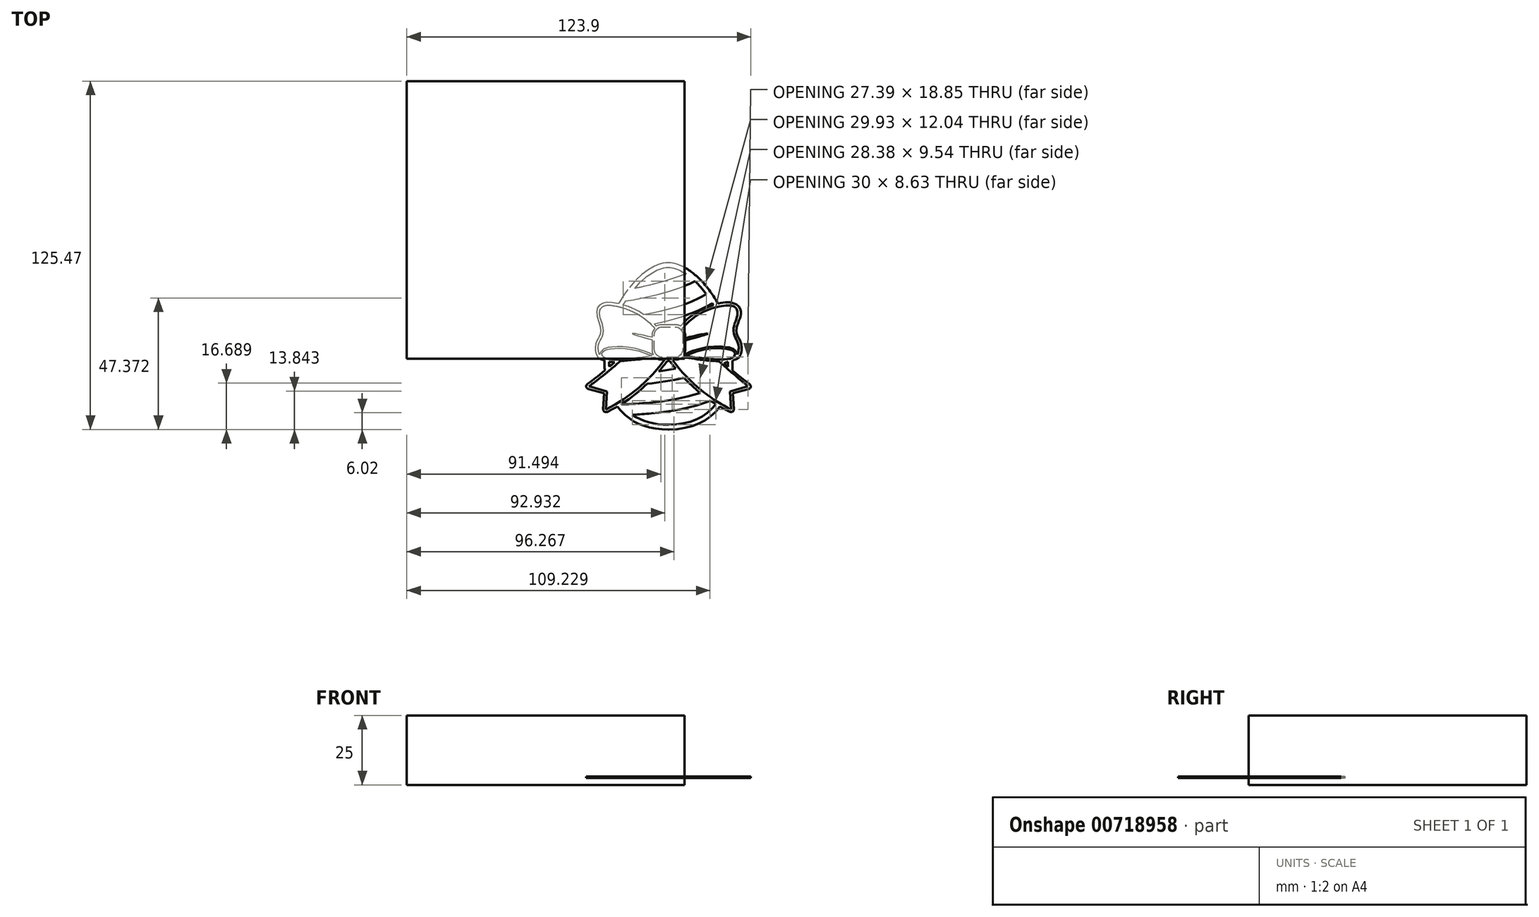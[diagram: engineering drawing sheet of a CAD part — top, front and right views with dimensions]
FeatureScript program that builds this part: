
annotation { "Feature Type Name" : "Feature", "Feature Type Description" : "" }
export const myFeature = defineFeature(function(context is Context, id is Id, definition is map)
    precondition{}
    {
        {
            var Q0;
            Q0=qCreatedBy(makeId("Top.planeOp"),FACE);
            var sketch = newSketch(context, id + "F0", { "sketchPlane" : qUnion([Q0])});
            skLineSegment(sketch, "E0.bottom", {"start": v(0, 0) * mm, "end": v(-100, 0) * mm});
            skLineSegment(sketch, "E0.top", {"start": v(0, 100) * mm, "end": v(-100, 100) * mm});
            skLineSegment(sketch, "E0.left", {"start": v(0, 0) * mm, "end": v(0, 100) * mm});
            skLineSegment(sketch, "E0.right", {"start": v(-100, 0) * mm, "end": v(-100, 100) * mm});
            skSolve(sketch);
        }
        {
            var Q0;
            Q0 = qSketchRegion(id + "F0", true);
            extrude(context, id + "F1", {"entities" : qUnion([Q0]), "depth" : 25 * mm, "offsetDistance" : 25 * mm});
        }
        {
            var Q0;
            Q0=makeQuery(id+"F1.opExtrude","CAP_FACE",FACE,{"disambiguationData":[OSD([sQuery(id+"F0.wireOp",EDGE,"E0.bottom"),sQuery(id+"F0.wireOp",EDGE,"E0.top"),sQuery(id+"F0.wireOp",EDGE,"E0.left"),sQuery(id+"F0.wireOp",EDGE,"E0.right")])],"isStart":false});
            var sketch = newSketch(context, id + "F2", { "sketchPlane" : qUnion([Q0])});
            skLineSegment(sketch, "E1", {"start": v(163.81, -117.28) * mm, "end": v(167.38, -182.07) * mm});
            skLineSegment(sketch, "E2", {"start": v(167.38, -182.07) * mm, "end": v(154.84, -175.69) * mm});
            skLineSegment(sketch, "E3", {"start": v(154.84, -175.69) * mm, "end": v(142.58, -169.14) * mm});
            skLineSegment(sketch, "E4", {"start": v(142.58, -169.14) * mm, "end": v(130.5, -162.31) * mm});
            skLineSegment(sketch, "E5", {"start": v(130.5, -162.31) * mm, "end": v(118.44, -155.06) * mm});
            skLineSegment(sketch, "E6", {"start": v(118.44, -155.06) * mm, "end": v(106.3, -147.27) * mm});
            skLineSegment(sketch, "E7", {"start": v(106.3, -147.27) * mm, "end": v(93.93, -138.8) * mm});
            skLineSegment(sketch, "E8", {"start": v(93.93, -138.8) * mm, "end": v(81.23, -129.55) * mm});
            skLineSegment(sketch, "E9", {"start": v(81.23, -129.55) * mm, "end": v(68.05, -119.37) * mm});
            skLineSegment(sketch, "E10", {"start": v(68.05, -119.37) * mm, "end": v(51.97, -106.13) * mm});
            skLineSegment(sketch, "E11", {"start": v(51.97, -106.13) * mm, "end": v(36.41, -92.4) * mm});
            skLineSegment(sketch, "E12", {"start": v(36.41, -92.4) * mm, "end": v(21.4, -78.23) * mm});
            skLineSegment(sketch, "E13", {"start": v(21.4, -78.23) * mm, "end": v(6.97, -63.66) * mm});
            skLineSegment(sketch, "E14", {"start": v(6.97, -63.66) * mm, "end": v(-6.88, -48.74) * mm});
            skLineSegment(sketch, "E15", {"start": v(-6.88, -48.74) * mm, "end": v(-20.11, -33.52) * mm});
            skLineSegment(sketch, "E16", {"start": v(-20.11, -33.52) * mm, "end": v(-32.72, -18.04) * mm});
            skLineSegment(sketch, "E17", {"start": v(-32.72, -18.04) * mm, "end": v(-44.66, -2.35) * mm});
            skLineSegment(sketch, "E18", {"start": v(-44.66, -2.35) * mm, "end": v(-29.92, -2.35) * mm});
            skLineSegment(sketch, "E19", {"start": v(-29.92, -2.35) * mm, "end": v(-26.75, -2.2) * mm});
            skLineSegment(sketch, "E20", {"start": v(-26.75, -2.2) * mm, "end": v(-23.67, -1.74) * mm});
            skLineSegment(sketch, "E21", {"start": v(-23.67, -1.74) * mm, "end": v(-20.68, -1) * mm});
            skLineSegment(sketch, "E22", {"start": v(-20.68, -1) * mm, "end": v(-17.82, 0) * mm});
            skLineSegment(sketch, "E23", {"start": v(-17.82, 0) * mm, "end": v(-15.08, 1.27) * mm});
            skLineSegment(sketch, "E24", {"start": v(-15.08, 1.27) * mm, "end": v(-12.49, 2.77) * mm});
            skLineSegment(sketch, "E25", {"start": v(-12.49, 2.77) * mm, "end": v(-10.05, 4.5) * mm});
            skLineSegment(sketch, "E26", {"start": v(-10.05, 4.5) * mm, "end": v(-7.78, 6.44) * mm});
            skLineSegment(sketch, "E27", {"start": v(-7.78, 6.44) * mm, "end": v(3.96, 4.52) * mm});
            skLineSegment(sketch, "E28", {"start": v(3.96, 4.52) * mm, "end": v(15.22, 2.75) * mm});
            skLineSegment(sketch, "E29", {"start": v(15.22, 2.75) * mm, "end": v(26.02, 1.11) * mm});
            skLineSegment(sketch, "E30", {"start": v(26.02, 1.11) * mm, "end": v(36.37, -0.38) * mm});
            skLineSegment(sketch, "E31", {"start": v(36.37, -0.38) * mm, "end": v(46.3, -1.74) * mm});
            skLineSegment(sketch, "E32", {"start": v(46.3, -1.74) * mm, "end": v(55.8, -2.97) * mm});
            skLineSegment(sketch, "E33", {"start": v(55.8, -2.97) * mm, "end": v(64.92, -4.07) * mm});
            skLineSegment(sketch, "E34", {"start": v(64.92, -4.07) * mm, "end": v(73.64, -5.04) * mm});
            skLineSegment(sketch, "E35", {"start": v(73.64, -5.04) * mm, "end": v(80.45, -5.73) * mm});
            skLineSegment(sketch, "E36", {"start": v(80.45, -5.73) * mm, "end": v(87.02, -6.34) * mm});
            skLineSegment(sketch, "E37", {"start": v(87.02, -6.34) * mm, "end": v(93.36, -6.88) * mm});
            skLineSegment(sketch, "E38", {"start": v(93.36, -6.88) * mm, "end": v(99.47, -7.32) * mm});
            skLineSegment(sketch, "E39", {"start": v(99.47, -7.32) * mm, "end": v(105.35, -7.69) * mm});
            skLineSegment(sketch, "E40", {"start": v(105.35, -7.69) * mm, "end": v(111, -7.97) * mm});
            skLineSegment(sketch, "E41", {"start": v(111, -7.97) * mm, "end": v(116.44, -8.17) * mm});
            skLineSegment(sketch, "E42", {"start": v(116.44, -8.17) * mm, "end": v(121.65, -8.28) * mm});
            skLineSegment(sketch, "E43", {"start": v(121.65, -8.28) * mm, "end": v(123.37, -8.3) * mm});
            skLineSegment(sketch, "E44", {"start": v(123.37, -8.3) * mm, "end": v(139.96, -22.95) * mm});
            skLineSegment(sketch, "E45", {"start": v(139.96, -22.95) * mm, "end": v(155.27, -36.35) * mm});
            skLineSegment(sketch, "E46", {"start": v(155.27, -36.35) * mm, "end": v(169.47, -48.67) * mm});
            skLineSegment(sketch, "E47", {"start": v(169.47, -48.67) * mm, "end": v(182.71, -60.04) * mm});
            skLineSegment(sketch, "E48", {"start": v(182.71, -60.04) * mm, "end": v(195.15, -70.62) * mm});
            skLineSegment(sketch, "E49", {"start": v(195.15, -70.62) * mm, "end": v(206.94, -80.56) * mm});
            skLineSegment(sketch, "E50", {"start": v(206.94, -80.56) * mm, "end": v(218.25, -90) * mm});
            skLineSegment(sketch, "E51", {"start": v(218.25, -90) * mm, "end": v(229.24, -99.1) * mm});
            skLineSegment(sketch, "E52", {"start": v(229.24, -99.1) * mm, "end": v(163.81, -117.28) * mm});
            skLineSegment(sketch, "E53", {"start": v(-56.23, -237.65) * mm, "end": v(-56.4, -237.65) * mm});
            skLineSegment(sketch, "E54", {"start": v(-56.4, -237.65) * mm, "end": v(-56.55, -237.65) * mm});
            skLineSegment(sketch, "E55", {"start": v(-56.55, -237.65) * mm, "end": v(-56.7, -237.65) * mm});
            skLineSegment(sketch, "E56", {"start": v(-56.7, -237.65) * mm, "end": v(-56.86, -237.66) * mm});
            skLineSegment(sketch, "E57", {"start": v(-56.86, -237.66) * mm, "end": v(-57.02, -237.66) * mm});
            skLineSegment(sketch, "E58", {"start": v(-57.02, -237.66) * mm, "end": v(-57.17, -237.66) * mm});
            skLineSegment(sketch, "E59", {"start": v(-57.17, -237.66) * mm, "end": v(-57.33, -237.66) * mm});
            skLineSegment(sketch, "E60", {"start": v(-57.33, -237.66) * mm, "end": v(-57.49, -237.66) * mm});
            skLineSegment(sketch, "E61", {"start": v(-57.49, -237.66) * mm, "end": v(-76.77, -237.1) * mm});
            skLineSegment(sketch, "E62", {"start": v(-76.77, -237.1) * mm, "end": v(-95.19, -235.4) * mm});
            skLineSegment(sketch, "E63", {"start": v(-95.19, -235.4) * mm, "end": v(-112.74, -232.6) * mm});
            skLineSegment(sketch, "E64", {"start": v(-112.74, -232.6) * mm, "end": v(-129.41, -228.67) * mm});
            skLineSegment(sketch, "E65", {"start": v(-129.41, -228.67) * mm, "end": v(-145.22, -223.63) * mm});
            skLineSegment(sketch, "E66", {"start": v(-145.22, -223.63) * mm, "end": v(-160.14, -217.47) * mm});
            skLineSegment(sketch, "E67", {"start": v(-160.14, -217.47) * mm, "end": v(-174.18, -210.21) * mm});
            skLineSegment(sketch, "E68", {"start": v(-174.18, -210.21) * mm, "end": v(-187.33, -201.84) * mm});
            skLineSegment(sketch, "E69", {"start": v(-187.33, -201.84) * mm, "end": v(-178.84, -201.39) * mm});
            skLineSegment(sketch, "E70", {"start": v(-178.84, -201.39) * mm, "end": v(-170.35, -200.87) * mm});
            skLineSegment(sketch, "E71", {"start": v(-170.35, -200.87) * mm, "end": v(-161.86, -200.3) * mm});
            skLineSegment(sketch, "E72", {"start": v(-161.86, -200.3) * mm, "end": v(-153.4, -199.68) * mm});
            skLineSegment(sketch, "E73", {"start": v(-153.4, -199.68) * mm, "end": v(-144.93, -199.02) * mm});
            skLineSegment(sketch, "E74", {"start": v(-144.93, -199.02) * mm, "end": v(-136.49, -198.3) * mm});
            skLineSegment(sketch, "E75", {"start": v(-136.49, -198.3) * mm, "end": v(-128.05, -197.54) * mm});
            skLineSegment(sketch, "E76", {"start": v(-128.05, -197.54) * mm, "end": v(-119.64, -196.73) * mm});
            skLineSegment(sketch, "E77", {"start": v(-119.64, -196.73) * mm, "end": v(-92.7, -193.81) * mm});
            skLineSegment(sketch, "E78", {"start": v(-92.7, -193.81) * mm, "end": v(-65.6, -190.27) * mm});
            skLineSegment(sketch, "E79", {"start": v(-65.6, -190.27) * mm, "end": v(-38.45, -186.02) * mm});
            skLineSegment(sketch, "E80", {"start": v(-38.45, -186.02) * mm, "end": v(-11.35, -181) * mm});
            skLineSegment(sketch, "E81", {"start": v(-11.35, -181) * mm, "end": v(15.61, -175.09) * mm});
            skLineSegment(sketch, "E82", {"start": v(15.61, -175.09) * mm, "end": v(42.34, -168.23) * mm});
            skLineSegment(sketch, "E83", {"start": v(42.34, -168.23) * mm, "end": v(68.74, -160.35) * mm});
            skLineSegment(sketch, "E84", {"start": v(68.74, -160.35) * mm, "end": v(94.7, -151.34) * mm});
            skLineSegment(sketch, "E85", {"start": v(94.7, -151.34) * mm, "end": v(96.9, -152.84) * mm});
            skLineSegment(sketch, "E86", {"start": v(96.9, -152.84) * mm, "end": v(99.12, -154.32) * mm});
            skLineSegment(sketch, "E87", {"start": v(99.12, -154.32) * mm, "end": v(101.34, -155.8) * mm});
            skLineSegment(sketch, "E88", {"start": v(101.34, -155.8) * mm, "end": v(103.58, -157.28) * mm});
            skLineSegment(sketch, "E89", {"start": v(103.58, -157.28) * mm, "end": v(105.84, -158.75) * mm});
            skLineSegment(sketch, "E90", {"start": v(105.84, -158.75) * mm, "end": v(108.1, -160.2) * mm});
            skLineSegment(sketch, "E91", {"start": v(108.1, -160.2) * mm, "end": v(110.38, -161.66) * mm});
            skLineSegment(sketch, "E92", {"start": v(110.38, -161.66) * mm, "end": v(112.68, -163.1) * mm});
            skLineSegment(sketch, "E93", {"start": v(112.68, -163.1) * mm, "end": v(98.11, -180.4) * mm});
            skLineSegment(sketch, "E94", {"start": v(98.11, -180.4) * mm, "end": v(81.65, -195.45) * mm});
            skLineSegment(sketch, "E95", {"start": v(81.65, -195.45) * mm, "end": v(63.3, -208.22) * mm});
            skLineSegment(sketch, "E96", {"start": v(63.3, -208.22) * mm, "end": v(43.09, -218.7) * mm});
            skLineSegment(sketch, "E97", {"start": v(43.09, -218.7) * mm, "end": v(21.01, -226.9) * mm});
            skLineSegment(sketch, "E98", {"start": v(21.01, -226.9) * mm, "end": v(-2.9, -232.8) * mm});
            skLineSegment(sketch, "E99", {"start": v(-2.9, -232.8) * mm, "end": v(-28.66, -236.39) * mm});
            skLineSegment(sketch, "E100", {"start": v(-28.66, -236.39) * mm, "end": v(-56.23, -237.65) * mm});
            skLineSegment(sketch, "E101", {"start": v(-226.12, -163.97) * mm, "end": v(-226.23, -163.83) * mm});
            skLineSegment(sketch, "E102", {"start": v(-226.23, -163.83) * mm, "end": v(-226.33, -163.68) * mm});
            skLineSegment(sketch, "E103", {"start": v(-226.33, -163.68) * mm, "end": v(-226.44, -163.54) * mm});
            skLineSegment(sketch, "E104", {"start": v(-226.44, -163.54) * mm, "end": v(-226.54, -163.39) * mm});
            skLineSegment(sketch, "E105", {"start": v(-226.54, -163.39) * mm, "end": v(-226.65, -163.24) * mm});
            skLineSegment(sketch, "E106", {"start": v(-226.65, -163.24) * mm, "end": v(-226.75, -163.1) * mm});
            skLineSegment(sketch, "E107", {"start": v(-226.75, -163.1) * mm, "end": v(-226.86, -162.95) * mm});
            skLineSegment(sketch, "E108", {"start": v(-226.86, -162.95) * mm, "end": v(-226.96, -162.8) * mm});
            skLineSegment(sketch, "E109", {"start": v(-226.96, -162.8) * mm, "end": v(-213.7, -154.2) * mm});
            skLineSegment(sketch, "E110", {"start": v(-213.7, -154.2) * mm, "end": v(-200.9, -145.37) * mm});
            skLineSegment(sketch, "E111", {"start": v(-200.9, -145.37) * mm, "end": v(-188.59, -136.36) * mm});
            skLineSegment(sketch, "E112", {"start": v(-188.59, -136.36) * mm, "end": v(-176.75, -127.22) * mm});
            skLineSegment(sketch, "E113", {"start": v(-176.75, -127.22) * mm, "end": v(-165.4, -117.97) * mm});
            skLineSegment(sketch, "E114", {"start": v(-165.4, -117.97) * mm, "end": v(-154.53, -108.67) * mm});
            skLineSegment(sketch, "E115", {"start": v(-154.53, -108.67) * mm, "end": v(-144.14, -99.36) * mm});
            skLineSegment(sketch, "E116", {"start": v(-144.14, -99.36) * mm, "end": v(-134.25, -90.08) * mm});
            skLineSegment(sketch, "E117", {"start": v(-134.25, -90.08) * mm, "end": v(-117.46, -88.18) * mm});
            skLineSegment(sketch, "E118", {"start": v(-117.46, -88.18) * mm, "end": v(-100.88, -86.12) * mm});
            skLineSegment(sketch, "E119", {"start": v(-100.88, -86.12) * mm, "end": v(-84.43, -83.88) * mm});
            skLineSegment(sketch, "E120", {"start": v(-84.43, -83.88) * mm, "end": v(-68.06, -81.4) * mm});
            skLineSegment(sketch, "E121", {"start": v(-68.06, -81.4) * mm, "end": v(-51.68, -78.67) * mm});
            skLineSegment(sketch, "E122", {"start": v(-51.68, -78.67) * mm, "end": v(-35.25, -75.65) * mm});
            skLineSegment(sketch, "E123", {"start": v(-35.25, -75.65) * mm, "end": v(-18.7, -72.29) * mm});
            skLineSegment(sketch, "E124", {"start": v(-18.7, -72.29) * mm, "end": v(-1.95, -68.57) * mm});
            skLineSegment(sketch, "E125", {"start": v(-1.95, -68.57) * mm, "end": v(4.46, -75.23) * mm});
            skLineSegment(sketch, "E126", {"start": v(4.46, -75.23) * mm, "end": v(11.14, -81.96) * mm});
            skLineSegment(sketch, "E127", {"start": v(11.14, -81.96) * mm, "end": v(18.1, -88.76) * mm});
            skLineSegment(sketch, "E128", {"start": v(18.1, -88.76) * mm, "end": v(25.31, -95.6) * mm});
            skLineSegment(sketch, "E129", {"start": v(25.31, -95.6) * mm, "end": v(32.8, -102.47) * mm});
            skLineSegment(sketch, "E130", {"start": v(32.8, -102.47) * mm, "end": v(40.55, -109.35) * mm});
            skLineSegment(sketch, "E131", {"start": v(40.55, -109.35) * mm, "end": v(48.56, -116.23) * mm});
            skLineSegment(sketch, "E132", {"start": v(48.56, -116.23) * mm, "end": v(56.84, -123.08) * mm});
            skLineSegment(sketch, "E133", {"start": v(56.84, -123.08) * mm, "end": v(34.49, -129.86) * mm});
            skLineSegment(sketch, "E134", {"start": v(34.49, -129.86) * mm, "end": v(11.87, -135.85) * mm});
            skLineSegment(sketch, "E135", {"start": v(11.87, -135.85) * mm, "end": v(-10.94, -141.1) * mm});
            skLineSegment(sketch, "E136", {"start": v(-10.94, -141.1) * mm, "end": v(-33.9, -145.66) * mm});
            skLineSegment(sketch, "E137", {"start": v(-33.9, -145.66) * mm, "end": v(-56.93, -149.6) * mm});
            skLineSegment(sketch, "E138", {"start": v(-56.93, -149.6) * mm, "end": v(-79.98, -152.96) * mm});
            skLineSegment(sketch, "E139", {"start": v(-79.98, -152.96) * mm, "end": v(-102.98, -155.8) * mm});
            skLineSegment(sketch, "E140", {"start": v(-102.98, -155.8) * mm, "end": v(-125.86, -158.2) * mm});
            skLineSegment(sketch, "E141", {"start": v(-125.86, -158.2) * mm, "end": v(-138.3, -159.33) * mm});
            skLineSegment(sketch, "E142", {"start": v(-138.3, -159.33) * mm, "end": v(-150.79, -160.36) * mm});
            skLineSegment(sketch, "E143", {"start": v(-150.79, -160.36) * mm, "end": v(-163.3, -161.28) * mm});
            skLineSegment(sketch, "E144", {"start": v(-163.3, -161.28) * mm, "end": v(-175.83, -162.08) * mm});
            skLineSegment(sketch, "E145", {"start": v(-175.83, -162.08) * mm, "end": v(-188.39, -162.75) * mm});
            skLineSegment(sketch, "E146", {"start": v(-188.39, -162.75) * mm, "end": v(-200.96, -163.3) * mm});
            skLineSegment(sketch, "E147", {"start": v(-200.96, -163.3) * mm, "end": v(-213.54, -163.7) * mm});
            skLineSegment(sketch, "E148", {"start": v(-213.54, -163.7) * mm, "end": v(-226.12, -163.97) * mm});
            skLineSegment(sketch, "E149", {"start": v(-282.45, -182.06) * mm, "end": v(-278.88, -117.28) * mm});
            skLineSegment(sketch, "E150", {"start": v(-278.88, -117.28) * mm, "end": v(-343.74, -99.24) * mm});
            skLineSegment(sketch, "E151", {"start": v(-343.74, -99.24) * mm, "end": v(-336.1, -93.6) * mm});
            skLineSegment(sketch, "E152", {"start": v(-336.1, -93.6) * mm, "end": v(-331.86, -90.45) * mm});
            skLineSegment(sketch, "E153", {"start": v(-331.86, -90.45) * mm, "end": v(-327, -86.8) * mm});
            skLineSegment(sketch, "E154", {"start": v(-327, -86.8) * mm, "end": v(-321.5, -82.62) * mm});
            skLineSegment(sketch, "E155", {"start": v(-321.5, -82.62) * mm, "end": v(-315.4, -77.93) * mm});
            skLineSegment(sketch, "E156", {"start": v(-315.4, -77.93) * mm, "end": v(-308.71, -72.73) * mm});
            skLineSegment(sketch, "E157", {"start": v(-308.71, -72.73) * mm, "end": v(-301.45, -67.01) * mm});
            skLineSegment(sketch, "E158", {"start": v(-301.45, -67.01) * mm, "end": v(-293.64, -60.8) * mm});
            skLineSegment(sketch, "E159", {"start": v(-293.64, -60.8) * mm, "end": v(-285.29, -54.06) * mm});
            skLineSegment(sketch, "E160", {"start": v(-285.29, -54.06) * mm, "end": v(-283.42, -52.55) * mm});
            skLineSegment(sketch, "E161", {"start": v(-283.42, -52.55) * mm, "end": v(-281.54, -51.02) * mm});
            skLineSegment(sketch, "E162", {"start": v(-281.54, -51.02) * mm, "end": v(-279.63, -49.46) * mm});
            skLineSegment(sketch, "E163", {"start": v(-279.63, -49.46) * mm, "end": v(-277.7, -47.88) * mm});
            skLineSegment(sketch, "E164", {"start": v(-277.7, -47.88) * mm, "end": v(-275.73, -46.27) * mm});
            skLineSegment(sketch, "E165", {"start": v(-275.73, -46.27) * mm, "end": v(-273.75, -44.64) * mm});
            skLineSegment(sketch, "E166", {"start": v(-273.75, -44.64) * mm, "end": v(-271.74, -42.98) * mm});
            skLineSegment(sketch, "E167", {"start": v(-271.74, -42.98) * mm, "end": v(-269.71, -41.3) * mm});
            skLineSegment(sketch, "E168", {"start": v(-269.71, -41.3) * mm, "end": v(-265.33, -37.67) * mm});
            skLineSegment(sketch, "E169", {"start": v(-265.33, -37.67) * mm, "end": v(-260.85, -33.93) * mm});
            skLineSegment(sketch, "E170", {"start": v(-260.85, -33.93) * mm, "end": v(-256.28, -30.1) * mm});
            skLineSegment(sketch, "E171", {"start": v(-256.28, -30.1) * mm, "end": v(-251.6, -26.15) * mm});
            skLineSegment(sketch, "E172", {"start": v(-251.6, -26.15) * mm, "end": v(-246.83, -22.1) * mm});
            skLineSegment(sketch, "E173", {"start": v(-246.83, -22.1) * mm, "end": v(-241.95, -17.93) * mm});
            skLineSegment(sketch, "E174", {"start": v(-241.95, -17.93) * mm, "end": v(-236.97, -13.66) * mm});
            skLineSegment(sketch, "E175", {"start": v(-236.97, -13.66) * mm, "end": v(-231.9, -9.26) * mm});
            skLineSegment(sketch, "E176", {"start": v(-231.9, -9.26) * mm, "end": v(-230.65, -8.2) * mm});
            skLineSegment(sketch, "E177", {"start": v(-230.65, -8.2) * mm, "end": v(-229.02, -8.13) * mm});
            skLineSegment(sketch, "E178", {"start": v(-229.02, -8.13) * mm, "end": v(-217.5, -7.57) * mm});
            skLineSegment(sketch, "E179", {"start": v(-217.5, -7.57) * mm, "end": v(-205.04, -6.67) * mm});
            skLineSegment(sketch, "E180", {"start": v(-205.04, -6.67) * mm, "end": v(-191.57, -5.4) * mm});
            skLineSegment(sketch, "E181", {"start": v(-191.57, -5.4) * mm, "end": v(-177.03, -3.78) * mm});
            skLineSegment(sketch, "E182", {"start": v(-177.03, -3.78) * mm, "end": v(-161.35, -1.78) * mm});
            skLineSegment(sketch, "E183", {"start": v(-161.35, -1.78) * mm, "end": v(-144.47, 0.6) * mm});
            skLineSegment(sketch, "E184", {"start": v(-144.47, 0.6) * mm, "end": v(-126.3, 3.36) * mm});
            skLineSegment(sketch, "E185", {"start": v(-126.3, 3.36) * mm, "end": v(-106.8, 6.52) * mm});
            skLineSegment(sketch, "E186", {"start": v(-106.8, 6.52) * mm, "end": v(-104.54, 4.56) * mm});
            skLineSegment(sketch, "E187", {"start": v(-104.54, 4.56) * mm, "end": v(-102.1, 2.82) * mm});
            skLineSegment(sketch, "E188", {"start": v(-102.1, 2.82) * mm, "end": v(-99.5, 1.3) * mm});
            skLineSegment(sketch, "E189", {"start": v(-99.5, 1.3) * mm, "end": v(-96.74, 0.03) * mm});
            skLineSegment(sketch, "E190", {"start": v(-96.74, 0.03) * mm, "end": v(-93.86, -1) * mm});
            skLineSegment(sketch, "E191", {"start": v(-93.86, -1) * mm, "end": v(-90.87, -1.74) * mm});
            skLineSegment(sketch, "E192", {"start": v(-90.87, -1.74) * mm, "end": v(-87.77, -2.2) * mm});
            skLineSegment(sketch, "E193", {"start": v(-87.77, -2.2) * mm, "end": v(-84.59, -2.35) * mm});
            skLineSegment(sketch, "E194", {"start": v(-84.59, -2.35) * mm, "end": v(-70.37, -2.35) * mm});
            skLineSegment(sketch, "E195", {"start": v(-70.37, -2.35) * mm, "end": v(-91.42, -29.4) * mm});
            skLineSegment(sketch, "E196", {"start": v(-91.42, -29.4) * mm, "end": v(-114.02, -55.34) * mm});
            skLineSegment(sketch, "E197", {"start": v(-114.02, -55.34) * mm, "end": v(-138.17, -80.06) * mm});
            skLineSegment(sketch, "E198", {"start": v(-138.17, -80.06) * mm, "end": v(-163.87, -103.47) * mm});
            skLineSegment(sketch, "E199", {"start": v(-163.87, -103.47) * mm, "end": v(-191.14, -125.47) * mm});
            skLineSegment(sketch, "E200", {"start": v(-191.14, -125.47) * mm, "end": v(-220, -145.97) * mm});
            skLineSegment(sketch, "E201", {"start": v(-220, -145.97) * mm, "end": v(-250.42, -164.87) * mm});
            skLineSegment(sketch, "E202", {"start": v(-250.42, -164.87) * mm, "end": v(-282.45, -182.06) * mm});
            skLineSegment(sketch, "E203", {"start": v(-271.42, -10.7) * mm, "end": v(-269.07, -11) * mm});
            skLineSegment(sketch, "E204", {"start": v(-269.07, -11) * mm, "end": v(-266.65, -11.27) * mm});
            skLineSegment(sketch, "E205", {"start": v(-266.65, -11.27) * mm, "end": v(-264.17, -11.5) * mm});
            skLineSegment(sketch, "E206", {"start": v(-264.17, -11.5) * mm, "end": v(-261.61, -11.68) * mm});
            skLineSegment(sketch, "E207", {"start": v(-261.61, -11.68) * mm, "end": v(-259, -11.84) * mm});
            skLineSegment(sketch, "E208", {"start": v(-259, -11.84) * mm, "end": v(-256.3, -11.97) * mm});
            skLineSegment(sketch, "E209", {"start": v(-256.3, -11.97) * mm, "end": v(-253.52, -12.06) * mm});
            skLineSegment(sketch, "E210", {"start": v(-253.52, -12.06) * mm, "end": v(-250.67, -12.13) * mm});
            skLineSegment(sketch, "E211", {"start": v(-250.67, -12.13) * mm, "end": v(-253.28, -14.36) * mm});
            skLineSegment(sketch, "E212", {"start": v(-253.28, -14.36) * mm, "end": v(-255.86, -16.55) * mm});
            skLineSegment(sketch, "E213", {"start": v(-255.86, -16.55) * mm, "end": v(-258.4, -18.7) * mm});
            skLineSegment(sketch, "E214", {"start": v(-258.4, -18.7) * mm, "end": v(-260.91, -20.82) * mm});
            skLineSegment(sketch, "E215", {"start": v(-260.91, -20.82) * mm, "end": v(-263.4, -22.9) * mm});
            skLineSegment(sketch, "E216", {"start": v(-263.4, -22.9) * mm, "end": v(-265.85, -24.96) * mm});
            skLineSegment(sketch, "E217", {"start": v(-265.85, -24.96) * mm, "end": v(-268.28, -27) * mm});
            skLineSegment(sketch, "E218", {"start": v(-268.28, -27) * mm, "end": v(-270.68, -29) * mm});
            skLineSegment(sketch, "E219", {"start": v(-270.68, -29) * mm, "end": v(-270.82, -26.73) * mm});
            skLineSegment(sketch, "E220", {"start": v(-270.82, -26.73) * mm, "end": v(-270.95, -24.45) * mm});
            skLineSegment(sketch, "E221", {"start": v(-270.95, -24.45) * mm, "end": v(-271.07, -22.16) * mm});
            skLineSegment(sketch, "E222", {"start": v(-271.07, -22.16) * mm, "end": v(-271.17, -19.88) * mm});
            skLineSegment(sketch, "E223", {"start": v(-271.17, -19.88) * mm, "end": v(-271.25, -17.6) * mm});
            skLineSegment(sketch, "E224", {"start": v(-271.25, -17.6) * mm, "end": v(-271.33, -15.3) * mm});
            skLineSegment(sketch, "E225", {"start": v(-271.33, -15.3) * mm, "end": v(-271.38, -13) * mm});
            skLineSegment(sketch, "E226", {"start": v(-271.38, -13) * mm, "end": v(-271.42, -10.7) * mm});
            skLineSegment(sketch, "E227", {"start": v(-290.4, 5.49) * mm, "end": v(-292.84, 7.34) * mm});
            skLineSegment(sketch, "E228", {"start": v(-292.84, 7.34) * mm, "end": v(-294.9, 9.9) * mm});
            skLineSegment(sketch, "E229", {"start": v(-294.9, 9.9) * mm, "end": v(-296.34, 13) * mm});
            skLineSegment(sketch, "E230", {"start": v(-296.34, 13) * mm, "end": v(-296.95, 16.44) * mm});
            skLineSegment(sketch, "E231", {"start": v(-296.95, 16.44) * mm, "end": v(-296.5, 20.07) * mm});
            skLineSegment(sketch, "E232", {"start": v(-296.5, 20.07) * mm, "end": v(-294.8, 23.7) * mm});
            skLineSegment(sketch, "E233", {"start": v(-294.8, 23.7) * mm, "end": v(-291.59, 27.15) * mm});
            skLineSegment(sketch, "E234", {"start": v(-291.59, 27.15) * mm, "end": v(-286.67, 30.27) * mm});
            skLineSegment(sketch, "E235", {"start": v(-286.67, 30.27) * mm, "end": v(-279.2, 32.97) * mm});
            skLineSegment(sketch, "E236", {"start": v(-279.2, 32.97) * mm, "end": v(-267.67, 35.5) * mm});
            skLineSegment(sketch, "E237", {"start": v(-267.67, 35.5) * mm, "end": v(-252.5, 37.37) * mm});
            skLineSegment(sketch, "E238", {"start": v(-252.5, 37.37) * mm, "end": v(-234.13, 38.04) * mm});
            skLineSegment(sketch, "E239", {"start": v(-234.13, 38.04) * mm, "end": v(-212.95, 37.01) * mm});
            skLineSegment(sketch, "E240", {"start": v(-212.95, 37.01) * mm, "end": v(-189.4, 33.76) * mm});
            skLineSegment(sketch, "E241", {"start": v(-189.4, 33.76) * mm, "end": v(-163.88, 27.79) * mm});
            skLineSegment(sketch, "E242", {"start": v(-163.88, 27.79) * mm, "end": v(-136.82, 18.56) * mm});
            skLineSegment(sketch, "E243", {"start": v(-136.82, 18.56) * mm, "end": v(-136.4, 18.4) * mm});
            skLineSegment(sketch, "E244", {"start": v(-136.4, 18.4) * mm, "end": v(-135.98, 18.24) * mm});
            skLineSegment(sketch, "E245", {"start": v(-135.98, 18.24) * mm, "end": v(-135.55, 18.08) * mm});
            skLineSegment(sketch, "E246", {"start": v(-135.55, 18.08) * mm, "end": v(-135.13, 17.92) * mm});
            skLineSegment(sketch, "E247", {"start": v(-135.13, 17.92) * mm, "end": v(-134.71, 17.76) * mm});
            skLineSegment(sketch, "E248", {"start": v(-134.71, 17.76) * mm, "end": v(-134.29, 17.6) * mm});
            skLineSegment(sketch, "E249", {"start": v(-134.29, 17.6) * mm, "end": v(-133.87, 17.43) * mm});
            skLineSegment(sketch, "E250", {"start": v(-133.87, 17.43) * mm, "end": v(-133.45, 17.26) * mm});
            skLineSegment(sketch, "E251", {"start": v(-133.45, 17.26) * mm, "end": v(-118.07, 10.91) * mm});
            skLineSegment(sketch, "E252", {"start": v(-118.07, 10.91) * mm, "end": v(-134.51, 8.4) * mm});
            skLineSegment(sketch, "E253", {"start": v(-134.51, 8.4) * mm, "end": v(-151.35, 5.91) * mm});
            skLineSegment(sketch, "E254", {"start": v(-151.35, 5.91) * mm, "end": v(-167.14, 3.76) * mm});
            skLineSegment(sketch, "E255", {"start": v(-167.14, 3.76) * mm, "end": v(-181.9, 1.95) * mm});
            skLineSegment(sketch, "E256", {"start": v(-181.9, 1.95) * mm, "end": v(-195.69, 0.48) * mm});
            skLineSegment(sketch, "E257", {"start": v(-195.69, 0.48) * mm, "end": v(-208.5, -0.67) * mm});
            skLineSegment(sketch, "E258", {"start": v(-208.5, -0.67) * mm, "end": v(-220.36, -1.48) * mm});
            skLineSegment(sketch, "E259", {"start": v(-220.36, -1.48) * mm, "end": v(-231.3, -1.97) * mm});
            skLineSegment(sketch, "E260", {"start": v(-231.3, -1.97) * mm, "end": v(-241.33, -2.13) * mm});
            skLineSegment(sketch, "E261", {"start": v(-241.33, -2.13) * mm, "end": v(-242.35, -2.13) * mm});
            skLineSegment(sketch, "E262", {"start": v(-242.35, -2.13) * mm, "end": v(-246.55, -2.11) * mm});
            skLineSegment(sketch, "E263", {"start": v(-246.55, -2.11) * mm, "end": v(-250.57, -2.06) * mm});
            skLineSegment(sketch, "E264", {"start": v(-250.57, -2.06) * mm, "end": v(-254.42, -1.95) * mm});
            skLineSegment(sketch, "E265", {"start": v(-254.42, -1.95) * mm, "end": v(-258.1, -1.8) * mm});
            skLineSegment(sketch, "E266", {"start": v(-258.1, -1.8) * mm, "end": v(-261.64, -1.59) * mm});
            skLineSegment(sketch, "E267", {"start": v(-261.64, -1.59) * mm, "end": v(-265.02, -1.3) * mm});
            skLineSegment(sketch, "E268", {"start": v(-265.02, -1.3) * mm, "end": v(-268.26, -0.96) * mm});
            skLineSegment(sketch, "E269", {"start": v(-268.26, -0.96) * mm, "end": v(-271.35, -0.54) * mm});
            skLineSegment(sketch, "E270", {"start": v(-271.35, -0.54) * mm, "end": v(-273.72, -0.15) * mm});
            skLineSegment(sketch, "E271", {"start": v(-273.72, -0.15) * mm, "end": v(-276.01, 0.3) * mm});
            skLineSegment(sketch, "E272", {"start": v(-276.01, 0.3) * mm, "end": v(-278.22, 0.82) * mm});
            skLineSegment(sketch, "E273", {"start": v(-278.22, 0.82) * mm, "end": v(-280.35, 1.4) * mm});
            skLineSegment(sketch, "E274", {"start": v(-280.35, 1.4) * mm, "end": v(-282.4, 2.04) * mm});
            skLineSegment(sketch, "E275", {"start": v(-282.4, 2.04) * mm, "end": v(-284.39, 2.75) * mm});
            skLineSegment(sketch, "E276", {"start": v(-284.39, 2.75) * mm, "end": v(-286.3, 3.53) * mm});
            skLineSegment(sketch, "E277", {"start": v(-286.3, 3.53) * mm, "end": v(-288.16, 4.39) * mm});
            skLineSegment(sketch, "E278", {"start": v(-288.16, 4.39) * mm, "end": v(-288.44, 4.52) * mm});
            skLineSegment(sketch, "E279", {"start": v(-288.44, 4.52) * mm, "end": v(-288.72, 4.66) * mm});
            skLineSegment(sketch, "E280", {"start": v(-288.72, 4.66) * mm, "end": v(-289, 4.8) * mm});
            skLineSegment(sketch, "E281", {"start": v(-289, 4.8) * mm, "end": v(-289.29, 4.92) * mm});
            skLineSegment(sketch, "E282", {"start": v(-289.29, 4.92) * mm, "end": v(-289.57, 5.06) * mm});
            skLineSegment(sketch, "E283", {"start": v(-289.57, 5.06) * mm, "end": v(-289.85, 5.2) * mm});
            skLineSegment(sketch, "E284", {"start": v(-289.85, 5.2) * mm, "end": v(-290.12, 5.34) * mm});
            skLineSegment(sketch, "E285", {"start": v(-290.12, 5.34) * mm, "end": v(-290.4, 5.49) * mm});
            skLineSegment(sketch, "E286", {"start": v(-306.53, 15.84) * mm, "end": v(-306.68, 16.4) * mm});
            skLineSegment(sketch, "E287", {"start": v(-306.68, 16.4) * mm, "end": v(-307, 17.73) * mm});
            skLineSegment(sketch, "E288", {"start": v(-307, 17.73) * mm, "end": v(-307.46, 19.55) * mm});
            skLineSegment(sketch, "E289", {"start": v(-307.46, 19.55) * mm, "end": v(-307.98, 21.63) * mm});
            skLineSegment(sketch, "E290", {"start": v(-307.98, 21.63) * mm, "end": v(-308.5, 23.7) * mm});
            skLineSegment(sketch, "E291", {"start": v(-308.5, 23.7) * mm, "end": v(-308.96, 25.53) * mm});
            skLineSegment(sketch, "E292", {"start": v(-308.96, 25.53) * mm, "end": v(-309.28, 26.86) * mm});
            skLineSegment(sketch, "E293", {"start": v(-309.28, 26.86) * mm, "end": v(-309.42, 27.42) * mm});
            skLineSegment(sketch, "E294", {"start": v(-309.42, 27.42) * mm, "end": v(-310.57, 40.3) * mm});
            skLineSegment(sketch, "E295", {"start": v(-310.57, 40.3) * mm, "end": v(-309.59, 50.42) * mm});
            skLineSegment(sketch, "E296", {"start": v(-309.59, 50.42) * mm, "end": v(-307.05, 58.64) * mm});
            skLineSegment(sketch, "E297", {"start": v(-307.05, 58.64) * mm, "end": v(-303.57, 65.77) * mm});
            skLineSegment(sketch, "E298", {"start": v(-303.57, 65.77) * mm, "end": v(-299.72, 72.64) * mm});
            skLineSegment(sketch, "E299", {"start": v(-299.72, 72.64) * mm, "end": v(-296.13, 80.09) * mm});
            skLineSegment(sketch, "E300", {"start": v(-296.13, 80.09) * mm, "end": v(-293.37, 88.93) * mm});
            skLineSegment(sketch, "E301", {"start": v(-293.37, 88.93) * mm, "end": v(-292.04, 100.01) * mm});
            skLineSegment(sketch, "E302", {"start": v(-292.04, 100.01) * mm, "end": v(-292, 102.74) * mm});
            skLineSegment(sketch, "E303", {"start": v(-292, 102.74) * mm, "end": v(-292.52, 111.34) * mm});
            skLineSegment(sketch, "E304", {"start": v(-292.52, 111.34) * mm, "end": v(-293.92, 119) * mm});
            skLineSegment(sketch, "E305", {"start": v(-293.92, 119) * mm, "end": v(-295.93, 126.01) * mm});
            skLineSegment(sketch, "E306", {"start": v(-295.93, 126.01) * mm, "end": v(-298.3, 132.71) * mm});
            skLineSegment(sketch, "E307", {"start": v(-298.3, 132.71) * mm, "end": v(-300.77, 139.41) * mm});
            skLineSegment(sketch, "E308", {"start": v(-300.77, 139.41) * mm, "end": v(-303.08, 146.43) * mm});
            skLineSegment(sketch, "E309", {"start": v(-303.08, 146.43) * mm, "end": v(-304.98, 154.1) * mm});
            skLineSegment(sketch, "E310", {"start": v(-304.98, 154.1) * mm, "end": v(-306.2, 162.71) * mm});
            skLineSegment(sketch, "E311", {"start": v(-306.2, 162.71) * mm, "end": v(-306.24, 165.46) * mm});
            skLineSegment(sketch, "E312", {"start": v(-306.24, 165.46) * mm, "end": v(-305.88, 168.59) * mm});
            skLineSegment(sketch, "E313", {"start": v(-305.88, 168.59) * mm, "end": v(-305.11, 171.96) * mm});
            skLineSegment(sketch, "E314", {"start": v(-305.11, 171.96) * mm, "end": v(-303.91, 175.45) * mm});
            skLineSegment(sketch, "E315", {"start": v(-303.91, 175.45) * mm, "end": v(-302.26, 178.91) * mm});
            skLineSegment(sketch, "E316", {"start": v(-302.26, 178.91) * mm, "end": v(-300.12, 182.21) * mm});
            skLineSegment(sketch, "E317", {"start": v(-300.12, 182.21) * mm, "end": v(-297.48, 185.22) * mm});
            skLineSegment(sketch, "E318", {"start": v(-297.48, 185.22) * mm, "end": v(-294.32, 187.8) * mm});
            skLineSegment(sketch, "E319", {"start": v(-294.32, 187.8) * mm, "end": v(-292.3, 189.01) * mm});
            skLineSegment(sketch, "E320", {"start": v(-292.3, 189.01) * mm, "end": v(-290.1, 190.07) * mm});
            skLineSegment(sketch, "E321", {"start": v(-290.1, 190.07) * mm, "end": v(-287.72, 190.96) * mm});
            skLineSegment(sketch, "E322", {"start": v(-287.72, 190.96) * mm, "end": v(-285.16, 191.7) * mm});
            skLineSegment(sketch, "E323", {"start": v(-285.16, 191.7) * mm, "end": v(-282.4, 192.26) * mm});
            skLineSegment(sketch, "E324", {"start": v(-282.4, 192.26) * mm, "end": v(-279.47, 192.67) * mm});
            skLineSegment(sketch, "E325", {"start": v(-279.47, 192.67) * mm, "end": v(-276.36, 192.91) * mm});
            skLineSegment(sketch, "E326", {"start": v(-276.36, 192.91) * mm, "end": v(-273.08, 193) * mm});
            skLineSegment(sketch, "E327", {"start": v(-273.08, 193) * mm, "end": v(-269.75, 192.93) * mm});
            skLineSegment(sketch, "E328", {"start": v(-269.75, 192.93) * mm, "end": v(-266.24, 192.73) * mm});
            skLineSegment(sketch, "E329", {"start": v(-266.24, 192.73) * mm, "end": v(-262.58, 192.4) * mm});
            skLineSegment(sketch, "E330", {"start": v(-262.58, 192.4) * mm, "end": v(-258.77, 191.94) * mm});
            skLineSegment(sketch, "E331", {"start": v(-258.77, 191.94) * mm, "end": v(-254.82, 191.37) * mm});
            skLineSegment(sketch, "E332", {"start": v(-254.82, 191.37) * mm, "end": v(-250.75, 190.68) * mm});
            skLineSegment(sketch, "E333", {"start": v(-250.75, 190.68) * mm, "end": v(-246.57, 189.89) * mm});
            skLineSegment(sketch, "E334", {"start": v(-246.57, 189.89) * mm, "end": v(-242.3, 188.98) * mm});
            skLineSegment(sketch, "E335", {"start": v(-242.3, 188.98) * mm, "end": v(-240.24, 188.52) * mm});
            skLineSegment(sketch, "E336", {"start": v(-240.24, 188.52) * mm, "end": v(-238.16, 188.03) * mm});
            skLineSegment(sketch, "E337", {"start": v(-238.16, 188.03) * mm, "end": v(-236.07, 187.52) * mm});
            skLineSegment(sketch, "E338", {"start": v(-236.07, 187.52) * mm, "end": v(-233.96, 186.98) * mm});
            skLineSegment(sketch, "E339", {"start": v(-233.96, 186.98) * mm, "end": v(-231.84, 186.43) * mm});
            skLineSegment(sketch, "E340", {"start": v(-231.84, 186.43) * mm, "end": v(-229.7, 185.85) * mm});
            skLineSegment(sketch, "E341", {"start": v(-229.7, 185.85) * mm, "end": v(-227.55, 185.25) * mm});
            skLineSegment(sketch, "E342", {"start": v(-227.55, 185.25) * mm, "end": v(-225.4, 184.62) * mm});
            skLineSegment(sketch, "E343", {"start": v(-225.4, 184.62) * mm, "end": v(-220.86, 183.25) * mm});
            skLineSegment(sketch, "E344", {"start": v(-220.86, 183.25) * mm, "end": v(-216.3, 181.8) * mm});
            skLineSegment(sketch, "E345", {"start": v(-216.3, 181.8) * mm, "end": v(-211.72, 180.26) * mm});
            skLineSegment(sketch, "E346", {"start": v(-211.72, 180.26) * mm, "end": v(-207.12, 178.63) * mm});
            skLineSegment(sketch, "E347", {"start": v(-207.12, 178.63) * mm, "end": v(-202.53, 176.93) * mm});
            skLineSegment(sketch, "E348", {"start": v(-202.53, 176.93) * mm, "end": v(-197.95, 175.14) * mm});
            skLineSegment(sketch, "E349", {"start": v(-197.95, 175.14) * mm, "end": v(-193.4, 173.28) * mm});
            skLineSegment(sketch, "E350", {"start": v(-193.4, 173.28) * mm, "end": v(-188.88, 171.34) * mm});
            skLineSegment(sketch, "E351", {"start": v(-188.88, 171.34) * mm, "end": v(-184.98, 169.6) * mm});
            skLineSegment(sketch, "E352", {"start": v(-184.98, 169.6) * mm, "end": v(-181.2, 167.8) * mm});
            skLineSegment(sketch, "E353", {"start": v(-181.2, 167.8) * mm, "end": v(-177.52, 165.97) * mm});
            skLineSegment(sketch, "E354", {"start": v(-177.52, 165.97) * mm, "end": v(-173.94, 164.1) * mm});
            skLineSegment(sketch, "E355", {"start": v(-173.94, 164.1) * mm, "end": v(-170.45, 162.2) * mm});
            skLineSegment(sketch, "E356", {"start": v(-170.45, 162.2) * mm, "end": v(-167.06, 160.27) * mm});
            skLineSegment(sketch, "E357", {"start": v(-167.06, 160.27) * mm, "end": v(-163.76, 158.31) * mm});
            skLineSegment(sketch, "E358", {"start": v(-163.76, 158.31) * mm, "end": v(-160.54, 156.34) * mm});
            skLineSegment(sketch, "E359", {"start": v(-160.54, 156.34) * mm, "end": v(-152.97, 151.4) * mm});
            skLineSegment(sketch, "E360", {"start": v(-152.97, 151.4) * mm, "end": v(-145.57, 146.12) * mm});
            skLineSegment(sketch, "E361", {"start": v(-145.57, 146.12) * mm, "end": v(-138.4, 140.54) * mm});
            skLineSegment(sketch, "E362", {"start": v(-138.4, 140.54) * mm, "end": v(-131.47, 134.65) * mm});
            skLineSegment(sketch, "E363", {"start": v(-131.47, 134.65) * mm, "end": v(-124.82, 128.47) * mm});
            skLineSegment(sketch, "E364", {"start": v(-124.82, 128.47) * mm, "end": v(-118.48, 122) * mm});
            skLineSegment(sketch, "E365", {"start": v(-118.48, 122) * mm, "end": v(-112.47, 115.28) * mm});
            skLineSegment(sketch, "E366", {"start": v(-112.47, 115.28) * mm, "end": v(-106.84, 108.29) * mm});
            skLineSegment(sketch, "E367", {"start": v(-106.84, 108.29) * mm, "end": v(-110.55, 104.18) * mm});
            skLineSegment(sketch, "E368", {"start": v(-110.55, 104.18) * mm, "end": v(-113.25, 100.01) * mm});
            skLineSegment(sketch, "E369", {"start": v(-113.25, 100.01) * mm, "end": v(-115.08, 95.84) * mm});
            skLineSegment(sketch, "E370", {"start": v(-115.08, 95.84) * mm, "end": v(-116.21, 91.73) * mm});
            skLineSegment(sketch, "E371", {"start": v(-116.21, 91.73) * mm, "end": v(-116.81, 87.74) * mm});
            skLineSegment(sketch, "E372", {"start": v(-116.81, 87.74) * mm, "end": v(-117.04, 83.94) * mm});
            skLineSegment(sketch, "E373", {"start": v(-117.04, 83.94) * mm, "end": v(-117.05, 80.4) * mm});
            skLineSegment(sketch, "E374", {"start": v(-117.05, 80.4) * mm, "end": v(-117.02, 77.17) * mm});
            skLineSegment(sketch, "E375", {"start": v(-117.02, 77.17) * mm, "end": v(-131.44, 80.6) * mm});
            skLineSegment(sketch, "E376", {"start": v(-131.44, 80.6) * mm, "end": v(-144.77, 83.65) * mm});
            skLineSegment(sketch, "E377", {"start": v(-144.77, 83.65) * mm, "end": v(-156.78, 86.26) * mm});
            skLineSegment(sketch, "E378", {"start": v(-156.78, 86.26) * mm, "end": v(-167.21, 88.37) * mm});
            skLineSegment(sketch, "E379", {"start": v(-167.21, 88.37) * mm, "end": v(-175.8, 89.95) * mm});
            skLineSegment(sketch, "E380", {"start": v(-175.8, 89.95) * mm, "end": v(-182.31, 90.92) * mm});
            skLineSegment(sketch, "E381", {"start": v(-182.31, 90.92) * mm, "end": v(-186.47, 91.26) * mm});
            skLineSegment(sketch, "E382", {"start": v(-186.47, 91.26) * mm, "end": v(-188.04, 90.9) * mm});
            skLineSegment(sketch, "E383", {"start": v(-188.04, 90.9) * mm, "end": v(-186.79, 89.82) * mm});
            skLineSegment(sketch, "E384", {"start": v(-186.79, 89.82) * mm, "end": v(-182.84, 88.1) * mm});
            skLineSegment(sketch, "E385", {"start": v(-182.84, 88.1) * mm, "end": v(-176.45, 85.85) * mm});
            skLineSegment(sketch, "E386", {"start": v(-176.45, 85.85) * mm, "end": v(-167.88, 83.13) * mm});
            skLineSegment(sketch, "E387", {"start": v(-167.88, 83.13) * mm, "end": v(-157.4, 80) * mm});
            skLineSegment(sketch, "E388", {"start": v(-157.4, 80) * mm, "end": v(-145.25, 76.57) * mm});
            skLineSegment(sketch, "E389", {"start": v(-145.25, 76.57) * mm, "end": v(-131.7, 72.9) * mm});
            skLineSegment(sketch, "E390", {"start": v(-131.7, 72.9) * mm, "end": v(-117.02, 69.08) * mm});
            skLineSegment(sketch, "E391", {"start": v(-117.02, 69.08) * mm, "end": v(-117.07, 55.85) * mm});
            skLineSegment(sketch, "E392", {"start": v(-117.07, 55.85) * mm, "end": v(-117.15, 45.33) * mm});
            skLineSegment(sketch, "E393", {"start": v(-117.15, 45.33) * mm, "end": v(-117.17, 37.07) * mm});
            skLineSegment(sketch, "E394", {"start": v(-117.17, 37.07) * mm, "end": v(-117.02, 30.63) * mm});
            skLineSegment(sketch, "E395", {"start": v(-117.02, 30.63) * mm, "end": v(-116.62, 25.57) * mm});
            skLineSegment(sketch, "E396", {"start": v(-116.62, 25.57) * mm, "end": v(-115.85, 21.45) * mm});
            skLineSegment(sketch, "E397", {"start": v(-115.85, 21.45) * mm, "end": v(-114.64, 17.83) * mm});
            skLineSegment(sketch, "E398", {"start": v(-114.64, 17.83) * mm, "end": v(-112.87, 14.25) * mm});
            skLineSegment(sketch, "E399", {"start": v(-112.87, 14.25) * mm, "end": v(-114.49, 15.03) * mm});
            skLineSegment(sketch, "E400", {"start": v(-114.49, 15.03) * mm, "end": v(-116.1, 15.79) * mm});
            skLineSegment(sketch, "E401", {"start": v(-116.1, 15.79) * mm, "end": v(-117.7, 16.52) * mm});
            skLineSegment(sketch, "E402", {"start": v(-117.7, 16.52) * mm, "end": v(-119.3, 17.24) * mm});
            skLineSegment(sketch, "E403", {"start": v(-119.3, 17.24) * mm, "end": v(-120.9, 17.94) * mm});
            skLineSegment(sketch, "E404", {"start": v(-120.9, 17.94) * mm, "end": v(-122.48, 18.64) * mm});
            skLineSegment(sketch, "E405", {"start": v(-122.48, 18.64) * mm, "end": v(-124.07, 19.32) * mm});
            skLineSegment(sketch, "E406", {"start": v(-124.07, 19.32) * mm, "end": v(-125.65, 20.01) * mm});
            skLineSegment(sketch, "E407", {"start": v(-125.65, 20.01) * mm, "end": v(-151.3, 29.76) * mm});
            skLineSegment(sketch, "E408", {"start": v(-151.3, 29.76) * mm, "end": v(-176.19, 36.7) * mm});
            skLineSegment(sketch, "E409", {"start": v(-176.19, 36.7) * mm, "end": v(-199.87, 41.15) * mm});
            skLineSegment(sketch, "E410", {"start": v(-199.87, 41.15) * mm, "end": v(-221.96, 43.42) * mm});
            skLineSegment(sketch, "E411", {"start": v(-221.96, 43.42) * mm, "end": v(-242.03, 43.81) * mm});
            skLineSegment(sketch, "E412", {"start": v(-242.03, 43.81) * mm, "end": v(-259.67, 42.65) * mm});
            skLineSegment(sketch, "E413", {"start": v(-259.67, 42.65) * mm, "end": v(-274.46, 40.25) * mm});
            skLineSegment(sketch, "E414", {"start": v(-274.46, 40.25) * mm, "end": v(-286, 36.92) * mm});
            skLineSegment(sketch, "E415", {"start": v(-286, 36.92) * mm, "end": v(-290, 35.17) * mm});
            skLineSegment(sketch, "E416", {"start": v(-290, 35.17) * mm, "end": v(-293.28, 33.22) * mm});
            skLineSegment(sketch, "E417", {"start": v(-293.28, 33.22) * mm, "end": v(-296, 31.06) * mm});
            skLineSegment(sketch, "E418", {"start": v(-296, 31.06) * mm, "end": v(-298.3, 28.64) * mm});
            skLineSegment(sketch, "E419", {"start": v(-298.3, 28.64) * mm, "end": v(-300.34, 25.94) * mm});
            skLineSegment(sketch, "E420", {"start": v(-300.34, 25.94) * mm, "end": v(-302.3, 22.93) * mm});
            skLineSegment(sketch, "E421", {"start": v(-302.3, 22.93) * mm, "end": v(-304.3, 19.57) * mm});
            skLineSegment(sketch, "E422", {"start": v(-304.3, 19.57) * mm, "end": v(-306.53, 15.84) * mm});
            skLineSegment(sketch, "E423", {"start": v(-218.88, 196.34) * mm, "end": v(-217.98, 197.85) * mm});
            skLineSegment(sketch, "E424", {"start": v(-217.98, 197.85) * mm, "end": v(-217.1, 199.36) * mm});
            skLineSegment(sketch, "E425", {"start": v(-217.1, 199.36) * mm, "end": v(-216.2, 200.84) * mm});
            skLineSegment(sketch, "E426", {"start": v(-216.2, 200.84) * mm, "end": v(-215.3, 202.32) * mm});
            skLineSegment(sketch, "E427", {"start": v(-215.3, 202.32) * mm, "end": v(-214.41, 203.8) * mm});
            skLineSegment(sketch, "E428", {"start": v(-214.41, 203.8) * mm, "end": v(-213.52, 205.25) * mm});
            skLineSegment(sketch, "E429", {"start": v(-213.52, 205.25) * mm, "end": v(-212.63, 206.7) * mm});
            skLineSegment(sketch, "E430", {"start": v(-212.63, 206.7) * mm, "end": v(-211.74, 208.12) * mm});
            skLineSegment(sketch, "E431", {"start": v(-211.74, 208.12) * mm, "end": v(-202.32, 209.66) * mm});
            skLineSegment(sketch, "E432", {"start": v(-202.32, 209.66) * mm, "end": v(-192.91, 211.26) * mm});
            skLineSegment(sketch, "E433", {"start": v(-192.91, 211.26) * mm, "end": v(-183.52, 212.94) * mm});
            skLineSegment(sketch, "E434", {"start": v(-183.52, 212.94) * mm, "end": v(-174.15, 214.68) * mm});
            skLineSegment(sketch, "E435", {"start": v(-174.15, 214.68) * mm, "end": v(-164.8, 216.49) * mm});
            skLineSegment(sketch, "E436", {"start": v(-164.8, 216.49) * mm, "end": v(-155.48, 218.36) * mm});
            skLineSegment(sketch, "E437", {"start": v(-155.48, 218.36) * mm, "end": v(-146.18, 220.28) * mm});
            skLineSegment(sketch, "E438", {"start": v(-146.18, 220.28) * mm, "end": v(-136.9, 222.27) * mm});
            skLineSegment(sketch, "E439", {"start": v(-136.9, 222.27) * mm, "end": v(-114.6, 227.34) * mm});
            skLineSegment(sketch, "E440", {"start": v(-114.6, 227.34) * mm, "end": v(-92.28, 232.9) * mm});
            skLineSegment(sketch, "E441", {"start": v(-92.28, 232.9) * mm, "end": v(-69.97, 239) * mm});
            skLineSegment(sketch, "E442", {"start": v(-69.97, 239) * mm, "end": v(-47.77, 245.69) * mm});
            skLineSegment(sketch, "E443", {"start": v(-47.77, 245.69) * mm, "end": v(-25.73, 253) * mm});
            skLineSegment(sketch, "E444", {"start": v(-25.73, 253) * mm, "end": v(-3.92, 261) * mm});
            skLineSegment(sketch, "E445", {"start": v(-3.92, 261) * mm, "end": v(17.58, 269.73) * mm});
            skLineSegment(sketch, "E446", {"start": v(17.58, 269.73) * mm, "end": v(38.7, 279.22) * mm});
            skLineSegment(sketch, "E447", {"start": v(38.7, 279.22) * mm, "end": v(43.87, 274.15) * mm});
            skLineSegment(sketch, "E448", {"start": v(43.87, 274.15) * mm, "end": v(49, 268.86) * mm});
            skLineSegment(sketch, "E449", {"start": v(49, 268.86) * mm, "end": v(54.09, 263.34) * mm});
            skLineSegment(sketch, "E450", {"start": v(54.09, 263.34) * mm, "end": v(59.14, 257.6) * mm});
            skLineSegment(sketch, "E451", {"start": v(59.14, 257.6) * mm, "end": v(64.15, 251.63) * mm});
            skLineSegment(sketch, "E452", {"start": v(64.15, 251.63) * mm, "end": v(69.13, 245.44) * mm});
            skLineSegment(sketch, "E453", {"start": v(69.13, 245.44) * mm, "end": v(74.07, 239.03) * mm});
            skLineSegment(sketch, "E454", {"start": v(74.07, 239.03) * mm, "end": v(78.96, 232.4) * mm});
            skLineSegment(sketch, "E455", {"start": v(78.96, 232.4) * mm, "end": v(52.93, 218.32) * mm});
            skLineSegment(sketch, "E456", {"start": v(52.93, 218.32) * mm, "end": v(25.9, 205.94) * mm});
            skLineSegment(sketch, "E457", {"start": v(25.9, 205.94) * mm, "end": v(-1.9, 195.1) * mm});
            skLineSegment(sketch, "E458", {"start": v(-1.9, 195.1) * mm, "end": v(-30.31, 185.65) * mm});
            skLineSegment(sketch, "E459", {"start": v(-30.31, 185.65) * mm, "end": v(-59.12, 177.45) * mm});
            skLineSegment(sketch, "E460", {"start": v(-59.12, 177.45) * mm, "end": v(-88.13, 170.34) * mm});
            skLineSegment(sketch, "E461", {"start": v(-88.13, 170.34) * mm, "end": v(-117.14, 164.18) * mm});
            skLineSegment(sketch, "E462", {"start": v(-117.14, 164.18) * mm, "end": v(-145.97, 158.8) * mm});
            skLineSegment(sketch, "E463", {"start": v(-145.97, 158.8) * mm, "end": v(-150.19, 161.67) * mm});
            skLineSegment(sketch, "E464", {"start": v(-150.19, 161.67) * mm, "end": v(-154.58, 164.52) * mm});
            skLineSegment(sketch, "E465", {"start": v(-154.58, 164.52) * mm, "end": v(-159.16, 167.33) * mm});
            skLineSegment(sketch, "E466", {"start": v(-159.16, 167.33) * mm, "end": v(-163.91, 170.1) * mm});
            skLineSegment(sketch, "E467", {"start": v(-163.91, 170.1) * mm, "end": v(-168.85, 172.83) * mm});
            skLineSegment(sketch, "E468", {"start": v(-168.85, 172.83) * mm, "end": v(-173.98, 175.48) * mm});
            skLineSegment(sketch, "E469", {"start": v(-173.98, 175.48) * mm, "end": v(-179.3, 178.06) * mm});
            skLineSegment(sketch, "E470", {"start": v(-179.3, 178.06) * mm, "end": v(-184.83, 180.56) * mm});
            skLineSegment(sketch, "E471", {"start": v(-184.83, 180.56) * mm, "end": v(-189.03, 182.37) * mm});
            skLineSegment(sketch, "E472", {"start": v(-189.03, 182.37) * mm, "end": v(-193.33, 184.15) * mm});
            skLineSegment(sketch, "E473", {"start": v(-193.33, 184.15) * mm, "end": v(-197.7, 185.89) * mm});
            skLineSegment(sketch, "E474", {"start": v(-197.7, 185.89) * mm, "end": v(-202.13, 187.58) * mm});
            skLineSegment(sketch, "E475", {"start": v(-202.13, 187.58) * mm, "end": v(-206.62, 189.22) * mm});
            skLineSegment(sketch, "E476", {"start": v(-206.62, 189.22) * mm, "end": v(-211.16, 190.8) * mm});
            skLineSegment(sketch, "E477", {"start": v(-211.16, 190.8) * mm, "end": v(-215.73, 192.3) * mm});
            skLineSegment(sketch, "E478", {"start": v(-215.73, 192.3) * mm, "end": v(-220.32, 193.75) * mm});
            skLineSegment(sketch, "E479", {"start": v(-220.32, 193.75) * mm, "end": v(-220.13, 194.07) * mm});
            skLineSegment(sketch, "E480", {"start": v(-220.13, 194.07) * mm, "end": v(-219.95, 194.4) * mm});
            skLineSegment(sketch, "E481", {"start": v(-219.95, 194.4) * mm, "end": v(-219.78, 194.72) * mm});
            skLineSegment(sketch, "E482", {"start": v(-219.78, 194.72) * mm, "end": v(-219.6, 195.05) * mm});
            skLineSegment(sketch, "E483", {"start": v(-219.6, 195.05) * mm, "end": v(-219.42, 195.38) * mm});
            skLineSegment(sketch, "E484", {"start": v(-219.42, 195.38) * mm, "end": v(-219.24, 195.7) * mm});
            skLineSegment(sketch, "E485", {"start": v(-219.24, 195.7) * mm, "end": v(-219.06, 196.02) * mm});
            skLineSegment(sketch, "E486", {"start": v(-219.06, 196.02) * mm, "end": v(-218.88, 196.34) * mm});
            skLineSegment(sketch, "E487", {"start": v(-60.79, 329.23) * mm, "end": v(-60.34, 329.2) * mm});
            skLineSegment(sketch, "E488", {"start": v(-60.34, 329.2) * mm, "end": v(-59.94, 329.2) * mm});
            skLineSegment(sketch, "E489", {"start": v(-59.94, 329.2) * mm, "end": v(-59.58, 329.19) * mm});
            skLineSegment(sketch, "E490", {"start": v(-59.58, 329.19) * mm, "end": v(-59.24, 329.19) * mm});
            skLineSegment(sketch, "E491", {"start": v(-59.24, 329.19) * mm, "end": v(-58.87, 329.2) * mm});
            skLineSegment(sketch, "E492", {"start": v(-58.87, 329.2) * mm, "end": v(-58.47, 329.2) * mm});
            skLineSegment(sketch, "E493", {"start": v(-58.47, 329.2) * mm, "end": v(-58, 329.23) * mm});
            skLineSegment(sketch, "E494", {"start": v(-58, 329.23) * mm, "end": v(-57.44, 329.24) * mm});
            skLineSegment(sketch, "E495", {"start": v(-57.44, 329.24) * mm, "end": v(-57.41, 329.24) * mm});
            skLineSegment(sketch, "E496", {"start": v(-57.41, 329.24) * mm, "end": v(-54.73, 329.16) * mm});
            skLineSegment(sketch, "E497", {"start": v(-54.73, 329.16) * mm, "end": v(-50.77, 328.8) * mm});
            skLineSegment(sketch, "E498", {"start": v(-50.77, 328.8) * mm, "end": v(-45.62, 328) * mm});
            skLineSegment(sketch, "E499", {"start": v(-45.62, 328) * mm, "end": v(-39.33, 326.61) * mm});
            skLineSegment(sketch, "E500", {"start": v(-39.33, 326.61) * mm, "end": v(-31.99, 324.47) * mm});
            skLineSegment(sketch, "E501", {"start": v(-31.99, 324.47) * mm, "end": v(-23.65, 321.42) * mm});
            skLineSegment(sketch, "E502", {"start": v(-23.65, 321.42) * mm, "end": v(-14.4, 317.3) * mm});
            skLineSegment(sketch, "E503", {"start": v(-14.4, 317.3) * mm, "end": v(-4.3, 311.96) * mm});
            skLineSegment(sketch, "E504", {"start": v(-4.3, 311.96) * mm, "end": v(-3.18, 311.3) * mm});
            skLineSegment(sketch, "E505", {"start": v(-3.18, 311.3) * mm, "end": v(-2.07, 310.64) * mm});
            skLineSegment(sketch, "E506", {"start": v(-2.07, 310.64) * mm, "end": v(-0.96, 309.94) * mm});
            skLineSegment(sketch, "E507", {"start": v(-0.96, 309.94) * mm, "end": v(0.15, 309.24) * mm});
            skLineSegment(sketch, "E508", {"start": v(0.15, 309.24) * mm, "end": v(1.25, 308.52) * mm});
            skLineSegment(sketch, "E509", {"start": v(1.25, 308.52) * mm, "end": v(2.36, 307.8) * mm});
            skLineSegment(sketch, "E510", {"start": v(2.36, 307.8) * mm, "end": v(3.46, 307.08) * mm});
            skLineSegment(sketch, "E511", {"start": v(3.46, 307.08) * mm, "end": v(4.57, 306.36) * mm});
            skLineSegment(sketch, "E512", {"start": v(4.57, 306.36) * mm, "end": v(-13.93, 298.82) * mm});
            skLineSegment(sketch, "E513", {"start": v(-13.93, 298.82) * mm, "end": v(-32.68, 291.86) * mm});
            skLineSegment(sketch, "E514", {"start": v(-32.68, 291.86) * mm, "end": v(-51.63, 285.44) * mm});
            skLineSegment(sketch, "E515", {"start": v(-51.63, 285.44) * mm, "end": v(-70.72, 279.52) * mm});
            skLineSegment(sketch, "E516", {"start": v(-70.72, 279.52) * mm, "end": v(-89.89, 274.06) * mm});
            skLineSegment(sketch, "E517", {"start": v(-89.89, 274.06) * mm, "end": v(-109.08, 269.01) * mm});
            skLineSegment(sketch, "E518", {"start": v(-109.08, 269.01) * mm, "end": v(-128.24, 264.34) * mm});
            skLineSegment(sketch, "E519", {"start": v(-128.24, 264.34) * mm, "end": v(-147.3, 260) * mm});
            skLineSegment(sketch, "E520", {"start": v(-147.3, 260) * mm, "end": v(-151.35, 259.12) * mm});
            skLineSegment(sketch, "E521", {"start": v(-151.35, 259.12) * mm, "end": v(-155.39, 258.25) * mm});
            skLineSegment(sketch, "E522", {"start": v(-155.39, 258.25) * mm, "end": v(-159.41, 257.4) * mm});
            skLineSegment(sketch, "E523", {"start": v(-159.41, 257.4) * mm, "end": v(-163.43, 256.56) * mm});
            skLineSegment(sketch, "E524", {"start": v(-163.43, 256.56) * mm, "end": v(-167.43, 255.74) * mm});
            skLineSegment(sketch, "E525", {"start": v(-167.43, 255.74) * mm, "end": v(-171.43, 254.93) * mm});
            skLineSegment(sketch, "E526", {"start": v(-171.43, 254.93) * mm, "end": v(-175.42, 254.13) * mm});
            skLineSegment(sketch, "E527", {"start": v(-175.42, 254.13) * mm, "end": v(-179.4, 253.34) * mm});
            skLineSegment(sketch, "E528", {"start": v(-179.4, 253.34) * mm, "end": v(-157.29, 277.55) * mm});
            skLineSegment(sketch, "E529", {"start": v(-157.29, 277.55) * mm, "end": v(-136.4, 295.98) * mm});
            skLineSegment(sketch, "E530", {"start": v(-136.4, 295.98) * mm, "end": v(-117.18, 309.41) * mm});
            skLineSegment(sketch, "E531", {"start": v(-117.18, 309.41) * mm, "end": v(-100.04, 318.64) * mm});
            skLineSegment(sketch, "E532", {"start": v(-100.04, 318.64) * mm, "end": v(-85.4, 324.44) * mm});
            skLineSegment(sketch, "E533", {"start": v(-85.4, 324.44) * mm, "end": v(-73.7, 327.62) * mm});
            skLineSegment(sketch, "E534", {"start": v(-73.7, 327.62) * mm, "end": v(-65.36, 328.95) * mm});
            skLineSegment(sketch, "E535", {"start": v(-65.36, 328.95) * mm, "end": v(-60.79, 329.23) * mm});
            skLineSegment(sketch, "E536", {"start": v(100.28, 200.26) * mm, "end": v(100.58, 199.76) * mm});
            skLineSegment(sketch, "E537", {"start": v(100.58, 199.76) * mm, "end": v(101.03, 199.01) * mm});
            skLineSegment(sketch, "E538", {"start": v(101.03, 199.01) * mm, "end": v(101.56, 198.11) * mm});
            skLineSegment(sketch, "E539", {"start": v(101.56, 198.11) * mm, "end": v(102.15, 197.13) * mm});
            skLineSegment(sketch, "E540", {"start": v(102.15, 197.13) * mm, "end": v(102.74, 196.13) * mm});
            skLineSegment(sketch, "E541", {"start": v(102.74, 196.13) * mm, "end": v(103.3, 195.2) * mm});
            skLineSegment(sketch, "E542", {"start": v(103.3, 195.2) * mm, "end": v(103.77, 194.4) * mm});
            skLineSegment(sketch, "E543", {"start": v(103.77, 194.4) * mm, "end": v(104.1, 193.82) * mm});
            skLineSegment(sketch, "E544", {"start": v(104.1, 193.82) * mm, "end": v(88.87, 188.43) * mm});
            skLineSegment(sketch, "E545", {"start": v(88.87, 188.43) * mm, "end": v(74.14, 182.46) * mm});
            skLineSegment(sketch, "E546", {"start": v(74.14, 182.46) * mm, "end": v(59.92, 175.81) * mm});
            skLineSegment(sketch, "E547", {"start": v(59.92, 175.81) * mm, "end": v(46.23, 168.4) * mm});
            skLineSegment(sketch, "E548", {"start": v(46.23, 168.4) * mm, "end": v(33.08, 160.17) * mm});
            skLineSegment(sketch, "E549", {"start": v(33.08, 160.17) * mm, "end": v(20.49, 151.02) * mm});
            skLineSegment(sketch, "E550", {"start": v(20.49, 151.02) * mm, "end": v(8.47, 140.86) * mm});
            skLineSegment(sketch, "E551", {"start": v(8.47, 140.86) * mm, "end": v(-2.97, 129.63) * mm});
            skLineSegment(sketch, "E552", {"start": v(-2.97, 129.63) * mm, "end": v(-4.3, 128.21) * mm});
            skLineSegment(sketch, "E553", {"start": v(-4.3, 128.21) * mm, "end": v(-5.6, 126.78) * mm});
            skLineSegment(sketch, "E554", {"start": v(-5.6, 126.78) * mm, "end": v(-6.9, 125.32) * mm});
            skLineSegment(sketch, "E555", {"start": v(-6.9, 125.32) * mm, "end": v(-8.17, 123.85) * mm});
            skLineSegment(sketch, "E556", {"start": v(-8.17, 123.85) * mm, "end": v(-9.44, 122.36) * mm});
            skLineSegment(sketch, "E557", {"start": v(-9.44, 122.36) * mm, "end": v(-10.7, 120.85) * mm});
            skLineSegment(sketch, "E558", {"start": v(-10.7, 120.85) * mm, "end": v(-11.95, 119.33) * mm});
            skLineSegment(sketch, "E559", {"start": v(-11.95, 119.33) * mm, "end": v(-13.19, 117.8) * mm});
            skLineSegment(sketch, "E560", {"start": v(-13.19, 117.8) * mm, "end": v(-15.36, 118.89) * mm});
            skLineSegment(sketch, "E561", {"start": v(-15.36, 118.89) * mm, "end": v(-17.6, 119.85) * mm});
            skLineSegment(sketch, "E562", {"start": v(-17.6, 119.85) * mm, "end": v(-19.91, 120.68) * mm});
            skLineSegment(sketch, "E563", {"start": v(-19.91, 120.68) * mm, "end": v(-22.28, 121.36) * mm});
            skLineSegment(sketch, "E564", {"start": v(-22.28, 121.36) * mm, "end": v(-24.71, 121.9) * mm});
            skLineSegment(sketch, "E565", {"start": v(-24.71, 121.9) * mm, "end": v(-27.2, 122.3) * mm});
            skLineSegment(sketch, "E566", {"start": v(-27.2, 122.3) * mm, "end": v(-29.72, 122.54) * mm});
            skLineSegment(sketch, "E567", {"start": v(-29.72, 122.54) * mm, "end": v(-32.3, 122.63) * mm});
            skLineSegment(sketch, "E568", {"start": v(-32.3, 122.63) * mm, "end": v(-50.12, 122.68) * mm});
            skLineSegment(sketch, "E569", {"start": v(-50.12, 122.68) * mm, "end": v(-64, 122.75) * mm});
            skLineSegment(sketch, "E570", {"start": v(-64, 122.75) * mm, "end": v(-74.62, 122.75) * mm});
            skLineSegment(sketch, "E571", {"start": v(-74.62, 122.75) * mm, "end": v(-82.61, 122.55) * mm});
            skLineSegment(sketch, "E572", {"start": v(-82.61, 122.55) * mm, "end": v(-88.65, 122.07) * mm});
            skLineSegment(sketch, "E573", {"start": v(-88.65, 122.07) * mm, "end": v(-93.38, 121.19) * mm});
            skLineSegment(sketch, "E574", {"start": v(-93.38, 121.19) * mm, "end": v(-97.47, 119.8) * mm});
            skLineSegment(sketch, "E575", {"start": v(-97.47, 119.8) * mm, "end": v(-101.57, 117.8) * mm});
            skLineSegment(sketch, "E576", {"start": v(-101.57, 117.8) * mm, "end": v(-102.44, 118.86) * mm});
            skLineSegment(sketch, "E577", {"start": v(-102.44, 118.86) * mm, "end": v(-103.3, 119.9) * mm});
            skLineSegment(sketch, "E578", {"start": v(-103.3, 119.9) * mm, "end": v(-104.2, 120.94) * mm});
            skLineSegment(sketch, "E579", {"start": v(-104.2, 120.94) * mm, "end": v(-105.08, 121.97) * mm});
            skLineSegment(sketch, "E580", {"start": v(-105.08, 121.97) * mm, "end": v(-105.98, 123) * mm});
            skLineSegment(sketch, "E581", {"start": v(-105.98, 123) * mm, "end": v(-106.88, 124) * mm});
            skLineSegment(sketch, "E582", {"start": v(-106.88, 124) * mm, "end": v(-107.78, 125.02) * mm});
            skLineSegment(sketch, "E583", {"start": v(-107.78, 125.02) * mm, "end": v(-108.69, 126.04) * mm});
            skLineSegment(sketch, "E584", {"start": v(-108.69, 126.04) * mm, "end": v(-81.5, 131.81) * mm});
            skLineSegment(sketch, "E585", {"start": v(-81.5, 131.81) * mm, "end": v(-54.4, 138.42) * mm});
            skLineSegment(sketch, "E586", {"start": v(-54.4, 138.42) * mm, "end": v(-27.5, 145.93) * mm});
            skLineSegment(sketch, "E587", {"start": v(-27.5, 145.93) * mm, "end": v(-0.9, 154.45) * mm});
            skLineSegment(sketch, "E588", {"start": v(-0.9, 154.45) * mm, "end": v(25.3, 164.05) * mm});
            skLineSegment(sketch, "E589", {"start": v(25.3, 164.05) * mm, "end": v(50.96, 174.83) * mm});
            skLineSegment(sketch, "E590", {"start": v(50.96, 174.83) * mm, "end": v(75.99, 186.87) * mm});
            skLineSegment(sketch, "E591", {"start": v(75.99, 186.87) * mm, "end": v(100.28, 200.26) * mm});
            skLineSegment(sketch, "E592", {"start": v(-52.5, -8.32) * mm, "end": v(-50.27, -11.34) * mm});
            skLineSegment(sketch, "E593", {"start": v(-50.27, -11.34) * mm, "end": v(-47.92, -14.46) * mm});
            skLineSegment(sketch, "E594", {"start": v(-47.92, -14.46) * mm, "end": v(-45.46, -17.69) * mm});
            skLineSegment(sketch, "E595", {"start": v(-45.46, -17.69) * mm, "end": v(-42.88, -21.01) * mm});
            skLineSegment(sketch, "E596", {"start": v(-42.88, -21.01) * mm, "end": v(-40.2, -24.44) * mm});
            skLineSegment(sketch, "E597", {"start": v(-40.2, -24.44) * mm, "end": v(-37.4, -27.95) * mm});
            skLineSegment(sketch, "E598", {"start": v(-37.4, -27.95) * mm, "end": v(-34.5, -31.54) * mm});
            skLineSegment(sketch, "E599", {"start": v(-34.5, -31.54) * mm, "end": v(-31.5, -35.2) * mm});
            skLineSegment(sketch, "E600", {"start": v(-31.5, -35.2) * mm, "end": v(-39.07, -36.75) * mm});
            skLineSegment(sketch, "E601", {"start": v(-39.07, -36.75) * mm, "end": v(-46.65, -38.22) * mm});
            skLineSegment(sketch, "E602", {"start": v(-46.65, -38.22) * mm, "end": v(-54.23, -39.62) * mm});
            skLineSegment(sketch, "E603", {"start": v(-54.23, -39.62) * mm, "end": v(-61.82, -40.97) * mm});
            skLineSegment(sketch, "E604", {"start": v(-61.82, -40.97) * mm, "end": v(-69.4, -42.25) * mm});
            skLineSegment(sketch, "E605", {"start": v(-69.4, -42.25) * mm, "end": v(-77, -43.47) * mm});
            skLineSegment(sketch, "E606", {"start": v(-77, -43.47) * mm, "end": v(-84.58, -44.63) * mm});
            skLineSegment(sketch, "E607", {"start": v(-84.58, -44.63) * mm, "end": v(-92.16, -45.74) * mm});
            skLineSegment(sketch, "E608", {"start": v(-92.16, -45.74) * mm, "end": v(-87.73, -40.55) * mm});
            skLineSegment(sketch, "E609", {"start": v(-87.73, -40.55) * mm, "end": v(-83.49, -35.48) * mm});
            skLineSegment(sketch, "E610", {"start": v(-83.49, -35.48) * mm, "end": v(-79.45, -30.55) * mm});
            skLineSegment(sketch, "E611", {"start": v(-79.45, -30.55) * mm, "end": v(-75.6, -25.76) * mm});
            skLineSegment(sketch, "E612", {"start": v(-75.6, -25.76) * mm, "end": v(-71.96, -21.13) * mm});
            skLineSegment(sketch, "E613", {"start": v(-71.96, -21.13) * mm, "end": v(-68.52, -16.68) * mm});
            skLineSegment(sketch, "E614", {"start": v(-68.52, -16.68) * mm, "end": v(-65.29, -12.4) * mm});
            skLineSegment(sketch, "E615", {"start": v(-65.29, -12.4) * mm, "end": v(-62.26, -8.32) * mm});
            skLineSegment(sketch, "E616", {"start": v(-62.26, -8.32) * mm, "end": v(-62.2, -8.26) * mm});
            skLineSegment(sketch, "E617", {"start": v(-62.2, -8.26) * mm, "end": v(-62.17, -8.2) * mm});
            skLineSegment(sketch, "E618", {"start": v(-62.17, -8.2) * mm, "end": v(-62.12, -8.13) * mm});
            skLineSegment(sketch, "E619", {"start": v(-62.12, -8.13) * mm, "end": v(-62.08, -8.06) * mm});
            skLineSegment(sketch, "E620", {"start": v(-62.08, -8.06) * mm, "end": v(-62.04, -8) * mm});
            skLineSegment(sketch, "E621", {"start": v(-62.04, -8) * mm, "end": v(-62, -7.92) * mm});
            skLineSegment(sketch, "E622", {"start": v(-62, -7.92) * mm, "end": v(-61.96, -7.86) * mm});
            skLineSegment(sketch, "E623", {"start": v(-61.96, -7.86) * mm, "end": v(-61.92, -7.8) * mm});
            skLineSegment(sketch, "E624", {"start": v(-61.92, -7.8) * mm, "end": v(-52.84, -7.8) * mm});
            skLineSegment(sketch, "E625", {"start": v(-52.84, -7.8) * mm, "end": v(-52.8, -7.86) * mm});
            skLineSegment(sketch, "E626", {"start": v(-52.8, -7.86) * mm, "end": v(-52.76, -7.92) * mm});
            skLineSegment(sketch, "E627", {"start": v(-52.76, -7.92) * mm, "end": v(-52.72, -8) * mm});
            skLineSegment(sketch, "E628", {"start": v(-52.72, -8) * mm, "end": v(-52.68, -8.06) * mm});
            skLineSegment(sketch, "E629", {"start": v(-52.68, -8.06) * mm, "end": v(-52.63, -8.13) * mm});
            skLineSegment(sketch, "E630", {"start": v(-52.63, -8.13) * mm, "end": v(-52.6, -8.2) * mm});
            skLineSegment(sketch, "E631", {"start": v(-52.6, -8.2) * mm, "end": v(-52.55, -8.26) * mm});
            skLineSegment(sketch, "E632", {"start": v(-52.55, -8.26) * mm, "end": v(-52.5, -8.32) * mm});
            skLineSegment(sketch, "E633", {"start": v(-80.48, 4.8) * mm, "end": v(-86.28, 5.45) * mm});
            skLineSegment(sketch, "E634", {"start": v(-86.28, 5.45) * mm, "end": v(-91.63, 7.3) * mm});
            skLineSegment(sketch, "E635", {"start": v(-91.63, 7.3) * mm, "end": v(-96.43, 10.18) * mm});
            skLineSegment(sketch, "E636", {"start": v(-96.43, 10.18) * mm, "end": v(-100.57, 13.96) * mm});
            skLineSegment(sketch, "E637", {"start": v(-100.57, 13.96) * mm, "end": v(-103.97, 18.49) * mm});
            skLineSegment(sketch, "E638", {"start": v(-103.97, 18.49) * mm, "end": v(-106.52, 23.6) * mm});
            skLineSegment(sketch, "E639", {"start": v(-106.52, 23.6) * mm, "end": v(-108.13, 29.17) * mm});
            skLineSegment(sketch, "E640", {"start": v(-108.13, 29.17) * mm, "end": v(-108.69, 35.02) * mm});
            skLineSegment(sketch, "E641", {"start": v(-108.69, 35.02) * mm, "end": v(-108.69, 84.86) * mm});
            skLineSegment(sketch, "E642", {"start": v(-108.69, 84.86) * mm, "end": v(-108.1, 90.93) * mm});
            skLineSegment(sketch, "E643", {"start": v(-108.1, 90.93) * mm, "end": v(-106.46, 96.59) * mm});
            skLineSegment(sketch, "E644", {"start": v(-106.46, 96.59) * mm, "end": v(-103.85, 101.72) * mm});
            skLineSegment(sketch, "E645", {"start": v(-103.85, 101.72) * mm, "end": v(-100.4, 106.2) * mm});
            skLineSegment(sketch, "E646", {"start": v(-100.4, 106.2) * mm, "end": v(-96.22, 109.9) * mm});
            skLineSegment(sketch, "E647", {"start": v(-96.22, 109.9) * mm, "end": v(-91.43, 112.69) * mm});
            skLineSegment(sketch, "E648", {"start": v(-91.43, 112.69) * mm, "end": v(-86.15, 114.46) * mm});
            skLineSegment(sketch, "E649", {"start": v(-86.15, 114.46) * mm, "end": v(-80.48, 115.07) * mm});
            skLineSegment(sketch, "E650", {"start": v(-80.48, 115.07) * mm, "end": v(-33.97, 115.07) * mm});
            skLineSegment(sketch, "E651", {"start": v(-33.97, 115.07) * mm, "end": v(-28.24, 114.44) * mm});
            skLineSegment(sketch, "E652", {"start": v(-28.24, 114.44) * mm, "end": v(-22.93, 112.64) * mm});
            skLineSegment(sketch, "E653", {"start": v(-22.93, 112.64) * mm, "end": v(-18.14, 109.8) * mm});
            skLineSegment(sketch, "E654", {"start": v(-18.14, 109.8) * mm, "end": v(-13.97, 106.08) * mm});
            skLineSegment(sketch, "E655", {"start": v(-13.97, 106.08) * mm, "end": v(-10.55, 101.58) * mm});
            skLineSegment(sketch, "E656", {"start": v(-10.55, 101.58) * mm, "end": v(-7.97, 96.45) * mm});
            skLineSegment(sketch, "E657", {"start": v(-7.97, 96.45) * mm, "end": v(-6.34, 90.83) * mm});
            skLineSegment(sketch, "E658", {"start": v(-6.34, 90.83) * mm, "end": v(-5.77, 84.86) * mm});
            skLineSegment(sketch, "E659", {"start": v(-5.77, 84.86) * mm, "end": v(-5.77, 35.02) * mm});
            skLineSegment(sketch, "E660", {"start": v(-5.77, 35.02) * mm, "end": v(-6.35, 28.95) * mm});
            skLineSegment(sketch, "E661", {"start": v(-6.35, 28.95) * mm, "end": v(-8, 23.28) * mm});
            skLineSegment(sketch, "E662", {"start": v(-8, 23.28) * mm, "end": v(-10.6, 18.15) * mm});
            skLineSegment(sketch, "E663", {"start": v(-10.6, 18.15) * mm, "end": v(-14.05, 13.68) * mm});
            skLineSegment(sketch, "E664", {"start": v(-14.05, 13.68) * mm, "end": v(-18.23, 9.98) * mm});
            skLineSegment(sketch, "E665", {"start": v(-18.23, 9.98) * mm, "end": v(-23.02, 7.18) * mm});
            skLineSegment(sketch, "E666", {"start": v(-23.02, 7.18) * mm, "end": v(-28.3, 5.42) * mm});
            skLineSegment(sketch, "E667", {"start": v(-28.3, 5.42) * mm, "end": v(-33.97, 4.8) * mm});
            skLineSegment(sketch, "E668", {"start": v(-33.97, 4.8) * mm, "end": v(-80.48, 4.8) * mm});
            skLineSegment(sketch, "E669", {"start": v(179.06, 188.44) * mm, "end": v(182.38, 186.05) * mm});
            skLineSegment(sketch, "E670", {"start": v(182.38, 186.05) * mm, "end": v(185.06, 183.43) * mm});
            skLineSegment(sketch, "E671", {"start": v(185.06, 183.43) * mm, "end": v(187.17, 180.59) * mm});
            skLineSegment(sketch, "E672", {"start": v(187.17, 180.59) * mm, "end": v(188.76, 177.54) * mm});
            skLineSegment(sketch, "E673", {"start": v(188.76, 177.54) * mm, "end": v(189.9, 174.3) * mm});
            skLineSegment(sketch, "E674", {"start": v(189.9, 174.3) * mm, "end": v(190.63, 170.89) * mm});
            skLineSegment(sketch, "E675", {"start": v(190.63, 170.89) * mm, "end": v(191.02, 167.32) * mm});
            skLineSegment(sketch, "E676", {"start": v(191.02, 167.32) * mm, "end": v(191.13, 163.6) * mm});
            skLineSegment(sketch, "E677", {"start": v(191.13, 163.6) * mm, "end": v(190.5, 156) * mm});
            skLineSegment(sketch, "E678", {"start": v(190.5, 156) * mm, "end": v(188.84, 148.89) * mm});
            skLineSegment(sketch, "E679", {"start": v(188.84, 148.89) * mm, "end": v(186.5, 141.96) * mm});
            skLineSegment(sketch, "E680", {"start": v(186.5, 141.96) * mm, "end": v(183.82, 134.94) * mm});
            skLineSegment(sketch, "E681", {"start": v(183.82, 134.94) * mm, "end": v(181.17, 127.56) * mm});
            skLineSegment(sketch, "E682", {"start": v(181.17, 127.56) * mm, "end": v(178.9, 119.53) * mm});
            skLineSegment(sketch, "E683", {"start": v(178.9, 119.53) * mm, "end": v(177.4, 110.57) * mm});
            skLineSegment(sketch, "E684", {"start": v(177.4, 110.57) * mm, "end": v(176.97, 100.4) * mm});
            skLineSegment(sketch, "E685", {"start": v(176.97, 100.4) * mm, "end": v(178.02, 90.83) * mm});
            skLineSegment(sketch, "E686", {"start": v(178.02, 90.83) * mm, "end": v(180.21, 82.91) * mm});
            skLineSegment(sketch, "E687", {"start": v(180.21, 82.91) * mm, "end": v(183.17, 76.12) * mm});
            skLineSegment(sketch, "E688", {"start": v(183.17, 76.12) * mm, "end": v(186.48, 69.94) * mm});
            skLineSegment(sketch, "E689", {"start": v(186.48, 69.94) * mm, "end": v(189.77, 63.85) * mm});
            skLineSegment(sketch, "E690", {"start": v(189.77, 63.85) * mm, "end": v(192.63, 57.31) * mm});
            skLineSegment(sketch, "E691", {"start": v(192.63, 57.31) * mm, "end": v(194.66, 49.8) * mm});
            skLineSegment(sketch, "E692", {"start": v(194.66, 49.8) * mm, "end": v(195.48, 40.82) * mm});
            skLineSegment(sketch, "E693", {"start": v(195.48, 40.82) * mm, "end": v(195.4, 37.03) * mm});
            skLineSegment(sketch, "E694", {"start": v(195.4, 37.03) * mm, "end": v(195.17, 33.7) * mm});
            skLineSegment(sketch, "E695", {"start": v(195.17, 33.7) * mm, "end": v(194.8, 30.69) * mm});
            skLineSegment(sketch, "E696", {"start": v(194.8, 30.69) * mm, "end": v(194.28, 27.86) * mm});
            skLineSegment(sketch, "E697", {"start": v(194.28, 27.86) * mm, "end": v(193.65, 25.07) * mm});
            skLineSegment(sketch, "E698", {"start": v(193.65, 25.07) * mm, "end": v(192.9, 22.18) * mm});
            skLineSegment(sketch, "E699", {"start": v(192.9, 22.18) * mm, "end": v(192.05, 19.04) * mm});
            skLineSegment(sketch, "E700", {"start": v(192.05, 19.04) * mm, "end": v(191.11, 15.51) * mm});
            skLineSegment(sketch, "E701", {"start": v(191.11, 15.51) * mm, "end": v(189.24, 19.14) * mm});
            skLineSegment(sketch, "E702", {"start": v(189.24, 19.14) * mm, "end": v(187.51, 22.5) * mm});
            skLineSegment(sketch, "E703", {"start": v(187.51, 22.5) * mm, "end": v(185.75, 25.59) * mm});
            skLineSegment(sketch, "E704", {"start": v(185.75, 25.59) * mm, "end": v(183.8, 28.43) * mm});
            skLineSegment(sketch, "E705", {"start": v(183.8, 28.43) * mm, "end": v(181.51, 31.03) * mm});
            skLineSegment(sketch, "E706", {"start": v(181.51, 31.03) * mm, "end": v(178.7, 33.39) * mm});
            skLineSegment(sketch, "E707", {"start": v(178.7, 33.39) * mm, "end": v(175.2, 35.53) * mm});
            skLineSegment(sketch, "E708", {"start": v(175.2, 35.53) * mm, "end": v(170.88, 37.45) * mm});
            skLineSegment(sketch, "E709", {"start": v(170.88, 37.45) * mm, "end": v(160.94, 40.33) * mm});
            skLineSegment(sketch, "E710", {"start": v(160.94, 40.33) * mm, "end": v(146.75, 42.77) * mm});
            skLineSegment(sketch, "E711", {"start": v(146.75, 42.77) * mm, "end": v(128.78, 44.18) * mm});
            skLineSegment(sketch, "E712", {"start": v(128.78, 44.18) * mm, "end": v(107.5, 43.98) * mm});
            skLineSegment(sketch, "E713", {"start": v(107.5, 43.98) * mm, "end": v(83.4, 41.58) * mm});
            skLineSegment(sketch, "E714", {"start": v(83.4, 41.58) * mm, "end": v(56.96, 36.4) * mm});
            skLineSegment(sketch, "E715", {"start": v(56.96, 36.4) * mm, "end": v(28.65, 27.84) * mm});
            skLineSegment(sketch, "E716", {"start": v(28.65, 27.84) * mm, "end": v(-1.07, 15.33) * mm});
            skLineSegment(sketch, "E717", {"start": v(-1.07, 15.33) * mm, "end": v(0.35, 18.33) * mm});
            skLineSegment(sketch, "E718", {"start": v(0.35, 18.33) * mm, "end": v(1.35, 21.23) * mm});
            skLineSegment(sketch, "E719", {"start": v(1.35, 21.23) * mm, "end": v(2, 24.56) * mm});
            skLineSegment(sketch, "E720", {"start": v(2, 24.56) * mm, "end": v(2.38, 28.87) * mm});
            skLineSegment(sketch, "E721", {"start": v(2.38, 28.87) * mm, "end": v(2.55, 34.67) * mm});
            skLineSegment(sketch, "E722", {"start": v(2.55, 34.67) * mm, "end": v(2.58, 42.5) * mm});
            skLineSegment(sketch, "E723", {"start": v(2.58, 42.5) * mm, "end": v(2.55, 52.9) * mm});
            skLineSegment(sketch, "E724", {"start": v(2.55, 52.9) * mm, "end": v(2.52, 66.38) * mm});
            skLineSegment(sketch, "E725", {"start": v(2.52, 66.38) * mm, "end": v(2.58, 66.4) * mm});
            skLineSegment(sketch, "E726", {"start": v(2.58, 66.4) * mm, "end": v(2.75, 66.43) * mm});
            skLineSegment(sketch, "E727", {"start": v(2.75, 66.43) * mm, "end": v(2.98, 66.5) * mm});
            skLineSegment(sketch, "E728", {"start": v(2.98, 66.5) * mm, "end": v(3.26, 66.56) * mm});
            skLineSegment(sketch, "E729", {"start": v(3.26, 66.56) * mm, "end": v(3.53, 66.63) * mm});
            skLineSegment(sketch, "E730", {"start": v(3.53, 66.63) * mm, "end": v(3.76, 66.68) * mm});
            skLineSegment(sketch, "E731", {"start": v(3.76, 66.68) * mm, "end": v(3.93, 66.73) * mm});
            skLineSegment(sketch, "E732", {"start": v(3.93, 66.73) * mm, "end": v(4, 66.74) * mm});
            skLineSegment(sketch, "E733", {"start": v(4, 66.74) * mm, "end": v(20.34, 70.91) * mm});
            skLineSegment(sketch, "E734", {"start": v(20.34, 70.91) * mm, "end": v(35.52, 74.95) * mm});
            skLineSegment(sketch, "E735", {"start": v(35.52, 74.95) * mm, "end": v(49.23, 78.76) * mm});
            skLineSegment(sketch, "E736", {"start": v(49.23, 78.76) * mm, "end": v(61.13, 82.23) * mm});
            skLineSegment(sketch, "E737", {"start": v(61.13, 82.23) * mm, "end": v(70.9, 85.28) * mm});
            skLineSegment(sketch, "E738", {"start": v(70.9, 85.28) * mm, "end": v(78.22, 87.8) * mm});
            skLineSegment(sketch, "E739", {"start": v(78.22, 87.8) * mm, "end": v(82.78, 89.7) * mm});
            skLineSegment(sketch, "E740", {"start": v(82.78, 89.7) * mm, "end": v(84.23, 90.9) * mm});
            skLineSegment(sketch, "E741", {"start": v(84.23, 90.9) * mm, "end": v(82.4, 91.26) * mm});
            skLineSegment(sketch, "E742", {"start": v(82.4, 91.26) * mm, "end": v(77.52, 90.8) * mm});
            skLineSegment(sketch, "E743", {"start": v(77.52, 90.8) * mm, "end": v(69.92, 89.59) * mm});
            skLineSegment(sketch, "E744", {"start": v(69.92, 89.59) * mm, "end": v(59.92, 87.69) * mm});
            skLineSegment(sketch, "E745", {"start": v(59.92, 87.69) * mm, "end": v(47.85, 85.17) * mm});
            skLineSegment(sketch, "E746", {"start": v(47.85, 85.17) * mm, "end": v(34.04, 82.09) * mm});
            skLineSegment(sketch, "E747", {"start": v(34.04, 82.09) * mm, "end": v(18.83, 78.52) * mm});
            skLineSegment(sketch, "E748", {"start": v(18.83, 78.52) * mm, "end": v(2.52, 74.53) * mm});
            skLineSegment(sketch, "E749", {"start": v(2.52, 74.53) * mm, "end": v(2.55, 78.57) * mm});
            skLineSegment(sketch, "E750", {"start": v(2.55, 78.57) * mm, "end": v(2.52, 82.8) * mm});
            skLineSegment(sketch, "E751", {"start": v(2.52, 82.8) * mm, "end": v(2.27, 87.15) * mm});
            skLineSegment(sketch, "E752", {"start": v(2.27, 87.15) * mm, "end": v(1.62, 91.57) * mm});
            skLineSegment(sketch, "E753", {"start": v(1.62, 91.57) * mm, "end": v(0.42, 96) * mm});
            skLineSegment(sketch, "E754", {"start": v(0.42, 96) * mm, "end": v(-1.52, 100.4) * mm});
            skLineSegment(sketch, "E755", {"start": v(-1.52, 100.4) * mm, "end": v(-4.36, 104.7) * mm});
            skLineSegment(sketch, "E756", {"start": v(-4.36, 104.7) * mm, "end": v(-8.27, 108.83) * mm});
            skLineSegment(sketch, "E757", {"start": v(-8.27, 108.83) * mm, "end": v(15.26, 134.18) * mm});
            skLineSegment(sketch, "E758", {"start": v(15.26, 134.18) * mm, "end": v(42.02, 154.56) * mm});
            skLineSegment(sketch, "E759", {"start": v(42.02, 154.56) * mm, "end": v(70.37, 170.25) * mm});
            skLineSegment(sketch, "E760", {"start": v(70.37, 170.25) * mm, "end": v(98.7, 181.55) * mm});
            skLineSegment(sketch, "E761", {"start": v(98.7, 181.55) * mm, "end": v(125.36, 188.73) * mm});
            skLineSegment(sketch, "E762", {"start": v(125.36, 188.73) * mm, "end": v(148.73, 192.08) * mm});
            skLineSegment(sketch, "E763", {"start": v(148.73, 192.08) * mm, "end": v(167.17, 191.89) * mm});
            skLineSegment(sketch, "E764", {"start": v(167.17, 191.89) * mm, "end": v(179.06, 188.44) * mm});
            skLineSegment(sketch, "E765", {"start": v(173.31, 3.76) * mm, "end": v(165.66, 0.82) * mm});
            skLineSegment(sketch, "E766", {"start": v(165.66, 0.82) * mm, "end": v(155.56, -1.04) * mm});
            skLineSegment(sketch, "E767", {"start": v(155.56, -1.04) * mm, "end": v(143.79, -2) * mm});
            skLineSegment(sketch, "E768", {"start": v(143.79, -2) * mm, "end": v(131.1, -2.23) * mm});
            skLineSegment(sketch, "E769", {"start": v(131.1, -2.23) * mm, "end": v(118.28, -1.95) * mm});
            skLineSegment(sketch, "E770", {"start": v(118.28, -1.95) * mm, "end": v(106.08, -1.33) * mm});
            skLineSegment(sketch, "E771", {"start": v(106.08, -1.33) * mm, "end": v(95.27, -0.57) * mm});
            skLineSegment(sketch, "E772", {"start": v(95.27, -0.57) * mm, "end": v(86.63, 0.15) * mm});
            skLineSegment(sketch, "E773", {"start": v(86.63, 0.15) * mm, "end": v(78.9, 0.86) * mm});
            skLineSegment(sketch, "E774", {"start": v(78.9, 0.86) * mm, "end": v(70.98, 1.66) * mm});
            skLineSegment(sketch, "E775", {"start": v(70.98, 1.66) * mm, "end": v(62.87, 2.55) * mm});
            skLineSegment(sketch, "E776", {"start": v(62.87, 2.55) * mm, "end": v(54.57, 3.54) * mm});
            skLineSegment(sketch, "E777", {"start": v(54.57, 3.54) * mm, "end": v(46.08, 4.61) * mm});
            skLineSegment(sketch, "E778", {"start": v(46.08, 4.61) * mm, "end": v(37.4, 5.78) * mm});
            skLineSegment(sketch, "E779", {"start": v(37.4, 5.78) * mm, "end": v(28.52, 7.04) * mm});
            skLineSegment(sketch, "E780", {"start": v(28.52, 7.04) * mm, "end": v(19.47, 8.4) * mm});
            skLineSegment(sketch, "E781", {"start": v(19.47, 8.4) * mm, "end": v(3.03, 10.91) * mm});
            skLineSegment(sketch, "E782", {"start": v(3.03, 10.91) * mm, "end": v(18.4, 17.26) * mm});
            skLineSegment(sketch, "E783", {"start": v(18.4, 17.26) * mm, "end": v(44.97, 26.7) * mm});
            skLineSegment(sketch, "E784", {"start": v(44.97, 26.7) * mm, "end": v(70.36, 32.98) * mm});
            skLineSegment(sketch, "E785", {"start": v(70.36, 32.98) * mm, "end": v(94.1, 36.58) * mm});
            skLineSegment(sketch, "E786", {"start": v(94.1, 36.58) * mm, "end": v(115.72, 37.95) * mm});
            skLineSegment(sketch, "E787", {"start": v(115.72, 37.95) * mm, "end": v(134.74, 37.55) * mm});
            skLineSegment(sketch, "E788", {"start": v(134.74, 37.55) * mm, "end": v(150.71, 35.84) * mm});
            skLineSegment(sketch, "E789", {"start": v(150.71, 35.84) * mm, "end": v(163.16, 33.27) * mm});
            skLineSegment(sketch, "E790", {"start": v(163.16, 33.27) * mm, "end": v(171.6, 30.3) * mm});
            skLineSegment(sketch, "E791", {"start": v(171.6, 30.3) * mm, "end": v(176.42, 27.29) * mm});
            skLineSegment(sketch, "E792", {"start": v(176.42, 27.29) * mm, "end": v(179.59, 23.84) * mm});
            skLineSegment(sketch, "E793", {"start": v(179.59, 23.84) * mm, "end": v(181.27, 20.12) * mm});
            skLineSegment(sketch, "E794", {"start": v(181.27, 20.12) * mm, "end": v(181.64, 16.3) * mm});
            skLineSegment(sketch, "E795", {"start": v(181.64, 16.3) * mm, "end": v(180.86, 12.6) * mm});
            skLineSegment(sketch, "E796", {"start": v(180.86, 12.6) * mm, "end": v(179.1, 9.14) * mm});
            skLineSegment(sketch, "E797", {"start": v(179.1, 9.14) * mm, "end": v(176.53, 6.14) * mm});
            skLineSegment(sketch, "E798", {"start": v(176.53, 6.14) * mm, "end": v(173.31, 3.76) * mm});
            skLineSegment(sketch, "E799", {"start": v(156.07, -29.12) * mm, "end": v(154.4, -27.72) * mm});
            skLineSegment(sketch, "E800", {"start": v(154.4, -27.72) * mm, "end": v(152.7, -26.3) * mm});
            skLineSegment(sketch, "E801", {"start": v(152.7, -26.3) * mm, "end": v(150.98, -24.86) * mm});
            skLineSegment(sketch, "E802", {"start": v(150.98, -24.86) * mm, "end": v(149.25, -23.41) * mm});
            skLineSegment(sketch, "E803", {"start": v(149.25, -23.41) * mm, "end": v(147.51, -21.94) * mm});
            skLineSegment(sketch, "E804", {"start": v(147.51, -21.94) * mm, "end": v(145.75, -20.46) * mm});
            skLineSegment(sketch, "E805", {"start": v(145.75, -20.46) * mm, "end": v(143.98, -18.96) * mm});
            skLineSegment(sketch, "E806", {"start": v(143.98, -18.96) * mm, "end": v(142.2, -17.45) * mm});
            skLineSegment(sketch, "E807", {"start": v(142.2, -17.45) * mm, "end": v(143.71, -16.67) * mm});
            skLineSegment(sketch, "E808", {"start": v(143.71, -16.67) * mm, "end": v(145.22, -15.88) * mm});
            skLineSegment(sketch, "E809", {"start": v(145.22, -15.88) * mm, "end": v(146.73, -15.08) * mm});
            skLineSegment(sketch, "E810", {"start": v(146.73, -15.08) * mm, "end": v(148.23, -14.28) * mm});
            skLineSegment(sketch, "E811", {"start": v(148.23, -14.28) * mm, "end": v(149.73, -13.47) * mm});
            skLineSegment(sketch, "E812", {"start": v(149.73, -13.47) * mm, "end": v(151.23, -12.66) * mm});
            skLineSegment(sketch, "E813", {"start": v(151.23, -12.66) * mm, "end": v(152.72, -11.84) * mm});
            skLineSegment(sketch, "E814", {"start": v(152.72, -11.84) * mm, "end": v(154.22, -11.02) * mm});
            skLineSegment(sketch, "E815", {"start": v(154.22, -11.02) * mm, "end": v(154.52, -10.98) * mm});
            skLineSegment(sketch, "E816", {"start": v(154.52, -10.98) * mm, "end": v(154.83, -10.95) * mm});
            skLineSegment(sketch, "E817", {"start": v(154.83, -10.95) * mm, "end": v(155.13, -10.9) * mm});
            skLineSegment(sketch, "E818", {"start": v(155.13, -10.9) * mm, "end": v(155.43, -10.87) * mm});
            skLineSegment(sketch, "E819", {"start": v(155.43, -10.87) * mm, "end": v(155.73, -10.83) * mm});
            skLineSegment(sketch, "E820", {"start": v(155.73, -10.83) * mm, "end": v(156.03, -10.8) * mm});
            skLineSegment(sketch, "E821", {"start": v(156.03, -10.8) * mm, "end": v(156.33, -10.75) * mm});
            skLineSegment(sketch, "E822", {"start": v(156.33, -10.75) * mm, "end": v(156.63, -10.71) * mm});
            skLineSegment(sketch, "E823", {"start": v(156.63, -10.71) * mm, "end": v(156.6, -13.02) * mm});
            skLineSegment(sketch, "E824", {"start": v(156.6, -13.02) * mm, "end": v(156.57, -15.33) * mm});
            skLineSegment(sketch, "E825", {"start": v(156.57, -15.33) * mm, "end": v(156.53, -17.64) * mm});
            skLineSegment(sketch, "E826", {"start": v(156.53, -17.64) * mm, "end": v(156.46, -19.94) * mm});
            skLineSegment(sketch, "E827", {"start": v(156.46, -19.94) * mm, "end": v(156.39, -22.24) * mm});
            skLineSegment(sketch, "E828", {"start": v(156.39, -22.24) * mm, "end": v(156.3, -24.54) * mm});
            skLineSegment(sketch, "E829", {"start": v(156.3, -24.54) * mm, "end": v(156.2, -26.83) * mm});
            skLineSegment(sketch, "E830", {"start": v(156.2, -26.83) * mm, "end": v(156.07, -29.12) * mm});
            skLineSegment(sketch, "E831", {"start": v(234.96, -91.13) * mm, "end": v(230.9, -88.14) * mm});
            skLineSegment(sketch, "E832", {"start": v(230.9, -88.14) * mm, "end": v(225.84, -84.4) * mm});
            skLineSegment(sketch, "E833", {"start": v(225.84, -84.4) * mm, "end": v(219.72, -79.82) * mm});
            skLineSegment(sketch, "E834", {"start": v(219.72, -79.82) * mm, "end": v(212.52, -74.35) * mm});
            skLineSegment(sketch, "E835", {"start": v(212.52, -74.35) * mm, "end": v(204.19, -67.93) * mm});
            skLineSegment(sketch, "E836", {"start": v(204.19, -67.93) * mm, "end": v(194.68, -60.49) * mm});
            skLineSegment(sketch, "E837", {"start": v(194.68, -60.49) * mm, "end": v(183.97, -51.95) * mm});
            skLineSegment(sketch, "E838", {"start": v(183.97, -51.95) * mm, "end": v(172, -42.26) * mm});
            skLineSegment(sketch, "E839", {"start": v(172, -42.26) * mm, "end": v(172.37, -37.84) * mm});
            skLineSegment(sketch, "E840", {"start": v(172.37, -37.84) * mm, "end": v(172.69, -33.4) * mm});
            skLineSegment(sketch, "E841", {"start": v(172.69, -33.4) * mm, "end": v(172.95, -28.96) * mm});
            skLineSegment(sketch, "E842", {"start": v(172.95, -28.96) * mm, "end": v(173.16, -24.5) * mm});
            skLineSegment(sketch, "E843", {"start": v(173.16, -24.5) * mm, "end": v(173.32, -20.04) * mm});
            skLineSegment(sketch, "E844", {"start": v(173.32, -20.04) * mm, "end": v(173.42, -15.56) * mm});
            skLineSegment(sketch, "E845", {"start": v(173.42, -15.56) * mm, "end": v(173.48, -11.07) * mm});
            skLineSegment(sketch, "E846", {"start": v(173.48, -11.07) * mm, "end": v(173.48, -6.57) * mm});
            skLineSegment(sketch, "E847", {"start": v(173.48, -6.57) * mm, "end": v(174.4, -6.2) * mm});
            skLineSegment(sketch, "E848", {"start": v(174.4, -6.2) * mm, "end": v(175.32, -5.84) * mm});
            skLineSegment(sketch, "E849", {"start": v(175.32, -5.84) * mm, "end": v(176.22, -5.45) * mm});
            skLineSegment(sketch, "E850", {"start": v(176.22, -5.45) * mm, "end": v(177.12, -5.05) * mm});
            skLineSegment(sketch, "E851", {"start": v(177.12, -5.05) * mm, "end": v(178, -4.63) * mm});
            skLineSegment(sketch, "E852", {"start": v(178, -4.63) * mm, "end": v(178.89, -4.2) * mm});
            skLineSegment(sketch, "E853", {"start": v(178.89, -4.2) * mm, "end": v(179.75, -3.74) * mm});
            skLineSegment(sketch, "E854", {"start": v(179.75, -3.74) * mm, "end": v(180.6, -3.27) * mm});
            skLineSegment(sketch, "E855", {"start": v(180.6, -3.27) * mm, "end": v(182.2, -2.62) * mm});
            skLineSegment(sketch, "E856", {"start": v(182.2, -2.62) * mm, "end": v(184.27, -2.01) * mm});
            skLineSegment(sketch, "E857", {"start": v(184.27, -2.01) * mm, "end": v(186.72, -1.22) * mm});
            skLineSegment(sketch, "E858", {"start": v(186.72, -1.22) * mm, "end": v(189.47, -0.02) * mm});
            skLineSegment(sketch, "E859", {"start": v(189.47, -0.02) * mm, "end": v(192.41, 1.82) * mm});
            skLineSegment(sketch, "E860", {"start": v(192.41, 1.82) * mm, "end": v(195.47, 4.52) * mm});
            skLineSegment(sketch, "E861", {"start": v(195.47, 4.52) * mm, "end": v(198.55, 8.3) * mm});
            skLineSegment(sketch, "E862", {"start": v(198.55, 8.3) * mm, "end": v(201.55, 13.4) * mm});
            skLineSegment(sketch, "E863", {"start": v(201.55, 13.4) * mm, "end": v(202.99, 16.53) * mm});
            skLineSegment(sketch, "E864", {"start": v(202.99, 16.53) * mm, "end": v(204.07, 19.53) * mm});
            skLineSegment(sketch, "E865", {"start": v(204.07, 19.53) * mm, "end": v(204.84, 22.48) * mm});
            skLineSegment(sketch, "E866", {"start": v(204.84, 22.48) * mm, "end": v(205.35, 25.5) * mm});
            skLineSegment(sketch, "E867", {"start": v(205.35, 25.5) * mm, "end": v(205.66, 28.67) * mm});
            skLineSegment(sketch, "E868", {"start": v(205.66, 28.67) * mm, "end": v(205.82, 32.12) * mm});
            skLineSegment(sketch, "E869", {"start": v(205.82, 32.12) * mm, "end": v(205.87, 35.94) * mm});
            skLineSegment(sketch, "E870", {"start": v(205.87, 35.94) * mm, "end": v(205.88, 40.24) * mm});
            skLineSegment(sketch, "E871", {"start": v(205.88, 40.24) * mm, "end": v(204.44, 53.25) * mm});
            skLineSegment(sketch, "E872", {"start": v(204.44, 53.25) * mm, "end": v(201.03, 63.62) * mm});
            skLineSegment(sketch, "E873", {"start": v(201.03, 63.62) * mm, "end": v(196.63, 72.46) * mm});
            skLineSegment(sketch, "E874", {"start": v(196.63, 72.46) * mm, "end": v(192.2, 80.86) * mm});
            skLineSegment(sketch, "E875", {"start": v(192.2, 80.86) * mm, "end": v(188.75, 89.9) * mm});
            skLineSegment(sketch, "E876", {"start": v(188.75, 89.9) * mm, "end": v(187.24, 100.69) * mm});
            skLineSegment(sketch, "E877", {"start": v(187.24, 100.69) * mm, "end": v(188.65, 114.3) * mm});
            skLineSegment(sketch, "E878", {"start": v(188.65, 114.3) * mm, "end": v(193.96, 131.85) * mm});
            skLineSegment(sketch, "E879", {"start": v(193.96, 131.85) * mm, "end": v(196.4, 137.76) * mm});
            skLineSegment(sketch, "E880", {"start": v(196.4, 137.76) * mm, "end": v(199.29, 145) * mm});
            skLineSegment(sketch, "E881", {"start": v(199.29, 145) * mm, "end": v(201.94, 153.18) * mm});
            skLineSegment(sketch, "E882", {"start": v(201.94, 153.18) * mm, "end": v(203.66, 161.95) * mm});
            skLineSegment(sketch, "E883", {"start": v(203.66, 161.95) * mm, "end": v(203.75, 170.93) * mm});
            skLineSegment(sketch, "E884", {"start": v(203.75, 170.93) * mm, "end": v(201.52, 179.75) * mm});
            skLineSegment(sketch, "E885", {"start": v(201.52, 179.75) * mm, "end": v(196.27, 188.05) * mm});
            skLineSegment(sketch, "E886", {"start": v(196.27, 188.05) * mm, "end": v(187.3, 195.45) * mm});
            skLineSegment(sketch, "E887", {"start": v(187.3, 195.45) * mm, "end": v(180.36, 198.98) * mm});
            skLineSegment(sketch, "E888", {"start": v(180.36, 198.98) * mm, "end": v(172.85, 201.43) * mm});
            skLineSegment(sketch, "E889", {"start": v(172.85, 201.43) * mm, "end": v(164.87, 202.9) * mm});
            skLineSegment(sketch, "E890", {"start": v(164.87, 202.9) * mm, "end": v(156.5, 203.47) * mm});
            skLineSegment(sketch, "E891", {"start": v(156.5, 203.47) * mm, "end": v(147.82, 203.25) * mm});
            skLineSegment(sketch, "E892", {"start": v(147.82, 203.25) * mm, "end": v(138.94, 202.32) * mm});
            skLineSegment(sketch, "E893", {"start": v(138.94, 202.32) * mm, "end": v(129.93, 200.8) * mm});
            skLineSegment(sketch, "E894", {"start": v(129.93, 200.8) * mm, "end": v(120.89, 198.74) * mm});
            skLineSegment(sketch, "E895", {"start": v(120.89, 198.74) * mm, "end": v(117.83, 204.07) * mm});
            skLineSegment(sketch, "E896", {"start": v(117.83, 204.07) * mm, "end": v(114.59, 209.49) * mm});
            skLineSegment(sketch, "E897", {"start": v(114.59, 209.49) * mm, "end": v(111.2, 214.96) * mm});
            skLineSegment(sketch, "E898", {"start": v(111.2, 214.96) * mm, "end": v(107.72, 220.44) * mm});
            skLineSegment(sketch, "E899", {"start": v(107.72, 220.44) * mm, "end": v(104.17, 225.86) * mm});
            skLineSegment(sketch, "E900", {"start": v(104.17, 225.86) * mm, "end": v(100.58, 231.19) * mm});
            skLineSegment(sketch, "E901", {"start": v(100.58, 231.19) * mm, "end": v(97, 236.37) * mm});
            skLineSegment(sketch, "E902", {"start": v(97, 236.37) * mm, "end": v(93.46, 241.36) * mm});
            skLineSegment(sketch, "E903", {"start": v(93.46, 241.36) * mm, "end": v(88.76, 247.75) * mm});
            skLineSegment(sketch, "E904", {"start": v(88.76, 247.75) * mm, "end": v(84.02, 253.96) * mm});
            skLineSegment(sketch, "E905", {"start": v(84.02, 253.96) * mm, "end": v(79.24, 259.97) * mm});
            skLineSegment(sketch, "E906", {"start": v(79.24, 259.97) * mm, "end": v(74.43, 265.78) * mm});
            skLineSegment(sketch, "E907", {"start": v(74.43, 265.78) * mm, "end": v(69.57, 271.41) * mm});
            skLineSegment(sketch, "E908", {"start": v(69.57, 271.41) * mm, "end": v(64.68, 276.85) * mm});
            skLineSegment(sketch, "E909", {"start": v(64.68, 276.85) * mm, "end": v(59.75, 282.1) * mm});
            skLineSegment(sketch, "E910", {"start": v(59.75, 282.1) * mm, "end": v(54.79, 287.15) * mm});
            skLineSegment(sketch, "E911", {"start": v(54.79, 287.15) * mm, "end": v(50.87, 291) * mm});
            skLineSegment(sketch, "E912", {"start": v(50.87, 291) * mm, "end": v(46.93, 294.72) * mm});
            skLineSegment(sketch, "E913", {"start": v(46.93, 294.72) * mm, "end": v(42.96, 298.32) * mm});
            skLineSegment(sketch, "E914", {"start": v(42.96, 298.32) * mm, "end": v(38.98, 301.81) * mm});
            skLineSegment(sketch, "E915", {"start": v(38.98, 301.81) * mm, "end": v(34.97, 305.18) * mm});
            skLineSegment(sketch, "E916", {"start": v(34.97, 305.18) * mm, "end": v(30.94, 308.42) * mm});
            skLineSegment(sketch, "E917", {"start": v(30.94, 308.42) * mm, "end": v(26.9, 311.55) * mm});
            skLineSegment(sketch, "E918", {"start": v(26.9, 311.55) * mm, "end": v(22.82, 314.54) * mm});
            skLineSegment(sketch, "E919", {"start": v(22.82, 314.54) * mm, "end": v(20.51, 316.2) * mm});
            skLineSegment(sketch, "E920", {"start": v(20.51, 316.2) * mm, "end": v(18.2, 317.81) * mm});
            skLineSegment(sketch, "E921", {"start": v(18.2, 317.81) * mm, "end": v(15.87, 319.4) * mm});
            skLineSegment(sketch, "E922", {"start": v(15.87, 319.4) * mm, "end": v(13.54, 320.96) * mm});
            skLineSegment(sketch, "E923", {"start": v(13.54, 320.96) * mm, "end": v(11.2, 322.47) * mm});
            skLineSegment(sketch, "E924", {"start": v(11.2, 322.47) * mm, "end": v(8.86, 323.94) * mm});
            skLineSegment(sketch, "E925", {"start": v(8.86, 323.94) * mm, "end": v(6.51, 325.37) * mm});
            skLineSegment(sketch, "E926", {"start": v(6.51, 325.37) * mm, "end": v(4.16, 326.74) * mm});
            skLineSegment(sketch, "E927", {"start": v(4.16, 326.74) * mm, "end": v(-6.98, 332.63) * mm});
            skLineSegment(sketch, "E928", {"start": v(-6.98, 332.63) * mm, "end": v(-17.27, 337.22) * mm});
            skLineSegment(sketch, "E929", {"start": v(-17.27, 337.22) * mm, "end": v(-26.66, 340.65) * mm});
            skLineSegment(sketch, "E930", {"start": v(-26.66, 340.65) * mm, "end": v(-35.07, 343.1) * mm});
            skLineSegment(sketch, "E931", {"start": v(-35.07, 343.1) * mm, "end": v(-42.44, 344.73) * mm});
            skLineSegment(sketch, "E932", {"start": v(-42.44, 344.73) * mm, "end": v(-48.7, 345.7) * mm});
            skLineSegment(sketch, "E933", {"start": v(-48.7, 345.7) * mm, "end": v(-53.8, 346.15) * mm});
            skLineSegment(sketch, "E934", {"start": v(-53.8, 346.15) * mm, "end": v(-57.65, 346.27) * mm});
            skLineSegment(sketch, "E935", {"start": v(-57.65, 346.27) * mm, "end": v(-57.71, 346.27) * mm});
            skLineSegment(sketch, "E936", {"start": v(-57.71, 346.27) * mm, "end": v(-59.2, 346.2) * mm});
            skLineSegment(sketch, "E937", {"start": v(-59.2, 346.2) * mm, "end": v(-59.3, 346.2) * mm});
            skLineSegment(sketch, "E938", {"start": v(-59.3, 346.2) * mm, "end": v(-59.44, 346.22) * mm});
            skLineSegment(sketch, "E939", {"start": v(-59.44, 346.22) * mm, "end": v(-59.6, 346.23) * mm});
            skLineSegment(sketch, "E940", {"start": v(-59.6, 346.23) * mm, "end": v(-59.8, 346.24) * mm});
            skLineSegment(sketch, "E941", {"start": v(-59.8, 346.24) * mm, "end": v(-60.01, 346.25) * mm});
            skLineSegment(sketch, "E942", {"start": v(-60.01, 346.25) * mm, "end": v(-60.26, 346.25) * mm});
            skLineSegment(sketch, "E943", {"start": v(-60.26, 346.25) * mm, "end": v(-60.54, 346.26) * mm});
            skLineSegment(sketch, "E944", {"start": v(-60.54, 346.26) * mm, "end": v(-60.84, 346.26) * mm});
            skLineSegment(sketch, "E945", {"start": v(-60.84, 346.26) * mm, "end": v(-66.46, 345.9) * mm});
            skLineSegment(sketch, "E946", {"start": v(-66.46, 345.9) * mm, "end": v(-76.83, 344.22) * mm});
            skLineSegment(sketch, "E947", {"start": v(-76.83, 344.22) * mm, "end": v(-91.35, 340.16) * mm});
            skLineSegment(sketch, "E948", {"start": v(-91.35, 340.16) * mm, "end": v(-109.4, 332.72) * mm});
            skLineSegment(sketch, "E949", {"start": v(-109.4, 332.72) * mm, "end": v(-130.37, 320.87) * mm});
            skLineSegment(sketch, "E950", {"start": v(-130.37, 320.87) * mm, "end": v(-153.64, 303.6) * mm});
            skLineSegment(sketch, "E951", {"start": v(-153.64, 303.6) * mm, "end": v(-178.6, 279.86) * mm});
            skLineSegment(sketch, "E952", {"start": v(-178.6, 279.86) * mm, "end": v(-204.65, 248.66) * mm});
            skLineSegment(sketch, "E953", {"start": v(-204.65, 248.66) * mm, "end": v(-208.25, 243.77) * mm});
            skLineSegment(sketch, "E954", {"start": v(-208.25, 243.77) * mm, "end": v(-211.86, 238.73) * mm});
            skLineSegment(sketch, "E955", {"start": v(-211.86, 238.73) * mm, "end": v(-215.47, 233.53) * mm});
            skLineSegment(sketch, "E956", {"start": v(-215.47, 233.53) * mm, "end": v(-219.08, 228.16) * mm});
            skLineSegment(sketch, "E957", {"start": v(-219.08, 228.16) * mm, "end": v(-222.7, 222.62) * mm});
            skLineSegment(sketch, "E958", {"start": v(-222.7, 222.62) * mm, "end": v(-226.32, 216.92) * mm});
            skLineSegment(sketch, "E959", {"start": v(-226.32, 216.92) * mm, "end": v(-229.94, 211.03) * mm});
            skLineSegment(sketch, "E960", {"start": v(-229.94, 211.03) * mm, "end": v(-233.56, 204.97) * mm});
            skLineSegment(sketch, "E961", {"start": v(-233.56, 204.97) * mm, "end": v(-233.56, 204.96) * mm});
            skLineSegment(sketch, "E962", {"start": v(-233.56, 204.96) * mm, "end": v(-233.57, 204.95) * mm});
            skLineSegment(sketch, "E963", {"start": v(-233.57, 204.95) * mm, "end": v(-233.57, 204.94) * mm});
            skLineSegment(sketch, "E964", {"start": v(-233.57, 204.94) * mm, "end": v(-233.58, 204.93) * mm});
            skLineSegment(sketch, "E965", {"start": v(-233.58, 204.93) * mm, "end": v(-233.59, 204.92) * mm});
            skLineSegment(sketch, "E966", {"start": v(-233.59, 204.92) * mm, "end": v(-233.6, 204.9) * mm});
            skLineSegment(sketch, "E967", {"start": v(-233.6, 204.9) * mm, "end": v(-233.6, 204.9) * mm});
            skLineSegment(sketch, "E968", {"start": v(-233.6, 204.9) * mm, "end": v(-233.6, 204.89) * mm});
            skLineSegment(sketch, "E969", {"start": v(-233.6, 204.89) * mm, "end": v(-234.07, 204.09) * mm});
            skLineSegment(sketch, "E970", {"start": v(-234.07, 204.09) * mm, "end": v(-234.53, 203.27) * mm});
            skLineSegment(sketch, "E971", {"start": v(-234.53, 203.27) * mm, "end": v(-234.98, 202.45) * mm});
            skLineSegment(sketch, "E972", {"start": v(-234.98, 202.45) * mm, "end": v(-235.44, 201.63) * mm});
            skLineSegment(sketch, "E973", {"start": v(-235.44, 201.63) * mm, "end": v(-235.89, 200.8) * mm});
            skLineSegment(sketch, "E974", {"start": v(-235.89, 200.8) * mm, "end": v(-236.34, 199.97) * mm});
            skLineSegment(sketch, "E975", {"start": v(-236.34, 199.97) * mm, "end": v(-236.79, 199.14) * mm});
            skLineSegment(sketch, "E976", {"start": v(-236.79, 199.14) * mm, "end": v(-237.24, 198.32) * mm});
            skLineSegment(sketch, "E977", {"start": v(-237.24, 198.32) * mm, "end": v(-259.48, 202.22) * mm});
            skLineSegment(sketch, "E978", {"start": v(-259.48, 202.22) * mm, "end": v(-278.48, 202.8) * mm});
            skLineSegment(sketch, "E979", {"start": v(-278.48, 202.8) * mm, "end": v(-293.94, 200) * mm});
            skLineSegment(sketch, "E980", {"start": v(-293.94, 200) * mm, "end": v(-305.61, 193.69) * mm});
            skLineSegment(sketch, "E981", {"start": v(-305.61, 193.69) * mm, "end": v(-313.2, 183.8) * mm});
            skLineSegment(sketch, "E982", {"start": v(-313.2, 183.8) * mm, "end": v(-316.43, 170.26) * mm});
            skLineSegment(sketch, "E983", {"start": v(-316.43, 170.26) * mm, "end": v(-315.03, 152.98) * mm});
            skLineSegment(sketch, "E984", {"start": v(-315.03, 152.98) * mm, "end": v(-308.72, 131.85) * mm});
            skLineSegment(sketch, "E985", {"start": v(-308.72, 131.85) * mm, "end": v(-303.34, 114.14) * mm});
            skLineSegment(sketch, "E986", {"start": v(-303.34, 114.14) * mm, "end": v(-301.9, 100.5) * mm});
            skLineSegment(sketch, "E987", {"start": v(-301.9, 100.5) * mm, "end": v(-303.4, 89.76) * mm});
            skLineSegment(sketch, "E988", {"start": v(-303.4, 89.76) * mm, "end": v(-306.87, 80.83) * mm});
            skLineSegment(sketch, "E989", {"start": v(-306.87, 80.83) * mm, "end": v(-311.32, 72.54) * mm});
            skLineSegment(sketch, "E990", {"start": v(-311.32, 72.54) * mm, "end": v(-315.75, 63.77) * mm});
            skLineSegment(sketch, "E991", {"start": v(-315.75, 63.77) * mm, "end": v(-319.19, 53.39) * mm});
            skLineSegment(sketch, "E992", {"start": v(-319.19, 53.39) * mm, "end": v(-320.64, 40.24) * mm});
            skLineSegment(sketch, "E993", {"start": v(-320.64, 40.24) * mm, "end": v(-320.63, 35.94) * mm});
            skLineSegment(sketch, "E994", {"start": v(-320.63, 35.94) * mm, "end": v(-320.58, 32.12) * mm});
            skLineSegment(sketch, "E995", {"start": v(-320.58, 32.12) * mm, "end": v(-320.42, 28.67) * mm});
            skLineSegment(sketch, "E996", {"start": v(-320.42, 28.67) * mm, "end": v(-320.1, 25.5) * mm});
            skLineSegment(sketch, "E997", {"start": v(-320.1, 25.5) * mm, "end": v(-319.6, 22.48) * mm});
            skLineSegment(sketch, "E998", {"start": v(-319.6, 22.48) * mm, "end": v(-318.83, 19.53) * mm});
            skLineSegment(sketch, "E999", {"start": v(-318.83, 19.53) * mm, "end": v(-317.75, 16.53) * mm});
            skLineSegment(sketch, "E1000", {"start": v(-317.75, 16.53) * mm, "end": v(-316.3, 13.4) * mm});
            skLineSegment(sketch, "E1001", {"start": v(-316.3, 13.4) * mm, "end": v(-313.3, 8.3) * mm});
            skLineSegment(sketch, "E1002", {"start": v(-313.3, 8.3) * mm, "end": v(-310.23, 4.52) * mm});
            skLineSegment(sketch, "E1003", {"start": v(-310.23, 4.52) * mm, "end": v(-307.17, 1.82) * mm});
            skLineSegment(sketch, "E1004", {"start": v(-307.17, 1.82) * mm, "end": v(-304.23, -0.02) * mm});
            skLineSegment(sketch, "E1005", {"start": v(-304.23, -0.02) * mm, "end": v(-301.48, -1.22) * mm});
            skLineSegment(sketch, "E1006", {"start": v(-301.48, -1.22) * mm, "end": v(-299.03, -2.01) * mm});
            skLineSegment(sketch, "E1007", {"start": v(-299.03, -2.01) * mm, "end": v(-296.96, -2.62) * mm});
            skLineSegment(sketch, "E1008", {"start": v(-296.96, -2.62) * mm, "end": v(-295.37, -3.27) * mm});
            skLineSegment(sketch, "E1009", {"start": v(-295.37, -3.27) * mm, "end": v(-294.52, -3.74) * mm});
            skLineSegment(sketch, "E1010", {"start": v(-294.52, -3.74) * mm, "end": v(-293.66, -4.19) * mm});
            skLineSegment(sketch, "E1011", {"start": v(-293.66, -4.19) * mm, "end": v(-292.79, -4.62) * mm});
            skLineSegment(sketch, "E1012", {"start": v(-292.79, -4.62) * mm, "end": v(-291.9, -5.03) * mm});
            skLineSegment(sketch, "E1013", {"start": v(-291.9, -5.03) * mm, "end": v(-291.02, -5.43) * mm});
            skLineSegment(sketch, "E1014", {"start": v(-291.02, -5.43) * mm, "end": v(-290.12, -5.82) * mm});
            skLineSegment(sketch, "E1015", {"start": v(-290.12, -5.82) * mm, "end": v(-289.2, -6.19) * mm});
            skLineSegment(sketch, "E1016", {"start": v(-289.2, -6.19) * mm, "end": v(-288.3, -6.55) * mm});
            skLineSegment(sketch, "E1017", {"start": v(-288.3, -6.55) * mm, "end": v(-288.27, -11.04) * mm});
            skLineSegment(sketch, "E1018", {"start": v(-288.27, -11.04) * mm, "end": v(-288.2, -15.52) * mm});
            skLineSegment(sketch, "E1019", {"start": v(-288.2, -15.52) * mm, "end": v(-288.07, -20) * mm});
            skLineSegment(sketch, "E1020", {"start": v(-288.07, -20) * mm, "end": v(-287.9, -24.46) * mm});
            skLineSegment(sketch, "E1021", {"start": v(-287.9, -24.46) * mm, "end": v(-287.68, -28.92) * mm});
            skLineSegment(sketch, "E1022", {"start": v(-287.68, -28.92) * mm, "end": v(-287.4, -33.36) * mm});
            skLineSegment(sketch, "E1023", {"start": v(-287.4, -33.36) * mm, "end": v(-287.07, -37.79) * mm});
            skLineSegment(sketch, "E1024", {"start": v(-287.07, -37.79) * mm, "end": v(-286.68, -42.2) * mm});
            skLineSegment(sketch, "E1025", {"start": v(-286.68, -42.2) * mm, "end": v(-295.87, -49.65) * mm});
            skLineSegment(sketch, "E1026", {"start": v(-295.87, -49.65) * mm, "end": v(-304.44, -56.52) * mm});
            skLineSegment(sketch, "E1027", {"start": v(-304.44, -56.52) * mm, "end": v(-312.4, -62.81) * mm});
            skLineSegment(sketch, "E1028", {"start": v(-312.4, -62.81) * mm, "end": v(-319.7, -68.52) * mm});
            skLineSegment(sketch, "E1029", {"start": v(-319.7, -68.52) * mm, "end": v(-326.35, -73.65) * mm});
            skLineSegment(sketch, "E1030", {"start": v(-326.35, -73.65) * mm, "end": v(-332.3, -78.18) * mm});
            skLineSegment(sketch, "E1031", {"start": v(-332.3, -78.18) * mm, "end": v(-337.56, -82.13) * mm});
            skLineSegment(sketch, "E1032", {"start": v(-337.56, -82.13) * mm, "end": v(-342.07, -85.49) * mm});
            skLineSegment(sketch, "E1033", {"start": v(-342.07, -85.49) * mm, "end": v(-349.72, -91.13) * mm});
            skLineSegment(sketch, "E1034", {"start": v(-349.72, -91.13) * mm, "end": v(-350.8, -92.06) * mm});
            skLineSegment(sketch, "E1035", {"start": v(-350.8, -92.06) * mm, "end": v(-351.74, -93.12) * mm});
            skLineSegment(sketch, "E1036", {"start": v(-351.74, -93.12) * mm, "end": v(-352.51, -94.28) * mm});
            skLineSegment(sketch, "E1037", {"start": v(-352.51, -94.28) * mm, "end": v(-353.1, -95.54) * mm});
            skLineSegment(sketch, "E1038", {"start": v(-353.1, -95.54) * mm, "end": v(-353.53, -96.86) * mm});
            skLineSegment(sketch, "E1039", {"start": v(-353.53, -96.86) * mm, "end": v(-353.76, -98.24) * mm});
            skLineSegment(sketch, "E1040", {"start": v(-353.76, -98.24) * mm, "end": v(-353.8, -99.64) * mm});
            skLineSegment(sketch, "E1041", {"start": v(-353.8, -99.64) * mm, "end": v(-353.65, -101.06) * mm});
            skLineSegment(sketch, "E1042", {"start": v(-353.65, -101.06) * mm, "end": v(-353.29, -102.45) * mm});
            skLineSegment(sketch, "E1043", {"start": v(-353.29, -102.45) * mm, "end": v(-352.75, -103.75) * mm});
            skLineSegment(sketch, "E1044", {"start": v(-352.75, -103.75) * mm, "end": v(-352.04, -104.95) * mm});
            skLineSegment(sketch, "E1045", {"start": v(-352.04, -104.95) * mm, "end": v(-351.17, -106.04) * mm});
            skLineSegment(sketch, "E1046", {"start": v(-351.17, -106.04) * mm, "end": v(-350.17, -107) * mm});
            skLineSegment(sketch, "E1047", {"start": v(-350.17, -107) * mm, "end": v(-349.03, -107.8) * mm});
            skLineSegment(sketch, "E1048", {"start": v(-349.03, -107.8) * mm, "end": v(-347.79, -108.46) * mm});
            skLineSegment(sketch, "E1049", {"start": v(-347.79, -108.46) * mm, "end": v(-346.44, -108.94) * mm});
            skLineSegment(sketch, "E1050", {"start": v(-346.44, -108.94) * mm, "end": v(-289.38, -124.81) * mm});
            skLineSegment(sketch, "E1051", {"start": v(-289.38, -124.81) * mm, "end": v(-292.5, -181.5) * mm});
            skLineSegment(sketch, "E1052", {"start": v(-292.5, -181.5) * mm, "end": v(-292.49, -182.84) * mm});
            skLineSegment(sketch, "E1053", {"start": v(-292.49, -182.84) * mm, "end": v(-292.3, -184.14) * mm});
            skLineSegment(sketch, "E1054", {"start": v(-292.3, -184.14) * mm, "end": v(-291.95, -185.4) * mm});
            skLineSegment(sketch, "E1055", {"start": v(-291.95, -185.4) * mm, "end": v(-291.44, -186.6) * mm});
            skLineSegment(sketch, "E1056", {"start": v(-291.44, -186.6) * mm, "end": v(-290.78, -187.71) * mm});
            skLineSegment(sketch, "E1057", {"start": v(-290.78, -187.71) * mm, "end": v(-289.98, -188.74) * mm});
            skLineSegment(sketch, "E1058", {"start": v(-289.98, -188.74) * mm, "end": v(-289.05, -189.67) * mm});
            skLineSegment(sketch, "E1059", {"start": v(-289.05, -189.67) * mm, "end": v(-287.99, -190.47) * mm});
            skLineSegment(sketch, "E1060", {"start": v(-287.99, -190.47) * mm, "end": v(-286.83, -191.13) * mm});
            skLineSegment(sketch, "E1061", {"start": v(-286.83, -191.13) * mm, "end": v(-285.62, -191.62) * mm});
            skLineSegment(sketch, "E1062", {"start": v(-285.62, -191.62) * mm, "end": v(-284.35, -191.95) * mm});
            skLineSegment(sketch, "E1063", {"start": v(-284.35, -191.95) * mm, "end": v(-283.07, -192.12) * mm});
            skLineSegment(sketch, "E1064", {"start": v(-283.07, -192.12) * mm, "end": v(-281.77, -192.11) * mm});
            skLineSegment(sketch, "E1065", {"start": v(-281.77, -192.11) * mm, "end": v(-280.47, -191.94) * mm});
            skLineSegment(sketch, "E1066", {"start": v(-280.47, -191.94) * mm, "end": v(-279.2, -191.6) * mm});
            skLineSegment(sketch, "E1067", {"start": v(-279.2, -191.6) * mm, "end": v(-277.97, -191.08) * mm});
            skLineSegment(sketch, "E1068", {"start": v(-277.97, -191.08) * mm, "end": v(-270.83, -187.54) * mm});
            skLineSegment(sketch, "E1069", {"start": v(-270.83, -187.54) * mm, "end": v(-267.06, -185.64) * mm});
            skLineSegment(sketch, "E1070", {"start": v(-267.06, -185.64) * mm, "end": v(-263.32, -183.7) * mm});
            skLineSegment(sketch, "E1071", {"start": v(-263.32, -183.7) * mm, "end": v(-259.62, -181.75) * mm});
            skLineSegment(sketch, "E1072", {"start": v(-259.62, -181.75) * mm, "end": v(-255.95, -179.76) * mm});
            skLineSegment(sketch, "E1073", {"start": v(-255.95, -179.76) * mm, "end": v(-252.3, -177.75) * mm});
            skLineSegment(sketch, "E1074", {"start": v(-252.3, -177.75) * mm, "end": v(-248.7, -175.72) * mm});
            skLineSegment(sketch, "E1075", {"start": v(-248.7, -175.72) * mm, "end": v(-245.11, -173.67) * mm});
            skLineSegment(sketch, "E1076", {"start": v(-245.11, -173.67) * mm, "end": v(-241.55, -171.6) * mm});
            skLineSegment(sketch, "E1077", {"start": v(-241.55, -171.6) * mm, "end": v(-238.36, -175.9) * mm});
            skLineSegment(sketch, "E1078", {"start": v(-238.36, -175.9) * mm, "end": v(-235.09, -180.1) * mm});
            skLineSegment(sketch, "E1079", {"start": v(-235.09, -180.1) * mm, "end": v(-231.72, -184.17) * mm});
            skLineSegment(sketch, "E1080", {"start": v(-231.72, -184.17) * mm, "end": v(-228.27, -188.14) * mm});
            skLineSegment(sketch, "E1081", {"start": v(-228.27, -188.14) * mm, "end": v(-224.73, -191.99) * mm});
            skLineSegment(sketch, "E1082", {"start": v(-224.73, -191.99) * mm, "end": v(-221.1, -195.73) * mm});
            skLineSegment(sketch, "E1083", {"start": v(-221.1, -195.73) * mm, "end": v(-217.36, -199.35) * mm});
            skLineSegment(sketch, "E1084", {"start": v(-217.36, -199.35) * mm, "end": v(-213.54, -202.85) * mm});
            skLineSegment(sketch, "E1085", {"start": v(-213.54, -202.85) * mm, "end": v(-198.4, -214.95) * mm});
            skLineSegment(sketch, "E1086", {"start": v(-198.4, -214.95) * mm, "end": v(-182, -225.45) * mm});
            skLineSegment(sketch, "E1087", {"start": v(-182, -225.45) * mm, "end": v(-164.35, -234.36) * mm});
            skLineSegment(sketch, "E1088", {"start": v(-164.35, -234.36) * mm, "end": v(-145.45, -241.66) * mm});
            skLineSegment(sketch, "E1089", {"start": v(-145.45, -241.66) * mm, "end": v(-125.3, -247.35) * mm});
            skLineSegment(sketch, "E1090", {"start": v(-125.3, -247.35) * mm, "end": v(-103.93, -251.42) * mm});
            skLineSegment(sketch, "E1091", {"start": v(-103.93, -251.42) * mm, "end": v(-81.33, -253.87) * mm});
            skLineSegment(sketch, "E1092", {"start": v(-81.33, -253.87) * mm, "end": v(-57.5, -254.68) * mm});
            skLineSegment(sketch, "E1093", {"start": v(-57.5, -254.68) * mm, "end": v(-57.34, -254.68) * mm});
            skLineSegment(sketch, "E1094", {"start": v(-57.34, -254.68) * mm, "end": v(-57.17, -254.68) * mm});
            skLineSegment(sketch, "E1095", {"start": v(-57.17, -254.68) * mm, "end": v(-57, -254.68) * mm});
            skLineSegment(sketch, "E1096", {"start": v(-57, -254.68) * mm, "end": v(-56.84, -254.68) * mm});
            skLineSegment(sketch, "E1097", {"start": v(-56.84, -254.68) * mm, "end": v(-56.67, -254.68) * mm});
            skLineSegment(sketch, "E1098", {"start": v(-56.67, -254.68) * mm, "end": v(-56.5, -254.68) * mm});
            skLineSegment(sketch, "E1099", {"start": v(-56.5, -254.68) * mm, "end": v(-56.33, -254.68) * mm});
            skLineSegment(sketch, "E1100", {"start": v(-56.33, -254.68) * mm, "end": v(-56.17, -254.68) * mm});
            skLineSegment(sketch, "E1101", {"start": v(-56.17, -254.68) * mm, "end": v(-26.24, -253.28) * mm});
            skLineSegment(sketch, "E1102", {"start": v(-26.24, -253.28) * mm, "end": v(1.72, -249.3) * mm});
            skLineSegment(sketch, "E1103", {"start": v(1.72, -249.3) * mm, "end": v(27.7, -242.75) * mm});
            skLineSegment(sketch, "E1104", {"start": v(27.7, -242.75) * mm, "end": v(51.68, -233.66) * mm});
            skLineSegment(sketch, "E1105", {"start": v(51.68, -233.66) * mm, "end": v(73.65, -222.01) * mm});
            skLineSegment(sketch, "E1106", {"start": v(73.65, -222.01) * mm, "end": v(93.59, -207.84) * mm});
            skLineSegment(sketch, "E1107", {"start": v(93.59, -207.84) * mm, "end": v(111.5, -191.14) * mm});
            skLineSegment(sketch, "E1108", {"start": v(111.5, -191.14) * mm, "end": v(127.34, -171.93) * mm});
            skLineSegment(sketch, "E1109", {"start": v(127.34, -171.93) * mm, "end": v(130.84, -173.95) * mm});
            skLineSegment(sketch, "E1110", {"start": v(130.84, -173.95) * mm, "end": v(134.36, -175.96) * mm});
            skLineSegment(sketch, "E1111", {"start": v(134.36, -175.96) * mm, "end": v(137.9, -177.94) * mm});
            skLineSegment(sketch, "E1112", {"start": v(137.9, -177.94) * mm, "end": v(141.48, -179.91) * mm});
            skLineSegment(sketch, "E1113", {"start": v(141.48, -179.91) * mm, "end": v(145.08, -181.86) * mm});
            skLineSegment(sketch, "E1114", {"start": v(145.08, -181.86) * mm, "end": v(148.7, -183.78) * mm});
            skLineSegment(sketch, "E1115", {"start": v(148.7, -183.78) * mm, "end": v(152.38, -185.68) * mm});
            skLineSegment(sketch, "E1116", {"start": v(152.38, -185.68) * mm, "end": v(156.08, -187.54) * mm});
            skLineSegment(sketch, "E1117", {"start": v(156.08, -187.54) * mm, "end": v(158.65, -188.83) * mm});
            skLineSegment(sketch, "E1118", {"start": v(158.65, -188.83) * mm, "end": v(160.7, -189.86) * mm});
            skLineSegment(sketch, "E1119", {"start": v(160.7, -189.86) * mm, "end": v(162.34, -190.67) * mm});
            skLineSegment(sketch, "E1120", {"start": v(162.34, -190.67) * mm, "end": v(163.65, -191.26) * mm});
            skLineSegment(sketch, "E1121", {"start": v(163.65, -191.26) * mm, "end": v(164.74, -191.68) * mm});
            skLineSegment(sketch, "E1122", {"start": v(164.74, -191.68) * mm, "end": v(165.7, -191.95) * mm});
            skLineSegment(sketch, "E1123", {"start": v(165.7, -191.95) * mm, "end": v(166.66, -192.1) * mm});
            skLineSegment(sketch, "E1124", {"start": v(166.66, -192.1) * mm, "end": v(167.69, -192.13) * mm});
            skLineSegment(sketch, "E1125", {"start": v(167.69, -192.13) * mm, "end": v(169.8, -191.91) * mm});
            skLineSegment(sketch, "E1126", {"start": v(169.8, -191.91) * mm, "end": v(171.75, -191.28) * mm});
            skLineSegment(sketch, "E1127", {"start": v(171.75, -191.28) * mm, "end": v(173.5, -190.29) * mm});
            skLineSegment(sketch, "E1128", {"start": v(173.5, -190.29) * mm, "end": v(175, -188.98) * mm});
            skLineSegment(sketch, "E1129", {"start": v(175, -188.98) * mm, "end": v(176.23, -187.4) * mm});
            skLineSegment(sketch, "E1130", {"start": v(176.23, -187.4) * mm, "end": v(177.12, -185.6) * mm});
            skLineSegment(sketch, "E1131", {"start": v(177.12, -185.6) * mm, "end": v(177.64, -183.62) * mm});
            skLineSegment(sketch, "E1132", {"start": v(177.64, -183.62) * mm, "end": v(177.75, -181.5) * mm});
            skLineSegment(sketch, "E1133", {"start": v(177.75, -181.5) * mm, "end": v(174.62, -124.81) * mm});
            skLineSegment(sketch, "E1134", {"start": v(174.62, -124.81) * mm, "end": v(231.68, -108.94) * mm});
            skLineSegment(sketch, "E1135", {"start": v(231.68, -108.94) * mm, "end": v(234.42, -107.74) * mm});
            skLineSegment(sketch, "E1136", {"start": v(234.42, -107.74) * mm, "end": v(236.55, -105.91) * mm});
            skLineSegment(sketch, "E1137", {"start": v(236.55, -105.91) * mm, "end": v(238.05, -103.63) * mm});
            skLineSegment(sketch, "E1138", {"start": v(238.05, -103.63) * mm, "end": v(238.88, -101.06) * mm});
            skLineSegment(sketch, "E1139", {"start": v(238.88, -101.06) * mm, "end": v(239.02, -98.36) * mm});
            skLineSegment(sketch, "E1140", {"start": v(239.02, -98.36) * mm, "end": v(238.43, -95.7) * mm});
            skLineSegment(sketch, "E1141", {"start": v(238.43, -95.7) * mm, "end": v(237.1, -93.24) * mm});
            skLineSegment(sketch, "E1142", {"start": v(237.1, -93.24) * mm, "end": v(234.96, -91.13) * mm});
            skSolve(sketch);
        }
        {
            var Q0;
            Q0 = qSketchRegion(id + "F2", true);
            extrude(context, id + "F3", {"entities" : qUnion([Q0]), "depth" : 5 * mm, "offsetDistance" : 25 * mm});
        }
        {
            var Q0;
            Q0=makeQuery(id+"F3.opExtrude","SWEPT_BODY",BODY,{"disambiguationData":[OSD([sQuery(id+"F2.wireOp",EDGE,"E1"),sQuery(id+"F2.wireOp",EDGE,"E2"),sQuery(id+"F2.wireOp",EDGE,"E3"),sQuery(id+"F2.wireOp",EDGE,"E4"),sQuery(id+"F2.wireOp",EDGE,"E5"),sQuery(id+"F2.wireOp",EDGE,"E6"),sQuery(id+"F2.wireOp",EDGE,"E7"),sQuery(id+"F2.wireOp",EDGE,"E8"),sQuery(id+"F2.wireOp",EDGE,"E9"),sQuery(id+"F2.wireOp",EDGE,"E10"),sQuery(id+"F2.wireOp",EDGE,"E11"),sQuery(id+"F2.wireOp",EDGE,"E12"),sQuery(id+"F2.wireOp",EDGE,"E13"),sQuery(id+"F2.wireOp",EDGE,"E14"),sQuery(id+"F2.wireOp",EDGE,"E15"),sQuery(id+"F2.wireOp",EDGE,"E16"),sQuery(id+"F2.wireOp",EDGE,"E17"),sQuery(id+"F2.wireOp",EDGE,"E18"),sQuery(id+"F2.wireOp",EDGE,"E19"),sQuery(id+"F2.wireOp",EDGE,"E20"),sQuery(id+"F2.wireOp",EDGE,"E21"),sQuery(id+"F2.wireOp",EDGE,"E22"),sQuery(id+"F2.wireOp",EDGE,"E23"),sQuery(id+"F2.wireOp",EDGE,"E24"),sQuery(id+"F2.wireOp",EDGE,"E25"),sQuery(id+"F2.wireOp",EDGE,"E26"),sQuery(id+"F2.wireOp",EDGE,"E27"),sQuery(id+"F2.wireOp",EDGE,"E28"),sQuery(id+"F2.wireOp",EDGE,"E29"),sQuery(id+"F2.wireOp",EDGE,"E30"),sQuery(id+"F2.wireOp",EDGE,"E31"),sQuery(id+"F2.wireOp",EDGE,"E32"),sQuery(id+"F2.wireOp",EDGE,"E33"),sQuery(id+"F2.wireOp",EDGE,"E34"),sQuery(id+"F2.wireOp",EDGE,"E35"),sQuery(id+"F2.wireOp",EDGE,"E36"),sQuery(id+"F2.wireOp",EDGE,"E37"),sQuery(id+"F2.wireOp",EDGE,"E38"),sQuery(id+"F2.wireOp",EDGE,"E39"),sQuery(id+"F2.wireOp",EDGE,"E40"),sQuery(id+"F2.wireOp",EDGE,"E41"),sQuery(id+"F2.wireOp",EDGE,"E42"),sQuery(id+"F2.wireOp",EDGE,"E43"),sQuery(id+"F2.wireOp",EDGE,"E44"),sQuery(id+"F2.wireOp",EDGE,"E45"),sQuery(id+"F2.wireOp",EDGE,"E46"),sQuery(id+"F2.wireOp",EDGE,"E47"),sQuery(id+"F2.wireOp",EDGE,"E48"),sQuery(id+"F2.wireOp",EDGE,"E49"),sQuery(id+"F2.wireOp",EDGE,"E50"),sQuery(id+"F2.wireOp",EDGE,"E51"),sQuery(id+"F2.wireOp",EDGE,"E52"),sQuery(id+"F2.wireOp",EDGE,"E53"),sQuery(id+"F2.wireOp",EDGE,"E54"),sQuery(id+"F2.wireOp",EDGE,"E55"),sQuery(id+"F2.wireOp",EDGE,"E56"),sQuery(id+"F2.wireOp",EDGE,"E57"),sQuery(id+"F2.wireOp",EDGE,"E58"),sQuery(id+"F2.wireOp",EDGE,"E59"),sQuery(id+"F2.wireOp",EDGE,"E60"),sQuery(id+"F2.wireOp",EDGE,"E61"),sQuery(id+"F2.wireOp",EDGE,"E62"),sQuery(id+"F2.wireOp",EDGE,"E63"),sQuery(id+"F2.wireOp",EDGE,"E64"),sQuery(id+"F2.wireOp",EDGE,"E65"),sQuery(id+"F2.wireOp",EDGE,"E66"),sQuery(id+"F2.wireOp",EDGE,"E67"),sQuery(id+"F2.wireOp",EDGE,"E68"),sQuery(id+"F2.wireOp",EDGE,"E69"),sQuery(id+"F2.wireOp",EDGE,"E70"),sQuery(id+"F2.wireOp",EDGE,"E71"),sQuery(id+"F2.wireOp",EDGE,"E72"),sQuery(id+"F2.wireOp",EDGE,"E73"),sQuery(id+"F2.wireOp",EDGE,"E74"),sQuery(id+"F2.wireOp",EDGE,"E75"),sQuery(id+"F2.wireOp",EDGE,"E76"),sQuery(id+"F2.wireOp",EDGE,"E77"),sQuery(id+"F2.wireOp",EDGE,"E78"),sQuery(id+"F2.wireOp",EDGE,"E79"),sQuery(id+"F2.wireOp",EDGE,"E80"),sQuery(id+"F2.wireOp",EDGE,"E81"),sQuery(id+"F2.wireOp",EDGE,"E82"),sQuery(id+"F2.wireOp",EDGE,"E83"),sQuery(id+"F2.wireOp",EDGE,"E84"),sQuery(id+"F2.wireOp",EDGE,"E85"),sQuery(id+"F2.wireOp",EDGE,"E86"),sQuery(id+"F2.wireOp",EDGE,"E87"),sQuery(id+"F2.wireOp",EDGE,"E88"),sQuery(id+"F2.wireOp",EDGE,"E89"),sQuery(id+"F2.wireOp",EDGE,"E90"),sQuery(id+"F2.wireOp",EDGE,"E91"),sQuery(id+"F2.wireOp",EDGE,"E92"),sQuery(id+"F2.wireOp",EDGE,"E93"),sQuery(id+"F2.wireOp",EDGE,"E94"),sQuery(id+"F2.wireOp",EDGE,"E95"),sQuery(id+"F2.wireOp",EDGE,"E96"),sQuery(id+"F2.wireOp",EDGE,"E97"),sQuery(id+"F2.wireOp",EDGE,"E98"),sQuery(id+"F2.wireOp",EDGE,"E99"),sQuery(id+"F2.wireOp",EDGE,"E100"),sQuery(id+"F2.wireOp",EDGE,"E101"),sQuery(id+"F2.wireOp",EDGE,"E102"),sQuery(id+"F2.wireOp",EDGE,"E103"),sQuery(id+"F2.wireOp",EDGE,"E104"),sQuery(id+"F2.wireOp",EDGE,"E105"),sQuery(id+"F2.wireOp",EDGE,"E106"),sQuery(id+"F2.wireOp",EDGE,"E107"),sQuery(id+"F2.wireOp",EDGE,"E108"),sQuery(id+"F2.wireOp",EDGE,"E109"),sQuery(id+"F2.wireOp",EDGE,"E110"),sQuery(id+"F2.wireOp",EDGE,"E111"),sQuery(id+"F2.wireOp",EDGE,"E112"),sQuery(id+"F2.wireOp",EDGE,"E113"),sQuery(id+"F2.wireOp",EDGE,"E114"),sQuery(id+"F2.wireOp",EDGE,"E115"),sQuery(id+"F2.wireOp",EDGE,"E116"),sQuery(id+"F2.wireOp",EDGE,"E117"),sQuery(id+"F2.wireOp",EDGE,"E118"),sQuery(id+"F2.wireOp",EDGE,"E119"),sQuery(id+"F2.wireOp",EDGE,"E120"),sQuery(id+"F2.wireOp",EDGE,"E121"),sQuery(id+"F2.wireOp",EDGE,"E122"),sQuery(id+"F2.wireOp",EDGE,"E123"),sQuery(id+"F2.wireOp",EDGE,"E124"),sQuery(id+"F2.wireOp",EDGE,"E125"),sQuery(id+"F2.wireOp",EDGE,"E126"),sQuery(id+"F2.wireOp",EDGE,"E127"),sQuery(id+"F2.wireOp",EDGE,"E128"),sQuery(id+"F2.wireOp",EDGE,"E129"),sQuery(id+"F2.wireOp",EDGE,"E130"),sQuery(id+"F2.wireOp",EDGE,"E131"),sQuery(id+"F2.wireOp",EDGE,"E132"),sQuery(id+"F2.wireOp",EDGE,"E133"),sQuery(id+"F2.wireOp",EDGE,"E134"),sQuery(id+"F2.wireOp",EDGE,"E135"),sQuery(id+"F2.wireOp",EDGE,"E136"),sQuery(id+"F2.wireOp",EDGE,"E137"),sQuery(id+"F2.wireOp",EDGE,"E138"),sQuery(id+"F2.wireOp",EDGE,"E139"),sQuery(id+"F2.wireOp",EDGE,"E140"),sQuery(id+"F2.wireOp",EDGE,"E141"),sQuery(id+"F2.wireOp",EDGE,"E142"),sQuery(id+"F2.wireOp",EDGE,"E143"),sQuery(id+"F2.wireOp",EDGE,"E144"),sQuery(id+"F2.wireOp",EDGE,"E145"),sQuery(id+"F2.wireOp",EDGE,"E146"),sQuery(id+"F2.wireOp",EDGE,"E147"),sQuery(id+"F2.wireOp",EDGE,"E148"),sQuery(id+"F2.wireOp",EDGE,"E149"),sQuery(id+"F2.wireOp",EDGE,"E150"),sQuery(id+"F2.wireOp",EDGE,"E151"),sQuery(id+"F2.wireOp",EDGE,"E152"),sQuery(id+"F2.wireOp",EDGE,"E153"),sQuery(id+"F2.wireOp",EDGE,"E154"),sQuery(id+"F2.wireOp",EDGE,"E155"),sQuery(id+"F2.wireOp",EDGE,"E156"),sQuery(id+"F2.wireOp",EDGE,"E157"),sQuery(id+"F2.wireOp",EDGE,"E158"),sQuery(id+"F2.wireOp",EDGE,"E159"),sQuery(id+"F2.wireOp",EDGE,"E160"),sQuery(id+"F2.wireOp",EDGE,"E161"),sQuery(id+"F2.wireOp",EDGE,"E162"),sQuery(id+"F2.wireOp",EDGE,"E163"),sQuery(id+"F2.wireOp",EDGE,"E164"),sQuery(id+"F2.wireOp",EDGE,"E165"),sQuery(id+"F2.wireOp",EDGE,"E166"),sQuery(id+"F2.wireOp",EDGE,"E167"),sQuery(id+"F2.wireOp",EDGE,"E168"),sQuery(id+"F2.wireOp",EDGE,"E169"),sQuery(id+"F2.wireOp",EDGE,"E170"),sQuery(id+"F2.wireOp",EDGE,"E171"),sQuery(id+"F2.wireOp",EDGE,"E172"),sQuery(id+"F2.wireOp",EDGE,"E173"),sQuery(id+"F2.wireOp",EDGE,"E174"),sQuery(id+"F2.wireOp",EDGE,"E175"),sQuery(id+"F2.wireOp",EDGE,"E176"),sQuery(id+"F2.wireOp",EDGE,"E177"),sQuery(id+"F2.wireOp",EDGE,"E178"),sQuery(id+"F2.wireOp",EDGE,"E179"),sQuery(id+"F2.wireOp",EDGE,"E180"),sQuery(id+"F2.wireOp",EDGE,"E181"),sQuery(id+"F2.wireOp",EDGE,"E182"),sQuery(id+"F2.wireOp",EDGE,"E183"),sQuery(id+"F2.wireOp",EDGE,"E184"),sQuery(id+"F2.wireOp",EDGE,"E185"),sQuery(id+"F2.wireOp",EDGE,"E186"),sQuery(id+"F2.wireOp",EDGE,"E187"),sQuery(id+"F2.wireOp",EDGE,"E188"),sQuery(id+"F2.wireOp",EDGE,"E189"),sQuery(id+"F2.wireOp",EDGE,"E190"),sQuery(id+"F2.wireOp",EDGE,"E191"),sQuery(id+"F2.wireOp",EDGE,"E192"),sQuery(id+"F2.wireOp",EDGE,"E193"),sQuery(id+"F2.wireOp",EDGE,"E194"),sQuery(id+"F2.wireOp",EDGE,"E195"),sQuery(id+"F2.wireOp",EDGE,"E196"),sQuery(id+"F2.wireOp",EDGE,"E197"),sQuery(id+"F2.wireOp",EDGE,"E198"),sQuery(id+"F2.wireOp",EDGE,"E199"),sQuery(id+"F2.wireOp",EDGE,"E200"),sQuery(id+"F2.wireOp",EDGE,"E201"),sQuery(id+"F2.wireOp",EDGE,"E202"),sQuery(id+"F2.wireOp",EDGE,"E203"),sQuery(id+"F2.wireOp",EDGE,"E204"),sQuery(id+"F2.wireOp",EDGE,"E205"),sQuery(id+"F2.wireOp",EDGE,"E206"),sQuery(id+"F2.wireOp",EDGE,"E207"),sQuery(id+"F2.wireOp",EDGE,"E208"),sQuery(id+"F2.wireOp",EDGE,"E209"),sQuery(id+"F2.wireOp",EDGE,"E210"),sQuery(id+"F2.wireOp",EDGE,"E211"),sQuery(id+"F2.wireOp",EDGE,"E212"),sQuery(id+"F2.wireOp",EDGE,"E213"),sQuery(id+"F2.wireOp",EDGE,"E214"),sQuery(id+"F2.wireOp",EDGE,"E215"),sQuery(id+"F2.wireOp",EDGE,"E216"),sQuery(id+"F2.wireOp",EDGE,"E217"),sQuery(id+"F2.wireOp",EDGE,"E218"),sQuery(id+"F2.wireOp",EDGE,"E219"),sQuery(id+"F2.wireOp",EDGE,"E220"),sQuery(id+"F2.wireOp",EDGE,"E221"),sQuery(id+"F2.wireOp",EDGE,"E222"),sQuery(id+"F2.wireOp",EDGE,"E223"),sQuery(id+"F2.wireOp",EDGE,"E224"),sQuery(id+"F2.wireOp",EDGE,"E225"),sQuery(id+"F2.wireOp",EDGE,"E226"),sQuery(id+"F2.wireOp",EDGE,"E227"),sQuery(id+"F2.wireOp",EDGE,"E228"),sQuery(id+"F2.wireOp",EDGE,"E229"),sQuery(id+"F2.wireOp",EDGE,"E230"),sQuery(id+"F2.wireOp",EDGE,"E231"),sQuery(id+"F2.wireOp",EDGE,"E232"),sQuery(id+"F2.wireOp",EDGE,"E233"),sQuery(id+"F2.wireOp",EDGE,"E234"),sQuery(id+"F2.wireOp",EDGE,"E235"),sQuery(id+"F2.wireOp",EDGE,"E236"),sQuery(id+"F2.wireOp",EDGE,"E237"),sQuery(id+"F2.wireOp",EDGE,"E238"),sQuery(id+"F2.wireOp",EDGE,"E239"),sQuery(id+"F2.wireOp",EDGE,"E240"),sQuery(id+"F2.wireOp",EDGE,"E241"),sQuery(id+"F2.wireOp",EDGE,"E242"),sQuery(id+"F2.wireOp",EDGE,"E243"),sQuery(id+"F2.wireOp",EDGE,"E244"),sQuery(id+"F2.wireOp",EDGE,"E245"),sQuery(id+"F2.wireOp",EDGE,"E246"),sQuery(id+"F2.wireOp",EDGE,"E247"),sQuery(id+"F2.wireOp",EDGE,"E248"),sQuery(id+"F2.wireOp",EDGE,"E249"),sQuery(id+"F2.wireOp",EDGE,"E250"),sQuery(id+"F2.wireOp",EDGE,"E251"),sQuery(id+"F2.wireOp",EDGE,"E252"),sQuery(id+"F2.wireOp",EDGE,"E253"),sQuery(id+"F2.wireOp",EDGE,"E254"),sQuery(id+"F2.wireOp",EDGE,"E255"),sQuery(id+"F2.wireOp",EDGE,"E256"),sQuery(id+"F2.wireOp",EDGE,"E257"),sQuery(id+"F2.wireOp",EDGE,"E258"),sQuery(id+"F2.wireOp",EDGE,"E259"),sQuery(id+"F2.wireOp",EDGE,"E260"),sQuery(id+"F2.wireOp",EDGE,"E261"),sQuery(id+"F2.wireOp",EDGE,"E262"),sQuery(id+"F2.wireOp",EDGE,"E263"),sQuery(id+"F2.wireOp",EDGE,"E264"),sQuery(id+"F2.wireOp",EDGE,"E265"),sQuery(id+"F2.wireOp",EDGE,"E266"),sQuery(id+"F2.wireOp",EDGE,"E267"),sQuery(id+"F2.wireOp",EDGE,"E268"),sQuery(id+"F2.wireOp",EDGE,"E269"),sQuery(id+"F2.wireOp",EDGE,"E270"),sQuery(id+"F2.wireOp",EDGE,"E271"),sQuery(id+"F2.wireOp",EDGE,"E272"),sQuery(id+"F2.wireOp",EDGE,"E273"),sQuery(id+"F2.wireOp",EDGE,"E274"),sQuery(id+"F2.wireOp",EDGE,"E275"),sQuery(id+"F2.wireOp",EDGE,"E276"),sQuery(id+"F2.wireOp",EDGE,"E277"),sQuery(id+"F2.wireOp",EDGE,"E278"),sQuery(id+"F2.wireOp",EDGE,"E279"),sQuery(id+"F2.wireOp",EDGE,"E280"),sQuery(id+"F2.wireOp",EDGE,"E281"),sQuery(id+"F2.wireOp",EDGE,"E282"),sQuery(id+"F2.wireOp",EDGE,"E283"),sQuery(id+"F2.wireOp",EDGE,"E284"),sQuery(id+"F2.wireOp",EDGE,"E285"),sQuery(id+"F2.wireOp",EDGE,"E286"),sQuery(id+"F2.wireOp",EDGE,"E287"),sQuery(id+"F2.wireOp",EDGE,"E288"),sQuery(id+"F2.wireOp",EDGE,"E289"),sQuery(id+"F2.wireOp",EDGE,"E290"),sQuery(id+"F2.wireOp",EDGE,"E291"),sQuery(id+"F2.wireOp",EDGE,"E292"),sQuery(id+"F2.wireOp",EDGE,"E293"),sQuery(id+"F2.wireOp",EDGE,"E294"),sQuery(id+"F2.wireOp",EDGE,"E295"),sQuery(id+"F2.wireOp",EDGE,"E296"),sQuery(id+"F2.wireOp",EDGE,"E297"),sQuery(id+"F2.wireOp",EDGE,"E298"),sQuery(id+"F2.wireOp",EDGE,"E299"),sQuery(id+"F2.wireOp",EDGE,"E300"),sQuery(id+"F2.wireOp",EDGE,"E301"),sQuery(id+"F2.wireOp",EDGE,"E302"),sQuery(id+"F2.wireOp",EDGE,"E303"),sQuery(id+"F2.wireOp",EDGE,"E304"),sQuery(id+"F2.wireOp",EDGE,"E305"),sQuery(id+"F2.wireOp",EDGE,"E306"),sQuery(id+"F2.wireOp",EDGE,"E307"),sQuery(id+"F2.wireOp",EDGE,"E308"),sQuery(id+"F2.wireOp",EDGE,"E309"),sQuery(id+"F2.wireOp",EDGE,"E310"),sQuery(id+"F2.wireOp",EDGE,"E311"),sQuery(id+"F2.wireOp",EDGE,"E312"),sQuery(id+"F2.wireOp",EDGE,"E313"),sQuery(id+"F2.wireOp",EDGE,"E314"),sQuery(id+"F2.wireOp",EDGE,"E315"),sQuery(id+"F2.wireOp",EDGE,"E316"),sQuery(id+"F2.wireOp",EDGE,"E317"),sQuery(id+"F2.wireOp",EDGE,"E318"),sQuery(id+"F2.wireOp",EDGE,"E319"),sQuery(id+"F2.wireOp",EDGE,"E320"),sQuery(id+"F2.wireOp",EDGE,"E321"),sQuery(id+"F2.wireOp",EDGE,"E322"),sQuery(id+"F2.wireOp",EDGE,"E323"),sQuery(id+"F2.wireOp",EDGE,"E324"),sQuery(id+"F2.wireOp",EDGE,"E325"),sQuery(id+"F2.wireOp",EDGE,"E326"),sQuery(id+"F2.wireOp",EDGE,"E327"),sQuery(id+"F2.wireOp",EDGE,"E328"),sQuery(id+"F2.wireOp",EDGE,"E329"),sQuery(id+"F2.wireOp",EDGE,"E330"),sQuery(id+"F2.wireOp",EDGE,"E331"),sQuery(id+"F2.wireOp",EDGE,"E332"),sQuery(id+"F2.wireOp",EDGE,"E333"),sQuery(id+"F2.wireOp",EDGE,"E334"),sQuery(id+"F2.wireOp",EDGE,"E335"),sQuery(id+"F2.wireOp",EDGE,"E336"),sQuery(id+"F2.wireOp",EDGE,"E337"),sQuery(id+"F2.wireOp",EDGE,"E338"),sQuery(id+"F2.wireOp",EDGE,"E339"),sQuery(id+"F2.wireOp",EDGE,"E340"),sQuery(id+"F2.wireOp",EDGE,"E341"),sQuery(id+"F2.wireOp",EDGE,"E342"),sQuery(id+"F2.wireOp",EDGE,"E343"),sQuery(id+"F2.wireOp",EDGE,"E344"),sQuery(id+"F2.wireOp",EDGE,"E345"),sQuery(id+"F2.wireOp",EDGE,"E346"),sQuery(id+"F2.wireOp",EDGE,"E347"),sQuery(id+"F2.wireOp",EDGE,"E348"),sQuery(id+"F2.wireOp",EDGE,"E349"),sQuery(id+"F2.wireOp",EDGE,"E350"),sQuery(id+"F2.wireOp",EDGE,"E351"),sQuery(id+"F2.wireOp",EDGE,"E352"),sQuery(id+"F2.wireOp",EDGE,"E353"),sQuery(id+"F2.wireOp",EDGE,"E354"),sQuery(id+"F2.wireOp",EDGE,"E355"),sQuery(id+"F2.wireOp",EDGE,"E356"),sQuery(id+"F2.wireOp",EDGE,"E357"),sQuery(id+"F2.wireOp",EDGE,"E358"),sQuery(id+"F2.wireOp",EDGE,"E359"),sQuery(id+"F2.wireOp",EDGE,"E360"),sQuery(id+"F2.wireOp",EDGE,"E361"),sQuery(id+"F2.wireOp",EDGE,"E362"),sQuery(id+"F2.wireOp",EDGE,"E363"),sQuery(id+"F2.wireOp",EDGE,"E364"),sQuery(id+"F2.wireOp",EDGE,"E365"),sQuery(id+"F2.wireOp",EDGE,"E366"),sQuery(id+"F2.wireOp",EDGE,"E367"),sQuery(id+"F2.wireOp",EDGE,"E368"),sQuery(id+"F2.wireOp",EDGE,"E369"),sQuery(id+"F2.wireOp",EDGE,"E370"),sQuery(id+"F2.wireOp",EDGE,"E371"),sQuery(id+"F2.wireOp",EDGE,"E372"),sQuery(id+"F2.wireOp",EDGE,"E373"),sQuery(id+"F2.wireOp",EDGE,"E374"),sQuery(id+"F2.wireOp",EDGE,"E375"),sQuery(id+"F2.wireOp",EDGE,"E376"),sQuery(id+"F2.wireOp",EDGE,"E377"),sQuery(id+"F2.wireOp",EDGE,"E378"),sQuery(id+"F2.wireOp",EDGE,"E379"),sQuery(id+"F2.wireOp",EDGE,"E380"),sQuery(id+"F2.wireOp",EDGE,"E381"),sQuery(id+"F2.wireOp",EDGE,"E382"),sQuery(id+"F2.wireOp",EDGE,"E383"),sQuery(id+"F2.wireOp",EDGE,"E384"),sQuery(id+"F2.wireOp",EDGE,"E385"),sQuery(id+"F2.wireOp",EDGE,"E386"),sQuery(id+"F2.wireOp",EDGE,"E387"),sQuery(id+"F2.wireOp",EDGE,"E388"),sQuery(id+"F2.wireOp",EDGE,"E389"),sQuery(id+"F2.wireOp",EDGE,"E390"),sQuery(id+"F2.wireOp",EDGE,"E391"),sQuery(id+"F2.wireOp",EDGE,"E392"),sQuery(id+"F2.wireOp",EDGE,"E393"),sQuery(id+"F2.wireOp",EDGE,"E394"),sQuery(id+"F2.wireOp",EDGE,"E395"),sQuery(id+"F2.wireOp",EDGE,"E396"),sQuery(id+"F2.wireOp",EDGE,"E397"),sQuery(id+"F2.wireOp",EDGE,"E398"),sQuery(id+"F2.wireOp",EDGE,"E399"),sQuery(id+"F2.wireOp",EDGE,"E400"),sQuery(id+"F2.wireOp",EDGE,"E401"),sQuery(id+"F2.wireOp",EDGE,"E402"),sQuery(id+"F2.wireOp",EDGE,"E403"),sQuery(id+"F2.wireOp",EDGE,"E404"),sQuery(id+"F2.wireOp",EDGE,"E405"),sQuery(id+"F2.wireOp",EDGE,"E406"),sQuery(id+"F2.wireOp",EDGE,"E407"),sQuery(id+"F2.wireOp",EDGE,"E408"),sQuery(id+"F2.wireOp",EDGE,"E409"),sQuery(id+"F2.wireOp",EDGE,"E410"),sQuery(id+"F2.wireOp",EDGE,"E411"),sQuery(id+"F2.wireOp",EDGE,"E412"),sQuery(id+"F2.wireOp",EDGE,"E413"),sQuery(id+"F2.wireOp",EDGE,"E414"),sQuery(id+"F2.wireOp",EDGE,"E415"),sQuery(id+"F2.wireOp",EDGE,"E416"),sQuery(id+"F2.wireOp",EDGE,"E417"),sQuery(id+"F2.wireOp",EDGE,"E418"),sQuery(id+"F2.wireOp",EDGE,"E419"),sQuery(id+"F2.wireOp",EDGE,"E420"),sQuery(id+"F2.wireOp",EDGE,"E421"),sQuery(id+"F2.wireOp",EDGE,"E422"),sQuery(id+"F2.wireOp",EDGE,"E423"),sQuery(id+"F2.wireOp",EDGE,"E424"),sQuery(id+"F2.wireOp",EDGE,"E425"),sQuery(id+"F2.wireOp",EDGE,"E426"),sQuery(id+"F2.wireOp",EDGE,"E427"),sQuery(id+"F2.wireOp",EDGE,"E428"),sQuery(id+"F2.wireOp",EDGE,"E429"),sQuery(id+"F2.wireOp",EDGE,"E430"),sQuery(id+"F2.wireOp",EDGE,"E431"),sQuery(id+"F2.wireOp",EDGE,"E432"),sQuery(id+"F2.wireOp",EDGE,"E433"),sQuery(id+"F2.wireOp",EDGE,"E434"),sQuery(id+"F2.wireOp",EDGE,"E435"),sQuery(id+"F2.wireOp",EDGE,"E436"),sQuery(id+"F2.wireOp",EDGE,"E437"),sQuery(id+"F2.wireOp",EDGE,"E438"),sQuery(id+"F2.wireOp",EDGE,"E439"),sQuery(id+"F2.wireOp",EDGE,"E440"),sQuery(id+"F2.wireOp",EDGE,"E441"),sQuery(id+"F2.wireOp",EDGE,"E442"),sQuery(id+"F2.wireOp",EDGE,"E443"),sQuery(id+"F2.wireOp",EDGE,"E444"),sQuery(id+"F2.wireOp",EDGE,"E445"),sQuery(id+"F2.wireOp",EDGE,"E446"),sQuery(id+"F2.wireOp",EDGE,"E447"),sQuery(id+"F2.wireOp",EDGE,"E448"),sQuery(id+"F2.wireOp",EDGE,"E449"),sQuery(id+"F2.wireOp",EDGE,"E450"),sQuery(id+"F2.wireOp",EDGE,"E451"),sQuery(id+"F2.wireOp",EDGE,"E452"),sQuery(id+"F2.wireOp",EDGE,"E453"),sQuery(id+"F2.wireOp",EDGE,"E454"),sQuery(id+"F2.wireOp",EDGE,"E455"),sQuery(id+"F2.wireOp",EDGE,"E456"),sQuery(id+"F2.wireOp",EDGE,"E457"),sQuery(id+"F2.wireOp",EDGE,"E458"),sQuery(id+"F2.wireOp",EDGE,"E459"),sQuery(id+"F2.wireOp",EDGE,"E460"),sQuery(id+"F2.wireOp",EDGE,"E461"),sQuery(id+"F2.wireOp",EDGE,"E462"),sQuery(id+"F2.wireOp",EDGE,"E463"),sQuery(id+"F2.wireOp",EDGE,"E464"),sQuery(id+"F2.wireOp",EDGE,"E465"),sQuery(id+"F2.wireOp",EDGE,"E466"),sQuery(id+"F2.wireOp",EDGE,"E467"),sQuery(id+"F2.wireOp",EDGE,"E468"),sQuery(id+"F2.wireOp",EDGE,"E469"),sQuery(id+"F2.wireOp",EDGE,"E470"),sQuery(id+"F2.wireOp",EDGE,"E471"),sQuery(id+"F2.wireOp",EDGE,"E472"),sQuery(id+"F2.wireOp",EDGE,"E473"),sQuery(id+"F2.wireOp",EDGE,"E474"),sQuery(id+"F2.wireOp",EDGE,"E475"),sQuery(id+"F2.wireOp",EDGE,"E476"),sQuery(id+"F2.wireOp",EDGE,"E477"),sQuery(id+"F2.wireOp",EDGE,"E478"),sQuery(id+"F2.wireOp",EDGE,"E479"),sQuery(id+"F2.wireOp",EDGE,"E480"),sQuery(id+"F2.wireOp",EDGE,"E481"),sQuery(id+"F2.wireOp",EDGE,"E482"),sQuery(id+"F2.wireOp",EDGE,"E483"),sQuery(id+"F2.wireOp",EDGE,"E484"),sQuery(id+"F2.wireOp",EDGE,"E485"),sQuery(id+"F2.wireOp",EDGE,"E486"),sQuery(id+"F2.wireOp",EDGE,"E487"),sQuery(id+"F2.wireOp",EDGE,"E488"),sQuery(id+"F2.wireOp",EDGE,"E489"),sQuery(id+"F2.wireOp",EDGE,"E490"),sQuery(id+"F2.wireOp",EDGE,"E491"),sQuery(id+"F2.wireOp",EDGE,"E492"),sQuery(id+"F2.wireOp",EDGE,"E493"),sQuery(id+"F2.wireOp",EDGE,"E494"),sQuery(id+"F2.wireOp",EDGE,"E495"),sQuery(id+"F2.wireOp",EDGE,"E496"),sQuery(id+"F2.wireOp",EDGE,"E497"),sQuery(id+"F2.wireOp",EDGE,"E498"),sQuery(id+"F2.wireOp",EDGE,"E499"),sQuery(id+"F2.wireOp",EDGE,"E500"),sQuery(id+"F2.wireOp",EDGE,"E501"),sQuery(id+"F2.wireOp",EDGE,"E502"),sQuery(id+"F2.wireOp",EDGE,"E503"),sQuery(id+"F2.wireOp",EDGE,"E504"),sQuery(id+"F2.wireOp",EDGE,"E505"),sQuery(id+"F2.wireOp",EDGE,"E506"),sQuery(id+"F2.wireOp",EDGE,"E507"),sQuery(id+"F2.wireOp",EDGE,"E508"),sQuery(id+"F2.wireOp",EDGE,"E509"),sQuery(id+"F2.wireOp",EDGE,"E510"),sQuery(id+"F2.wireOp",EDGE,"E511"),sQuery(id+"F2.wireOp",EDGE,"E512"),sQuery(id+"F2.wireOp",EDGE,"E513"),sQuery(id+"F2.wireOp",EDGE,"E514"),sQuery(id+"F2.wireOp",EDGE,"E515"),sQuery(id+"F2.wireOp",EDGE,"E516"),sQuery(id+"F2.wireOp",EDGE,"E517"),sQuery(id+"F2.wireOp",EDGE,"E518"),sQuery(id+"F2.wireOp",EDGE,"E519"),sQuery(id+"F2.wireOp",EDGE,"E520"),sQuery(id+"F2.wireOp",EDGE,"E521"),sQuery(id+"F2.wireOp",EDGE,"E522"),sQuery(id+"F2.wireOp",EDGE,"E523"),sQuery(id+"F2.wireOp",EDGE,"E524"),sQuery(id+"F2.wireOp",EDGE,"E525"),sQuery(id+"F2.wireOp",EDGE,"E526"),sQuery(id+"F2.wireOp",EDGE,"E527"),sQuery(id+"F2.wireOp",EDGE,"E528"),sQuery(id+"F2.wireOp",EDGE,"E529"),sQuery(id+"F2.wireOp",EDGE,"E530"),sQuery(id+"F2.wireOp",EDGE,"E531"),sQuery(id+"F2.wireOp",EDGE,"E532"),sQuery(id+"F2.wireOp",EDGE,"E533"),sQuery(id+"F2.wireOp",EDGE,"E534"),sQuery(id+"F2.wireOp",EDGE,"E535"),sQuery(id+"F2.wireOp",EDGE,"E536"),sQuery(id+"F2.wireOp",EDGE,"E537"),sQuery(id+"F2.wireOp",EDGE,"E538"),sQuery(id+"F2.wireOp",EDGE,"E539"),sQuery(id+"F2.wireOp",EDGE,"E540"),sQuery(id+"F2.wireOp",EDGE,"E541"),sQuery(id+"F2.wireOp",EDGE,"E542"),sQuery(id+"F2.wireOp",EDGE,"E543"),sQuery(id+"F2.wireOp",EDGE,"E544"),sQuery(id+"F2.wireOp",EDGE,"E545"),sQuery(id+"F2.wireOp",EDGE,"E546"),sQuery(id+"F2.wireOp",EDGE,"E547"),sQuery(id+"F2.wireOp",EDGE,"E548"),sQuery(id+"F2.wireOp",EDGE,"E549"),sQuery(id+"F2.wireOp",EDGE,"E550"),sQuery(id+"F2.wireOp",EDGE,"E551"),sQuery(id+"F2.wireOp",EDGE,"E552"),sQuery(id+"F2.wireOp",EDGE,"E553"),sQuery(id+"F2.wireOp",EDGE,"E554"),sQuery(id+"F2.wireOp",EDGE,"E555"),sQuery(id+"F2.wireOp",EDGE,"E556"),sQuery(id+"F2.wireOp",EDGE,"E557"),sQuery(id+"F2.wireOp",EDGE,"E558"),sQuery(id+"F2.wireOp",EDGE,"E559"),sQuery(id+"F2.wireOp",EDGE,"E560"),sQuery(id+"F2.wireOp",EDGE,"E561"),sQuery(id+"F2.wireOp",EDGE,"E562"),sQuery(id+"F2.wireOp",EDGE,"E563"),sQuery(id+"F2.wireOp",EDGE,"E564"),sQuery(id+"F2.wireOp",EDGE,"E565"),sQuery(id+"F2.wireOp",EDGE,"E566"),sQuery(id+"F2.wireOp",EDGE,"E567"),sQuery(id+"F2.wireOp",EDGE,"E568"),sQuery(id+"F2.wireOp",EDGE,"E569"),sQuery(id+"F2.wireOp",EDGE,"E570"),sQuery(id+"F2.wireOp",EDGE,"E571"),sQuery(id+"F2.wireOp",EDGE,"E572"),sQuery(id+"F2.wireOp",EDGE,"E573"),sQuery(id+"F2.wireOp",EDGE,"E574"),sQuery(id+"F2.wireOp",EDGE,"E575"),sQuery(id+"F2.wireOp",EDGE,"E576"),sQuery(id+"F2.wireOp",EDGE,"E577"),sQuery(id+"F2.wireOp",EDGE,"E578"),sQuery(id+"F2.wireOp",EDGE,"E579"),sQuery(id+"F2.wireOp",EDGE,"E580"),sQuery(id+"F2.wireOp",EDGE,"E581"),sQuery(id+"F2.wireOp",EDGE,"E582"),sQuery(id+"F2.wireOp",EDGE,"E583"),sQuery(id+"F2.wireOp",EDGE,"E584"),sQuery(id+"F2.wireOp",EDGE,"E585"),sQuery(id+"F2.wireOp",EDGE,"E586"),sQuery(id+"F2.wireOp",EDGE,"E587"),sQuery(id+"F2.wireOp",EDGE,"E588"),sQuery(id+"F2.wireOp",EDGE,"E589"),sQuery(id+"F2.wireOp",EDGE,"E590"),sQuery(id+"F2.wireOp",EDGE,"E591"),sQuery(id+"F2.wireOp",EDGE,"E592"),sQuery(id+"F2.wireOp",EDGE,"E593"),sQuery(id+"F2.wireOp",EDGE,"E594"),sQuery(id+"F2.wireOp",EDGE,"E595"),sQuery(id+"F2.wireOp",EDGE,"E596"),sQuery(id+"F2.wireOp",EDGE,"E597"),sQuery(id+"F2.wireOp",EDGE,"E598"),sQuery(id+"F2.wireOp",EDGE,"E599"),sQuery(id+"F2.wireOp",EDGE,"E600"),sQuery(id+"F2.wireOp",EDGE,"E601"),sQuery(id+"F2.wireOp",EDGE,"E602"),sQuery(id+"F2.wireOp",EDGE,"E603"),sQuery(id+"F2.wireOp",EDGE,"E604"),sQuery(id+"F2.wireOp",EDGE,"E605"),sQuery(id+"F2.wireOp",EDGE,"E606"),sQuery(id+"F2.wireOp",EDGE,"E607"),sQuery(id+"F2.wireOp",EDGE,"E608"),sQuery(id+"F2.wireOp",EDGE,"E609"),sQuery(id+"F2.wireOp",EDGE,"E610"),sQuery(id+"F2.wireOp",EDGE,"E611"),sQuery(id+"F2.wireOp",EDGE,"E612"),sQuery(id+"F2.wireOp",EDGE,"E613"),sQuery(id+"F2.wireOp",EDGE,"E614"),sQuery(id+"F2.wireOp",EDGE,"E615"),sQuery(id+"F2.wireOp",EDGE,"E616"),sQuery(id+"F2.wireOp",EDGE,"E617"),sQuery(id+"F2.wireOp",EDGE,"E618"),sQuery(id+"F2.wireOp",EDGE,"E619"),sQuery(id+"F2.wireOp",EDGE,"E620"),sQuery(id+"F2.wireOp",EDGE,"E621"),sQuery(id+"F2.wireOp",EDGE,"E622"),sQuery(id+"F2.wireOp",EDGE,"E623"),sQuery(id+"F2.wireOp",EDGE,"E624"),sQuery(id+"F2.wireOp",EDGE,"E625"),sQuery(id+"F2.wireOp",EDGE,"E626"),sQuery(id+"F2.wireOp",EDGE,"E627"),sQuery(id+"F2.wireOp",EDGE,"E628"),sQuery(id+"F2.wireOp",EDGE,"E629"),sQuery(id+"F2.wireOp",EDGE,"E630"),sQuery(id+"F2.wireOp",EDGE,"E631"),sQuery(id+"F2.wireOp",EDGE,"E632"),sQuery(id+"F2.wireOp",EDGE,"E633"),sQuery(id+"F2.wireOp",EDGE,"E634"),sQuery(id+"F2.wireOp",EDGE,"E635"),sQuery(id+"F2.wireOp",EDGE,"E636"),sQuery(id+"F2.wireOp",EDGE,"E637"),sQuery(id+"F2.wireOp",EDGE,"E638"),sQuery(id+"F2.wireOp",EDGE,"E639"),sQuery(id+"F2.wireOp",EDGE,"E640"),sQuery(id+"F2.wireOp",EDGE,"E641"),sQuery(id+"F2.wireOp",EDGE,"E642"),sQuery(id+"F2.wireOp",EDGE,"E643"),sQuery(id+"F2.wireOp",EDGE,"E644"),sQuery(id+"F2.wireOp",EDGE,"E645"),sQuery(id+"F2.wireOp",EDGE,"E646"),sQuery(id+"F2.wireOp",EDGE,"E647"),sQuery(id+"F2.wireOp",EDGE,"E648"),sQuery(id+"F2.wireOp",EDGE,"E649"),sQuery(id+"F2.wireOp",EDGE,"E650"),sQuery(id+"F2.wireOp",EDGE,"E651"),sQuery(id+"F2.wireOp",EDGE,"E652"),sQuery(id+"F2.wireOp",EDGE,"E653"),sQuery(id+"F2.wireOp",EDGE,"E654"),sQuery(id+"F2.wireOp",EDGE,"E655"),sQuery(id+"F2.wireOp",EDGE,"E656"),sQuery(id+"F2.wireOp",EDGE,"E657"),sQuery(id+"F2.wireOp",EDGE,"E658"),sQuery(id+"F2.wireOp",EDGE,"E659"),sQuery(id+"F2.wireOp",EDGE,"E660"),sQuery(id+"F2.wireOp",EDGE,"E661"),sQuery(id+"F2.wireOp",EDGE,"E662"),sQuery(id+"F2.wireOp",EDGE,"E663"),sQuery(id+"F2.wireOp",EDGE,"E664"),sQuery(id+"F2.wireOp",EDGE,"E665"),sQuery(id+"F2.wireOp",EDGE,"E666"),sQuery(id+"F2.wireOp",EDGE,"E667"),sQuery(id+"F2.wireOp",EDGE,"E668"),sQuery(id+"F2.wireOp",EDGE,"E669"),sQuery(id+"F2.wireOp",EDGE,"E670"),sQuery(id+"F2.wireOp",EDGE,"E671"),sQuery(id+"F2.wireOp",EDGE,"E672"),sQuery(id+"F2.wireOp",EDGE,"E673"),sQuery(id+"F2.wireOp",EDGE,"E674"),sQuery(id+"F2.wireOp",EDGE,"E675"),sQuery(id+"F2.wireOp",EDGE,"E676"),sQuery(id+"F2.wireOp",EDGE,"E677"),sQuery(id+"F2.wireOp",EDGE,"E678"),sQuery(id+"F2.wireOp",EDGE,"E679"),sQuery(id+"F2.wireOp",EDGE,"E680"),sQuery(id+"F2.wireOp",EDGE,"E681"),sQuery(id+"F2.wireOp",EDGE,"E682"),sQuery(id+"F2.wireOp",EDGE,"E683"),sQuery(id+"F2.wireOp",EDGE,"E684"),sQuery(id+"F2.wireOp",EDGE,"E685"),sQuery(id+"F2.wireOp",EDGE,"E686"),sQuery(id+"F2.wireOp",EDGE,"E687"),sQuery(id+"F2.wireOp",EDGE,"E688"),sQuery(id+"F2.wireOp",EDGE,"E689"),sQuery(id+"F2.wireOp",EDGE,"E690"),sQuery(id+"F2.wireOp",EDGE,"E691"),sQuery(id+"F2.wireOp",EDGE,"E692"),sQuery(id+"F2.wireOp",EDGE,"E693"),sQuery(id+"F2.wireOp",EDGE,"E694"),sQuery(id+"F2.wireOp",EDGE,"E695"),sQuery(id+"F2.wireOp",EDGE,"E696"),sQuery(id+"F2.wireOp",EDGE,"E697"),sQuery(id+"F2.wireOp",EDGE,"E698"),sQuery(id+"F2.wireOp",EDGE,"E699"),sQuery(id+"F2.wireOp",EDGE,"E700"),sQuery(id+"F2.wireOp",EDGE,"E701"),sQuery(id+"F2.wireOp",EDGE,"E702"),sQuery(id+"F2.wireOp",EDGE,"E703"),sQuery(id+"F2.wireOp",EDGE,"E704"),sQuery(id+"F2.wireOp",EDGE,"E705"),sQuery(id+"F2.wireOp",EDGE,"E706"),sQuery(id+"F2.wireOp",EDGE,"E707"),sQuery(id+"F2.wireOp",EDGE,"E708"),sQuery(id+"F2.wireOp",EDGE,"E709"),sQuery(id+"F2.wireOp",EDGE,"E710"),sQuery(id+"F2.wireOp",EDGE,"E711"),sQuery(id+"F2.wireOp",EDGE,"E712"),sQuery(id+"F2.wireOp",EDGE,"E713"),sQuery(id+"F2.wireOp",EDGE,"E714"),sQuery(id+"F2.wireOp",EDGE,"E715"),sQuery(id+"F2.wireOp",EDGE,"E716"),sQuery(id+"F2.wireOp",EDGE,"E717"),sQuery(id+"F2.wireOp",EDGE,"E718"),sQuery(id+"F2.wireOp",EDGE,"E719"),sQuery(id+"F2.wireOp",EDGE,"E720"),sQuery(id+"F2.wireOp",EDGE,"E721"),sQuery(id+"F2.wireOp",EDGE,"E722"),sQuery(id+"F2.wireOp",EDGE,"E723"),sQuery(id+"F2.wireOp",EDGE,"E724"),sQuery(id+"F2.wireOp",EDGE,"E725"),sQuery(id+"F2.wireOp",EDGE,"E726"),sQuery(id+"F2.wireOp",EDGE,"E727"),sQuery(id+"F2.wireOp",EDGE,"E728"),sQuery(id+"F2.wireOp",EDGE,"E729"),sQuery(id+"F2.wireOp",EDGE,"E730"),sQuery(id+"F2.wireOp",EDGE,"E731"),sQuery(id+"F2.wireOp",EDGE,"E732"),sQuery(id+"F2.wireOp",EDGE,"E733"),sQuery(id+"F2.wireOp",EDGE,"E734"),sQuery(id+"F2.wireOp",EDGE,"E735"),sQuery(id+"F2.wireOp",EDGE,"E736"),sQuery(id+"F2.wireOp",EDGE,"E737"),sQuery(id+"F2.wireOp",EDGE,"E738"),sQuery(id+"F2.wireOp",EDGE,"E739"),sQuery(id+"F2.wireOp",EDGE,"E740"),sQuery(id+"F2.wireOp",EDGE,"E741"),sQuery(id+"F2.wireOp",EDGE,"E742"),sQuery(id+"F2.wireOp",EDGE,"E743"),sQuery(id+"F2.wireOp",EDGE,"E744"),sQuery(id+"F2.wireOp",EDGE,"E745"),sQuery(id+"F2.wireOp",EDGE,"E746"),sQuery(id+"F2.wireOp",EDGE,"E747"),sQuery(id+"F2.wireOp",EDGE,"E748"),sQuery(id+"F2.wireOp",EDGE,"E749"),sQuery(id+"F2.wireOp",EDGE,"E750"),sQuery(id+"F2.wireOp",EDGE,"E751"),sQuery(id+"F2.wireOp",EDGE,"E752"),sQuery(id+"F2.wireOp",EDGE,"E753"),sQuery(id+"F2.wireOp",EDGE,"E754"),sQuery(id+"F2.wireOp",EDGE,"E755"),sQuery(id+"F2.wireOp",EDGE,"E756"),sQuery(id+"F2.wireOp",EDGE,"E757"),sQuery(id+"F2.wireOp",EDGE,"E758"),sQuery(id+"F2.wireOp",EDGE,"E759"),sQuery(id+"F2.wireOp",EDGE,"E760"),sQuery(id+"F2.wireOp",EDGE,"E761"),sQuery(id+"F2.wireOp",EDGE,"E762"),sQuery(id+"F2.wireOp",EDGE,"E763"),sQuery(id+"F2.wireOp",EDGE,"E764"),sQuery(id+"F2.wireOp",EDGE,"E765"),sQuery(id+"F2.wireOp",EDGE,"E766"),sQuery(id+"F2.wireOp",EDGE,"E767"),sQuery(id+"F2.wireOp",EDGE,"E768"),sQuery(id+"F2.wireOp",EDGE,"E769"),sQuery(id+"F2.wireOp",EDGE,"E770"),sQuery(id+"F2.wireOp",EDGE,"E771"),sQuery(id+"F2.wireOp",EDGE,"E772"),sQuery(id+"F2.wireOp",EDGE,"E773"),sQuery(id+"F2.wireOp",EDGE,"E774"),sQuery(id+"F2.wireOp",EDGE,"E775"),sQuery(id+"F2.wireOp",EDGE,"E776"),sQuery(id+"F2.wireOp",EDGE,"E777"),sQuery(id+"F2.wireOp",EDGE,"E778"),sQuery(id+"F2.wireOp",EDGE,"E779"),sQuery(id+"F2.wireOp",EDGE,"E780"),sQuery(id+"F2.wireOp",EDGE,"E781"),sQuery(id+"F2.wireOp",EDGE,"E782"),sQuery(id+"F2.wireOp",EDGE,"E783"),sQuery(id+"F2.wireOp",EDGE,"E784"),sQuery(id+"F2.wireOp",EDGE,"E785"),sQuery(id+"F2.wireOp",EDGE,"E786"),sQuery(id+"F2.wireOp",EDGE,"E787"),sQuery(id+"F2.wireOp",EDGE,"E788"),sQuery(id+"F2.wireOp",EDGE,"E789"),sQuery(id+"F2.wireOp",EDGE,"E790"),sQuery(id+"F2.wireOp",EDGE,"E791"),sQuery(id+"F2.wireOp",EDGE,"E792"),sQuery(id+"F2.wireOp",EDGE,"E793"),sQuery(id+"F2.wireOp",EDGE,"E794"),sQuery(id+"F2.wireOp",EDGE,"E795"),sQuery(id+"F2.wireOp",EDGE,"E796"),sQuery(id+"F2.wireOp",EDGE,"E797"),sQuery(id+"F2.wireOp",EDGE,"E798"),sQuery(id+"F2.wireOp",EDGE,"E799"),sQuery(id+"F2.wireOp",EDGE,"E800"),sQuery(id+"F2.wireOp",EDGE,"E801"),sQuery(id+"F2.wireOp",EDGE,"E802"),sQuery(id+"F2.wireOp",EDGE,"E803"),sQuery(id+"F2.wireOp",EDGE,"E804"),sQuery(id+"F2.wireOp",EDGE,"E805"),sQuery(id+"F2.wireOp",EDGE,"E806"),sQuery(id+"F2.wireOp",EDGE,"E807"),sQuery(id+"F2.wireOp",EDGE,"E808"),sQuery(id+"F2.wireOp",EDGE,"E809"),sQuery(id+"F2.wireOp",EDGE,"E810"),sQuery(id+"F2.wireOp",EDGE,"E811"),sQuery(id+"F2.wireOp",EDGE,"E812"),sQuery(id+"F2.wireOp",EDGE,"E813"),sQuery(id+"F2.wireOp",EDGE,"E814"),sQuery(id+"F2.wireOp",EDGE,"E815"),sQuery(id+"F2.wireOp",EDGE,"E816"),sQuery(id+"F2.wireOp",EDGE,"E817"),sQuery(id+"F2.wireOp",EDGE,"E818"),sQuery(id+"F2.wireOp",EDGE,"E819"),sQuery(id+"F2.wireOp",EDGE,"E820"),sQuery(id+"F2.wireOp",EDGE,"E821"),sQuery(id+"F2.wireOp",EDGE,"E822"),sQuery(id+"F2.wireOp",EDGE,"E823"),sQuery(id+"F2.wireOp",EDGE,"E824"),sQuery(id+"F2.wireOp",EDGE,"E825"),sQuery(id+"F2.wireOp",EDGE,"E826"),sQuery(id+"F2.wireOp",EDGE,"E827"),sQuery(id+"F2.wireOp",EDGE,"E828"),sQuery(id+"F2.wireOp",EDGE,"E829"),sQuery(id+"F2.wireOp",EDGE,"E830"),sQuery(id+"F2.wireOp",EDGE,"E831"),sQuery(id+"F2.wireOp",EDGE,"E832"),sQuery(id+"F2.wireOp",EDGE,"E833"),sQuery(id+"F2.wireOp",EDGE,"E834"),sQuery(id+"F2.wireOp",EDGE,"E835"),sQuery(id+"F2.wireOp",EDGE,"E836"),sQuery(id+"F2.wireOp",EDGE,"E837"),sQuery(id+"F2.wireOp",EDGE,"E838"),sQuery(id+"F2.wireOp",EDGE,"E839"),sQuery(id+"F2.wireOp",EDGE,"E840"),sQuery(id+"F2.wireOp",EDGE,"E841"),sQuery(id+"F2.wireOp",EDGE,"E842"),sQuery(id+"F2.wireOp",EDGE,"E843"),sQuery(id+"F2.wireOp",EDGE,"E844"),sQuery(id+"F2.wireOp",EDGE,"E845"),sQuery(id+"F2.wireOp",EDGE,"E846"),sQuery(id+"F2.wireOp",EDGE,"E847"),sQuery(id+"F2.wireOp",EDGE,"E848"),sQuery(id+"F2.wireOp",EDGE,"E849"),sQuery(id+"F2.wireOp",EDGE,"E850"),sQuery(id+"F2.wireOp",EDGE,"E851"),sQuery(id+"F2.wireOp",EDGE,"E852"),sQuery(id+"F2.wireOp",EDGE,"E853"),sQuery(id+"F2.wireOp",EDGE,"E854"),sQuery(id+"F2.wireOp",EDGE,"E855"),sQuery(id+"F2.wireOp",EDGE,"E856"),sQuery(id+"F2.wireOp",EDGE,"E857"),sQuery(id+"F2.wireOp",EDGE,"E858"),sQuery(id+"F2.wireOp",EDGE,"E859"),sQuery(id+"F2.wireOp",EDGE,"E860"),sQuery(id+"F2.wireOp",EDGE,"E861"),sQuery(id+"F2.wireOp",EDGE,"E862"),sQuery(id+"F2.wireOp",EDGE,"E863"),sQuery(id+"F2.wireOp",EDGE,"E864"),sQuery(id+"F2.wireOp",EDGE,"E865"),sQuery(id+"F2.wireOp",EDGE,"E866"),sQuery(id+"F2.wireOp",EDGE,"E867"),sQuery(id+"F2.wireOp",EDGE,"E868"),sQuery(id+"F2.wireOp",EDGE,"E869"),sQuery(id+"F2.wireOp",EDGE,"E870"),sQuery(id+"F2.wireOp",EDGE,"E871"),sQuery(id+"F2.wireOp",EDGE,"E872"),sQuery(id+"F2.wireOp",EDGE,"E873"),sQuery(id+"F2.wireOp",EDGE,"E874"),sQuery(id+"F2.wireOp",EDGE,"E875"),sQuery(id+"F2.wireOp",EDGE,"E876"),sQuery(id+"F2.wireOp",EDGE,"E877"),sQuery(id+"F2.wireOp",EDGE,"E878"),sQuery(id+"F2.wireOp",EDGE,"E879"),sQuery(id+"F2.wireOp",EDGE,"E880"),sQuery(id+"F2.wireOp",EDGE,"E881"),sQuery(id+"F2.wireOp",EDGE,"E882"),sQuery(id+"F2.wireOp",EDGE,"E883"),sQuery(id+"F2.wireOp",EDGE,"E884"),sQuery(id+"F2.wireOp",EDGE,"E885"),sQuery(id+"F2.wireOp",EDGE,"E886"),sQuery(id+"F2.wireOp",EDGE,"E887"),sQuery(id+"F2.wireOp",EDGE,"E888"),sQuery(id+"F2.wireOp",EDGE,"E889"),sQuery(id+"F2.wireOp",EDGE,"E890"),sQuery(id+"F2.wireOp",EDGE,"E891"),sQuery(id+"F2.wireOp",EDGE,"E892"),sQuery(id+"F2.wireOp",EDGE,"E893"),sQuery(id+"F2.wireOp",EDGE,"E894"),sQuery(id+"F2.wireOp",EDGE,"E895"),sQuery(id+"F2.wireOp",EDGE,"E896"),sQuery(id+"F2.wireOp",EDGE,"E897"),sQuery(id+"F2.wireOp",EDGE,"E898"),sQuery(id+"F2.wireOp",EDGE,"E899"),sQuery(id+"F2.wireOp",EDGE,"E900"),sQuery(id+"F2.wireOp",EDGE,"E901"),sQuery(id+"F2.wireOp",EDGE,"E902"),sQuery(id+"F2.wireOp",EDGE,"E903"),sQuery(id+"F2.wireOp",EDGE,"E904"),sQuery(id+"F2.wireOp",EDGE,"E905"),sQuery(id+"F2.wireOp",EDGE,"E906"),sQuery(id+"F2.wireOp",EDGE,"E907"),sQuery(id+"F2.wireOp",EDGE,"E908"),sQuery(id+"F2.wireOp",EDGE,"E909"),sQuery(id+"F2.wireOp",EDGE,"E910"),sQuery(id+"F2.wireOp",EDGE,"E911"),sQuery(id+"F2.wireOp",EDGE,"E912"),sQuery(id+"F2.wireOp",EDGE,"E913"),sQuery(id+"F2.wireOp",EDGE,"E914"),sQuery(id+"F2.wireOp",EDGE,"E915"),sQuery(id+"F2.wireOp",EDGE,"E916"),sQuery(id+"F2.wireOp",EDGE,"E917"),sQuery(id+"F2.wireOp",EDGE,"E918"),sQuery(id+"F2.wireOp",EDGE,"E919"),sQuery(id+"F2.wireOp",EDGE,"E920"),sQuery(id+"F2.wireOp",EDGE,"E921"),sQuery(id+"F2.wireOp",EDGE,"E922"),sQuery(id+"F2.wireOp",EDGE,"E923"),sQuery(id+"F2.wireOp",EDGE,"E924"),sQuery(id+"F2.wireOp",EDGE,"E925"),sQuery(id+"F2.wireOp",EDGE,"E926"),sQuery(id+"F2.wireOp",EDGE,"E927"),sQuery(id+"F2.wireOp",EDGE,"E928"),sQuery(id+"F2.wireOp",EDGE,"E929"),sQuery(id+"F2.wireOp",EDGE,"E930"),sQuery(id+"F2.wireOp",EDGE,"E931"),sQuery(id+"F2.wireOp",EDGE,"E932"),sQuery(id+"F2.wireOp",EDGE,"E933"),sQuery(id+"F2.wireOp",EDGE,"E934"),sQuery(id+"F2.wireOp",EDGE,"E935"),sQuery(id+"F2.wireOp",EDGE,"E936"),sQuery(id+"F2.wireOp",EDGE,"E937"),sQuery(id+"F2.wireOp",EDGE,"E938"),sQuery(id+"F2.wireOp",EDGE,"E939"),sQuery(id+"F2.wireOp",EDGE,"E940"),sQuery(id+"F2.wireOp",EDGE,"E941"),sQuery(id+"F2.wireOp",EDGE,"E942"),sQuery(id+"F2.wireOp",EDGE,"E943"),sQuery(id+"F2.wireOp",EDGE,"E944"),sQuery(id+"F2.wireOp",EDGE,"E945"),sQuery(id+"F2.wireOp",EDGE,"E946"),sQuery(id+"F2.wireOp",EDGE,"E947"),sQuery(id+"F2.wireOp",EDGE,"E948"),sQuery(id+"F2.wireOp",EDGE,"E949"),sQuery(id+"F2.wireOp",EDGE,"E950"),sQuery(id+"F2.wireOp",EDGE,"E951"),sQuery(id+"F2.wireOp",EDGE,"E952"),sQuery(id+"F2.wireOp",EDGE,"E953"),sQuery(id+"F2.wireOp",EDGE,"E954"),sQuery(id+"F2.wireOp",EDGE,"E955"),sQuery(id+"F2.wireOp",EDGE,"E956"),sQuery(id+"F2.wireOp",EDGE,"E957"),sQuery(id+"F2.wireOp",EDGE,"E958"),sQuery(id+"F2.wireOp",EDGE,"E959"),sQuery(id+"F2.wireOp",EDGE,"E960"),sQuery(id+"F2.wireOp",EDGE,"E961"),sQuery(id+"F2.wireOp",EDGE,"E962"),sQuery(id+"F2.wireOp",EDGE,"E963"),sQuery(id+"F2.wireOp",EDGE,"E964"),sQuery(id+"F2.wireOp",EDGE,"E965"),sQuery(id+"F2.wireOp",EDGE,"E966"),sQuery(id+"F2.wireOp",EDGE,"E967"),sQuery(id+"F2.wireOp",EDGE,"E968"),sQuery(id+"F2.wireOp",EDGE,"E969"),sQuery(id+"F2.wireOp",EDGE,"E970"),sQuery(id+"F2.wireOp",EDGE,"E971"),sQuery(id+"F2.wireOp",EDGE,"E972"),sQuery(id+"F2.wireOp",EDGE,"E973"),sQuery(id+"F2.wireOp",EDGE,"E974"),sQuery(id+"F2.wireOp",EDGE,"E975"),sQuery(id+"F2.wireOp",EDGE,"E976"),sQuery(id+"F2.wireOp",EDGE,"E977"),sQuery(id+"F2.wireOp",EDGE,"E978"),sQuery(id+"F2.wireOp",EDGE,"E979"),sQuery(id+"F2.wireOp",EDGE,"E980"),sQuery(id+"F2.wireOp",EDGE,"E981"),sQuery(id+"F2.wireOp",EDGE,"E982"),sQuery(id+"F2.wireOp",EDGE,"E983"),sQuery(id+"F2.wireOp",EDGE,"E984"),sQuery(id+"F2.wireOp",EDGE,"E985"),sQuery(id+"F2.wireOp",EDGE,"E986"),sQuery(id+"F2.wireOp",EDGE,"E987"),sQuery(id+"F2.wireOp",EDGE,"E988"),sQuery(id+"F2.wireOp",EDGE,"E989"),sQuery(id+"F2.wireOp",EDGE,"E990"),sQuery(id+"F2.wireOp",EDGE,"E991"),sQuery(id+"F2.wireOp",EDGE,"E992"),sQuery(id+"F2.wireOp",EDGE,"E993"),sQuery(id+"F2.wireOp",EDGE,"E994"),sQuery(id+"F2.wireOp",EDGE,"E995"),sQuery(id+"F2.wireOp",EDGE,"E996"),sQuery(id+"F2.wireOp",EDGE,"E997"),sQuery(id+"F2.wireOp",EDGE,"E998"),sQuery(id+"F2.wireOp",EDGE,"E999"),sQuery(id+"F2.wireOp",EDGE,"E1000"),sQuery(id+"F2.wireOp",EDGE,"E1001"),sQuery(id+"F2.wireOp",EDGE,"E1002"),sQuery(id+"F2.wireOp",EDGE,"E1003"),sQuery(id+"F2.wireOp",EDGE,"E1004"),sQuery(id+"F2.wireOp",EDGE,"E1005"),sQuery(id+"F2.wireOp",EDGE,"E1006"),sQuery(id+"F2.wireOp",EDGE,"E1007"),sQuery(id+"F2.wireOp",EDGE,"E1008"),sQuery(id+"F2.wireOp",EDGE,"E1009"),sQuery(id+"F2.wireOp",EDGE,"E1010"),sQuery(id+"F2.wireOp",EDGE,"E1011"),sQuery(id+"F2.wireOp",EDGE,"E1012"),sQuery(id+"F2.wireOp",EDGE,"E1013"),sQuery(id+"F2.wireOp",EDGE,"E1014"),sQuery(id+"F2.wireOp",EDGE,"E1015"),sQuery(id+"F2.wireOp",EDGE,"E1016"),sQuery(id+"F2.wireOp",EDGE,"E1017"),sQuery(id+"F2.wireOp",EDGE,"E1018"),sQuery(id+"F2.wireOp",EDGE,"E1019"),sQuery(id+"F2.wireOp",EDGE,"E1020"),sQuery(id+"F2.wireOp",EDGE,"E1021"),sQuery(id+"F2.wireOp",EDGE,"E1022"),sQuery(id+"F2.wireOp",EDGE,"E1023"),sQuery(id+"F2.wireOp",EDGE,"E1024"),sQuery(id+"F2.wireOp",EDGE,"E1025"),sQuery(id+"F2.wireOp",EDGE,"E1026"),sQuery(id+"F2.wireOp",EDGE,"E1027"),sQuery(id+"F2.wireOp",EDGE,"E1028"),sQuery(id+"F2.wireOp",EDGE,"E1029"),sQuery(id+"F2.wireOp",EDGE,"E1030"),sQuery(id+"F2.wireOp",EDGE,"E1031"),sQuery(id+"F2.wireOp",EDGE,"E1032"),sQuery(id+"F2.wireOp",EDGE,"E1033"),sQuery(id+"F2.wireOp",EDGE,"E1034"),sQuery(id+"F2.wireOp",EDGE,"E1035"),sQuery(id+"F2.wireOp",EDGE,"E1036"),sQuery(id+"F2.wireOp",EDGE,"E1037"),sQuery(id+"F2.wireOp",EDGE,"E1038"),sQuery(id+"F2.wireOp",EDGE,"E1039"),sQuery(id+"F2.wireOp",EDGE,"E1040"),sQuery(id+"F2.wireOp",EDGE,"E1041"),sQuery(id+"F2.wireOp",EDGE,"E1042"),sQuery(id+"F2.wireOp",EDGE,"E1043"),sQuery(id+"F2.wireOp",EDGE,"E1044"),sQuery(id+"F2.wireOp",EDGE,"E1045"),sQuery(id+"F2.wireOp",EDGE,"E1046"),sQuery(id+"F2.wireOp",EDGE,"E1047"),sQuery(id+"F2.wireOp",EDGE,"E1048"),sQuery(id+"F2.wireOp",EDGE,"E1049"),sQuery(id+"F2.wireOp",EDGE,"E1050"),sQuery(id+"F2.wireOp",EDGE,"E1051"),sQuery(id+"F2.wireOp",EDGE,"E1052"),sQuery(id+"F2.wireOp",EDGE,"E1053"),sQuery(id+"F2.wireOp",EDGE,"E1054"),sQuery(id+"F2.wireOp",EDGE,"E1055"),sQuery(id+"F2.wireOp",EDGE,"E1056"),sQuery(id+"F2.wireOp",EDGE,"E1057"),sQuery(id+"F2.wireOp",EDGE,"E1058"),sQuery(id+"F2.wireOp",EDGE,"E1059"),sQuery(id+"F2.wireOp",EDGE,"E1060"),sQuery(id+"F2.wireOp",EDGE,"E1061"),sQuery(id+"F2.wireOp",EDGE,"E1062"),sQuery(id+"F2.wireOp",EDGE,"E1063"),sQuery(id+"F2.wireOp",EDGE,"E1064"),sQuery(id+"F2.wireOp",EDGE,"E1065"),sQuery(id+"F2.wireOp",EDGE,"E1066"),sQuery(id+"F2.wireOp",EDGE,"E1067"),sQuery(id+"F2.wireOp",EDGE,"E1068"),sQuery(id+"F2.wireOp",EDGE,"E1069"),sQuery(id+"F2.wireOp",EDGE,"E1070"),sQuery(id+"F2.wireOp",EDGE,"E1071"),sQuery(id+"F2.wireOp",EDGE,"E1072"),sQuery(id+"F2.wireOp",EDGE,"E1073"),sQuery(id+"F2.wireOp",EDGE,"E1074"),sQuery(id+"F2.wireOp",EDGE,"E1075"),sQuery(id+"F2.wireOp",EDGE,"E1076"),sQuery(id+"F2.wireOp",EDGE,"E1077"),sQuery(id+"F2.wireOp",EDGE,"E1078"),sQuery(id+"F2.wireOp",EDGE,"E1079"),sQuery(id+"F2.wireOp",EDGE,"E1080"),sQuery(id+"F2.wireOp",EDGE,"E1081"),sQuery(id+"F2.wireOp",EDGE,"E1082"),sQuery(id+"F2.wireOp",EDGE,"E1083"),sQuery(id+"F2.wireOp",EDGE,"E1084"),sQuery(id+"F2.wireOp",EDGE,"E1085"),sQuery(id+"F2.wireOp",EDGE,"E1086"),sQuery(id+"F2.wireOp",EDGE,"E1087"),sQuery(id+"F2.wireOp",EDGE,"E1088"),sQuery(id+"F2.wireOp",EDGE,"E1089"),sQuery(id+"F2.wireOp",EDGE,"E1090"),sQuery(id+"F2.wireOp",EDGE,"E1091"),sQuery(id+"F2.wireOp",EDGE,"E1092"),sQuery(id+"F2.wireOp",EDGE,"E1093"),sQuery(id+"F2.wireOp",EDGE,"E1094"),sQuery(id+"F2.wireOp",EDGE,"E1095"),sQuery(id+"F2.wireOp",EDGE,"E1096"),sQuery(id+"F2.wireOp",EDGE,"E1097"),sQuery(id+"F2.wireOp",EDGE,"E1098"),sQuery(id+"F2.wireOp",EDGE,"E1099"),sQuery(id+"F2.wireOp",EDGE,"E1100"),sQuery(id+"F2.wireOp",EDGE,"E1101"),sQuery(id+"F2.wireOp",EDGE,"E1102"),sQuery(id+"F2.wireOp",EDGE,"E1103"),sQuery(id+"F2.wireOp",EDGE,"E1104"),sQuery(id+"F2.wireOp",EDGE,"E1105"),sQuery(id+"F2.wireOp",EDGE,"E1106"),sQuery(id+"F2.wireOp",EDGE,"E1107"),sQuery(id+"F2.wireOp",EDGE,"E1108"),sQuery(id+"F2.wireOp",EDGE,"E1109"),sQuery(id+"F2.wireOp",EDGE,"E1110"),sQuery(id+"F2.wireOp",EDGE,"E1111"),sQuery(id+"F2.wireOp",EDGE,"E1112"),sQuery(id+"F2.wireOp",EDGE,"E1113"),sQuery(id+"F2.wireOp",EDGE,"E1114"),sQuery(id+"F2.wireOp",EDGE,"E1115"),sQuery(id+"F2.wireOp",EDGE,"E1116"),sQuery(id+"F2.wireOp",EDGE,"E1117"),sQuery(id+"F2.wireOp",EDGE,"E1118"),sQuery(id+"F2.wireOp",EDGE,"E1119"),sQuery(id+"F2.wireOp",EDGE,"E1120"),sQuery(id+"F2.wireOp",EDGE,"E1121"),sQuery(id+"F2.wireOp",EDGE,"E1122"),sQuery(id+"F2.wireOp",EDGE,"E1123"),sQuery(id+"F2.wireOp",EDGE,"E1124"),sQuery(id+"F2.wireOp",EDGE,"E1125"),sQuery(id+"F2.wireOp",EDGE,"E1126"),sQuery(id+"F2.wireOp",EDGE,"E1127"),sQuery(id+"F2.wireOp",EDGE,"E1128"),sQuery(id+"F2.wireOp",EDGE,"E1129"),sQuery(id+"F2.wireOp",EDGE,"E1130"),sQuery(id+"F2.wireOp",EDGE,"E1131"),sQuery(id+"F2.wireOp",EDGE,"E1132"),sQuery(id+"F2.wireOp",EDGE,"E1133"),sQuery(id+"F2.wireOp",EDGE,"E1134"),sQuery(id+"F2.wireOp",EDGE,"E1135"),sQuery(id+"F2.wireOp",EDGE,"E1136"),sQuery(id+"F2.wireOp",EDGE,"E1137"),sQuery(id+"F2.wireOp",EDGE,"E1138"),sQuery(id+"F2.wireOp",EDGE,"E1139"),sQuery(id+"F2.wireOp",EDGE,"E1140"),sQuery(id+"F2.wireOp",EDGE,"E1141"),sQuery(id+"F2.wireOp",EDGE,"E1142")])]});
            var Q1;
            Q1=qCreatedBy(makeId("Origin.pointOp"),VERTEX);
            transform(context, id + "F4", {"entities" : qUnion([Q0]), "transformType" : TransformType.SCALE_UNIFORMLY, "scale" : 0.1, "scalePoint" : qUnion([Q1]), "makeCopy" : false});
        }
    });
